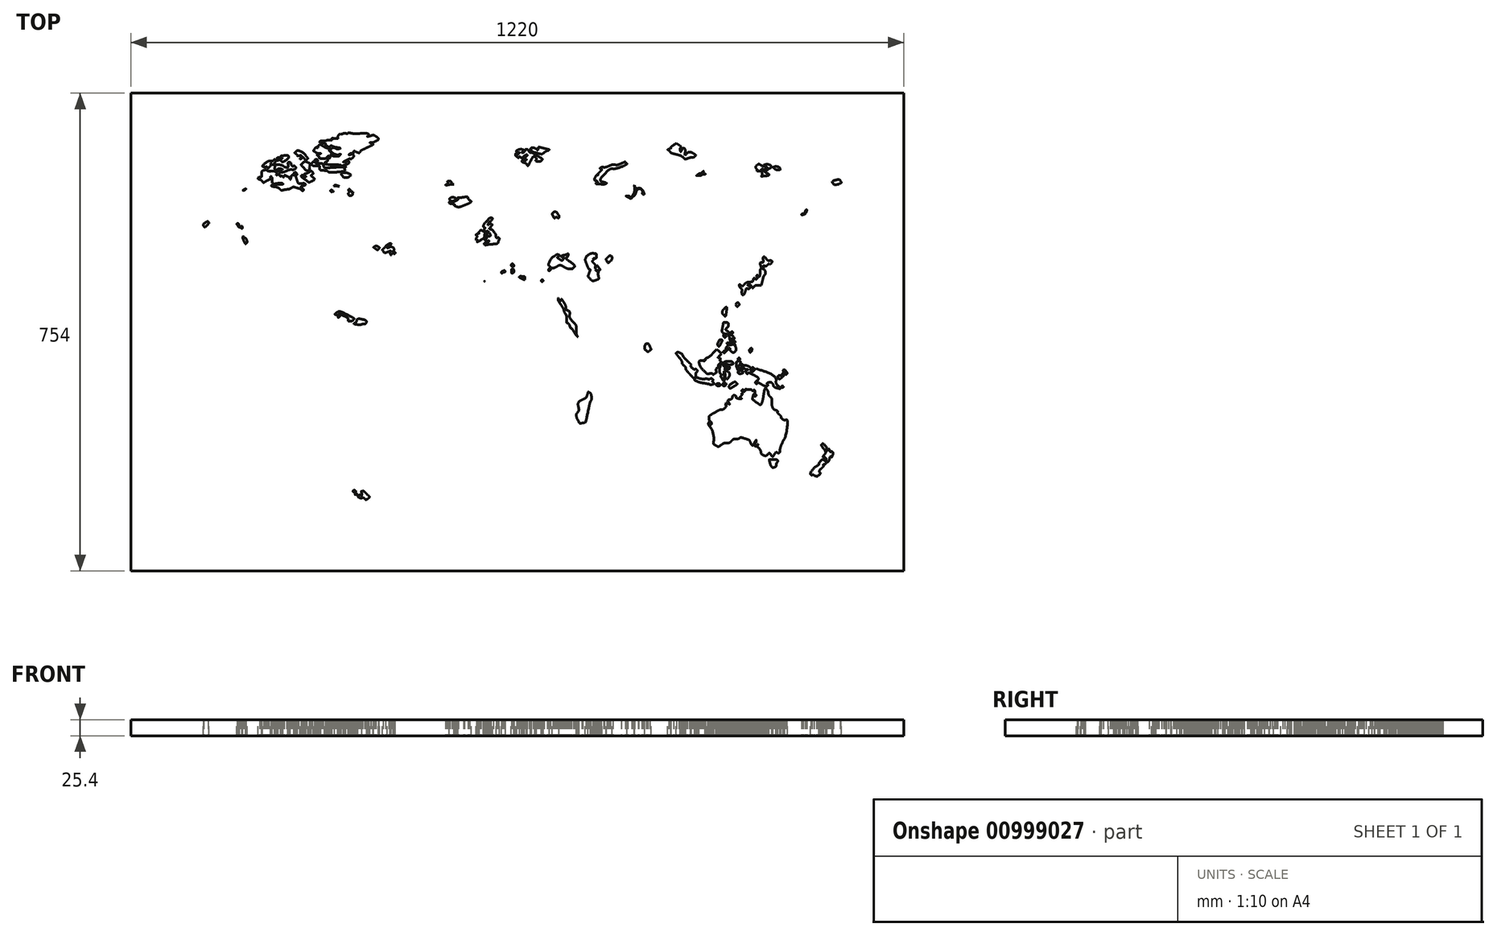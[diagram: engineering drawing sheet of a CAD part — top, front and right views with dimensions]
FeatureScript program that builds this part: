
annotation { "Feature Type Name" : "Feature", "Feature Type Description" : "" }
export const myFeature = defineFeature(function(context is Context, id is Id, definition is map)
    precondition{}
    {
        {
            var Q0;
            Q0=qCreatedBy(makeId("Top.planeOp"),FACE);
            var sketch = newSketch(context, id + "F0", { "sketchPlane" : qUnion([Q0])});
            skLineSegment(sketch, "E0.bottom", {"start": v(610, -377) * mm, "end": v(-610, -377) * mm});
            skLineSegment(sketch, "E0.top", {"start": v(610, 377) * mm, "end": v(-610, 377) * mm});
            skLineSegment(sketch, "E0.left", {"start": v(610, -377) * mm, "end": v(610, 377) * mm});
            skLineSegment(sketch, "E0.right", {"start": v(-610, -377) * mm, "end": v(-610, 377) * mm});
            skPoint(sketch, "E0.middle", {"position": v(0, 0) * mm});
            skSolve(sketch);
        }
        {
            var Q0;
            Q0=makeQuery(id+"F0.imprint","IMPRINT",FACE,{"disambiguationData":[TD([[makeQuery(id+"F0.imprint","IMPRINT",EDGE,{"derivedFrom":sQuery(id+"F0.wireOp",EDGE,"E0.bottom")}),-1.0]])]});
            var sketch = newSketch(context, id + "F1", { "sketchPlane" : qUnion([Q0])});
            skLineSegment(sketch, "E1", {"start": v(571.5, 342.75) * mm, "end": v(571.5, -342.75) * mm});
            skFitSpline(sketch, "E2", {"points": [v(-240.66, -263.07) * mm, v(-241.04, -262.46) * mm, v(-242.9, -261.96) * mm, v(-244.8, -261.96) * mm]});
            skFitSpline(sketch, "E3", {"points": [v(-244.8, -261.96) * mm, v(-248.42, -261.96) * mm, v(-251.99, -259.06) * mm, v(-249.93, -257.79) * mm]});
            skFitSpline(sketch, "E4", {"points": [v(-249.93, -257.79) * mm, v(-249.28, -257.39) * mm, v(-247.96, -257.37) * mm, v(-246.98, -257.75) * mm]});
            skFitSpline(sketch, "E5", {"points": [v(-246.98, -257.75) * mm, v(-245.7, -258.24) * mm, v(-245.28, -257.64) * mm, v(-245.49, -255.61) * mm]});
            skFitSpline(sketch, "E6", {"points": [v(-245.49, -255.61) * mm, v(-245.91, -251.52) * mm, v(-245.94, -251.5) * mm, v(-247.74, -253.97) * mm]});
            skFitSpline(sketch, "E7", {"points": [v(-247.74, -253.97) * mm, v(-249.4, -256.24) * mm, v(-252.91, -255.54) * mm, v(-251.48, -253.22) * mm]});
            skFitSpline(sketch, "E8", {"points": [v(-251.48, -253.22) * mm, v(-250.74, -252.02) * mm, v(-255.25, -248.1) * mm, v(-257.7, -247.8) * mm]});
            skFitSpline(sketch, "E9", {"points": [v(-257.7, -247.8) * mm, v(-260.57, -247.47) * mm, v(-260.85, -247.22) * mm, v(-259.92, -245.77) * mm]});
            skFitSpline(sketch, "E10", {"points": [v(-259.92, -245.77) * mm, v(-259.37, -244.93) * mm, v(-258.93, -241.49) * mm, v(-258.93, -238.13) * mm]});
            skFitSpline(sketch, "E11", {"points": [v(-258.93, -238.13) * mm, v(-258.93, -233.06) * mm, v(-258.56, -232.04) * mm, v(-256.79, -232.19) * mm]});
            skFitSpline(sketch, "E12", {"points": [v(-256.79, -232.19) * mm, v(-255.61, -232.28) * mm, v(-254.65, -232.14) * mm, v(-254.65, -231.88) * mm]});
            skFitSpline(sketch, "E13", {"points": [v(-254.65, -231.88) * mm, v(-254.65, -231.07) * mm, v(-260.1, -225.9) * mm, v(-260.96, -225.9) * mm]});
            skFitSpline(sketch, "E14", {"points": [v(-260.96, -225.9) * mm, v(-262.9, -225.9) * mm, v(-263.3, -224.08) * mm, v(-261.92, -221.51) * mm]});
            skFitSpline(sketch, "E15", {"points": [v(-261.92, -221.51) * mm, v(-260.54, -218.93) * mm, v(-260.33, -218.89) * mm, v(-258.88, -220.87) * mm]});
            skFitSpline(sketch, "E16", {"points": [v(-258.88, -220.87) * mm, v(-257.32, -223.01) * mm, v(-256.13, -222.3) * mm, v(-256.56, -219.49) * mm]});
            skFitSpline(sketch, "E17", {"points": [v(-256.56, -219.49) * mm, v(-256.68, -218.65) * mm, v(-256.86, -217.4) * mm, v(-256.94, -216.74) * mm]});
            skFitSpline(sketch, "E18", {"points": [v(-256.94, -216.74) * mm, v(-257.02, -216.07) * mm, v(-257.5, -215.65) * mm, v(-258.01, -215.82) * mm]});
            skFitSpline(sketch, "E19", {"points": [v(-258.01, -215.82) * mm, v(-258.51, -215.99) * mm, v(-259.06, -215.71) * mm, v(-259.23, -215.2) * mm]});
            skFitSpline(sketch, "E20", {"points": [v(-259.23, -215.2) * mm, v(-259.92, -213.14) * mm, v(-259.44, -212.85) * mm, v(-257.7, -214.3) * mm]});
            skFitSpline(sketch, "E21", {"points": [v(-257.7, -214.3) * mm, v(-256.13, -215.6) * mm, v(-255.87, -215.18) * mm, v(-255.87, -211.37) * mm]});
            skFitSpline(sketch, "E22", {"points": [v(-255.87, -211.37) * mm, v(-255.87, -208.93) * mm, v(-256.54, -205.86) * mm, v(-257.36, -204.55) * mm]});
            skFitSpline(sketch, "E23", {"points": [v(-257.36, -204.55) * mm, v(-258.52, -202.68) * mm, v(-258.52, -201.28) * mm, v(-257.35, -198.04) * mm]});
            skFitSpline(sketch, "E24", {"points": [v(-257.35, -198.04) * mm, v(-256.53, -195.77) * mm, v(-256.18, -192.25) * mm, v(-256.59, -190.23) * mm]});
            skFitSpline(sketch, "E25", {"points": [v(-256.59, -190.23) * mm, v(-257.12, -187.58) * mm, v(-256.39, -184.72) * mm, v(-253.97, -179.95) * mm]});
            skFitSpline(sketch, "E26", {"points": [v(-253.97, -179.95) * mm, v(-251.78, -175.64) * mm, v(-250.5, -171.02) * mm, v(-250.29, -166.63) * mm]});
            skFitSpline(sketch, "E27", {"points": [v(-250.29, -166.63) * mm, v(-250.1, -162.93) * mm, v(-249.28, -150.48) * mm, v(-248.46, -138.97) * mm]});
            skFitSpline(sketch, "E28", {"points": [v(-248.46, -138.97) * mm, v(-247.96, -131.99) * mm, v(-247.46, -125) * mm, v(-246.96, -118.03) * mm]});
            skFitSpline(sketch, "E29", {"points": [v(-246.96, -118.03) * mm, v(-248.14, -116.98) * mm, v(-249.32, -115.92) * mm, v(-250.5, -114.87) * mm]});
            skFitSpline(sketch, "E30", {"points": [v(-250.5, -114.87) * mm, v(-252.45, -113.14) * mm, v(-256.45, -109.9) * mm, v(-259.4, -107.7) * mm]});
            skFitSpline(sketch, "E31", {"points": [v(-259.4, -107.7) * mm, v(-264.21, -104.08) * mm, v(-265.2, -102.4) * mm, v(-269.31, -90.85) * mm]});
            skFitSpline(sketch, "E32", {"points": [v(-269.31, -90.85) * mm, v(-271.83, -83.79) * mm, v(-275.05, -75.54) * mm, v(-276.47, -72.51) * mm]});
            skFitSpline(sketch, "E33", {"points": [v(-276.47, -72.51) * mm, v(-279, -67.15) * mm, v(-279, -66.97) * mm, v(-276.76, -65.1) * mm]});
            skFitSpline(sketch, "E34", {"points": [v(-276.76, -65.1) * mm, v(-274.73, -63.38) * mm, v(-274.68, -63.03) * mm, v(-276.37, -61.96) * mm]});
            skFitSpline(sketch, "E35", {"points": [v(-276.37, -61.96) * mm, v(-279.2, -60.18) * mm, v(-276.32, -50.02) * mm, v(-271.2, -43.78) * mm]});
            skFitSpline(sketch, "E36", {"points": [v(-271.2, -43.78) * mm, v(-268.03, -39.9) * mm, v(-267.15, -37.68) * mm, v(-267.07, -33.38) * mm]});
            skFitSpline(sketch, "E37", {"points": [v(-267.07, -33.38) * mm, v(-266.91, -24.01) * mm, v(-271.43, -17.2) * mm, v(-274.27, -22.53) * mm]});
            skFitSpline(sketch, "E38", {"points": [v(-274.27, -22.53) * mm, v(-275.2, -24.28) * mm, v(-276.03, -24.65) * mm, v(-277.07, -23.78) * mm]});
            skFitSpline(sketch, "E39", {"points": [v(-277.07, -23.78) * mm, v(-277.88, -23.1) * mm, v(-280.1, -22.35) * mm, v(-282.02, -22.1) * mm]});
            skFitSpline(sketch, "E40", {"points": [v(-282.02, -22.1) * mm, v(-284.08, -21.82) * mm, v(-286.1, -20.48) * mm, v(-287, -18.8) * mm]});
            skFitSpline(sketch, "E41", {"points": [v(-287, -18.8) * mm, v(-288, -16.93) * mm, v(-288.82, -16.44) * mm, v(-289.4, -17.37) * mm]});
            skFitSpline(sketch, "E42", {"points": [v(-289.4, -17.37) * mm, v(-290.77, -19.6) * mm, v(-292.54, -17.7) * mm, v(-292.54, -13.99) * mm]});
            skFitSpline(sketch, "E43", {"points": [v(-292.54, -13.99) * mm, v(-292.54, -10.56) * mm, v(-296.87, -5.29) * mm, v(-299.7, -5.29) * mm]});
            skFitSpline(sketch, "E44", {"points": [v(-299.7, -5.29) * mm, v(-301.6, -5.29) * mm, v(-309.43, -1.3) * mm, v(-315.18, 2.6) * mm]});
            skFitSpline(sketch, "E45", {"points": [v(-315.18, 2.6) * mm, v(-318.8, 5.06) * mm, v(-320.04, 5.35) * mm, v(-321.88, 4.2) * mm]});
            skFitSpline(sketch, "E46", {"points": [v(-321.88, 4.2) * mm, v(-323.76, 3.03) * mm, v(-325.96, 3.68) * mm, v(-334.56, 7.94) * mm]});
            skFitSpline(sketch, "E47", {"points": [v(-334.56, 7.94) * mm, v(-347.59, 14.4) * mm, v(-352.85, 18.64) * mm, v(-351.97, 21.98) * mm]});
            skFitSpline(sketch, "E48", {"points": [v(-351.97, 21.98) * mm, v(-351.2, 24.95) * mm, v(-352.7, 28) * mm, v(-358.12, 34.35) * mm]});
            skFitSpline(sketch, "E49", {"points": [v(-358.12, 34.35) * mm, v(-360.37, 36.99) * mm, v(-362.2, 39.63) * mm, v(-362.2, 40.2) * mm]});
            skFitSpline(sketch, "E50", {"points": [v(-362.2, 40.2) * mm, v(-362.2, 40.79) * mm, v(-364.37, 44.12) * mm, v(-367.01, 47.62) * mm]});
            skFitSpline(sketch, "E51", {"points": [v(-367.01, 47.62) * mm, v(-369.65, 51.13) * mm, v(-372.39, 55.5) * mm, v(-373.1, 57.35) * mm]});
            skFitSpline(sketch, "E52", {"points": [v(-373.1, 57.35) * mm, v(-374.39, 60.76) * mm, v(-376.88, 61.97) * mm, v(-376.87, 59.18) * mm]});
            skFitSpline(sketch, "E53", {"points": [v(-376.87, 59.18) * mm, v(-376.87, 58.34) * mm, v(-375.77, 55.85) * mm, v(-374.42, 53.65) * mm]});
            skFitSpline(sketch, "E54", {"points": [v(-374.42, 53.65) * mm, v(-373.08, 51.45) * mm, v(-371.98, 49.14) * mm, v(-371.98, 48.52) * mm]});
            skFitSpline(sketch, "E55", {"points": [v(-371.98, 48.52) * mm, v(-371.98, 47.9) * mm, v(-370.33, 44.94) * mm, v(-368.32, 41.96) * mm]});
            skFitSpline(sketch, "E56", {"points": [v(-368.32, 41.96) * mm, v(-366.3, 38.97) * mm, v(-364.65, 36.11) * mm, v(-364.65, 35.61) * mm]});
            skFitSpline(sketch, "E57", {"points": [v(-364.65, 35.61) * mm, v(-364.65, 35.11) * mm, v(-363.69, 34) * mm, v(-362.51, 33.12) * mm]});
            skFitSpline(sketch, "E58", {"points": [v(-362.51, 33.12) * mm, v(-360.88, 31.92) * mm, v(-360.71, 31.2) * mm, v(-361.8, 30.1) * mm]});
            skFitSpline(sketch, "E59", {"points": [v(-361.8, 30.1) * mm, v(-363.71, 28.15) * mm, v(-371.98, 34.67) * mm, v(-371.98, 38.13) * mm]});
            skFitSpline(sketch, "E60", {"points": [v(-371.98, 38.13) * mm, v(-371.98, 39.5) * mm, v(-373.7, 42.11) * mm, v(-375.8, 43.95) * mm]});
            skFitSpline(sketch, "E61", {"points": [v(-375.8, 43.95) * mm, v(-378.73, 46.53) * mm, v(-379.29, 47.67) * mm, v(-378.24, 48.93) * mm]});
            skFitSpline(sketch, "E62", {"points": [v(-378.24, 48.93) * mm, v(-377.2, 50.17) * mm, v(-377.46, 51.09) * mm, v(-379.28, 52.73) * mm]});
            skFitSpline(sketch, "E63", {"points": [v(-379.28, 52.73) * mm, v(-380.6, 53.92) * mm, v(-382.52, 57.8) * mm, v(-383.55, 61.34) * mm]});
            skFitSpline(sketch, "E64", {"points": [v(-383.55, 61.34) * mm, v(-384.6, 64.94) * mm, v(-386.1, 67.7) * mm, v(-386.95, 67.6) * mm]});
            skFitSpline(sketch, "E65", {"points": [v(-386.95, 67.6) * mm, v(-387.8, 67.5) * mm, v(-388.48, 67.92) * mm, v(-388.48, 68.52) * mm]});
            skFitSpline(sketch, "E66", {"points": [v(-388.48, 68.52) * mm, v(-388.48, 69.11) * mm, v(-389.72, 70.06) * mm, v(-391.24, 70.62) * mm]});
            skFitSpline(sketch, "E67", {"points": [v(-391.24, 70.62) * mm, v(-394.6, 71.86) * mm, v(-401.42, 82.26) * mm, v(-400.48, 84.7) * mm]});
            skFitSpline(sketch, "E68", {"points": [v(-400.48, 84.7) * mm, v(-400.1, 85.7) * mm, v(-400.42, 86.32) * mm, v(-401.24, 86.12) * mm]});
            skFitSpline(sketch, "E69", {"points": [v(-401.24, 86.12) * mm, v(-402.03, 85.93) * mm, v(-403.9, 87.97) * mm, v(-405.37, 90.66) * mm]});
            skFitSpline(sketch, "E70", {"points": [v(-405.37, 90.66) * mm, v(-407.37, 94.3) * mm, v(-407.96, 97.1) * mm, v(-407.66, 101.66) * mm]});
            skFitSpline(sketch, "E71", {"points": [v(-407.66, 101.66) * mm, v(-407.44, 105.02) * mm, v(-407.1, 111.77) * mm, v(-406.91, 116.65) * mm]});
            skFitSpline(sketch, "E72", {"points": [v(-406.91, 116.65) * mm, v(-406.53, 126.52) * mm, v(-405.96, 127.82) * mm, v(-403.08, 125.43) * mm]});
            skFitSpline(sketch, "E73", {"points": [v(-403.08, 125.43) * mm, v(-401.34, 123.98) * mm, v(-401.16, 124.2) * mm, v(-401.52, 127.3) * mm]});
            skFitSpline(sketch, "E74", {"points": [v(-401.52, 127.3) * mm, v(-401.74, 129.23) * mm, v(-402.7, 131.05) * mm, v(-403.63, 131.36) * mm]});
            skFitSpline(sketch, "E75", {"points": [v(-403.63, 131.36) * mm, v(-404.6, 131.68) * mm, v(-404.98, 131.37) * mm, v(-404.52, 130.62) * mm]});
            skFitSpline(sketch, "E76", {"points": [v(-404.52, 130.62) * mm, v(-403.13, 128.37) * mm, v(-405.77, 127.9) * mm, v(-409.42, 129.76) * mm]});
            skFitSpline(sketch, "E77", {"points": [v(-409.42, 129.76) * mm, v(-411.35, 130.74) * mm, v(-414.56, 132.87) * mm, v(-416.56, 134.48) * mm]});
            skFitSpline(sketch, "E78", {"points": [v(-416.56, 134.48) * mm, v(-419.7, 137.03) * mm, v(-419.97, 137.7) * mm, v(-418.55, 139.4) * mm]});
            skFitSpline(sketch, "E79", {"points": [v(-418.55, 139.4) * mm, v(-417.65, 140.49) * mm, v(-417.32, 141.38) * mm, v(-417.82, 141.38) * mm]});
            skFitSpline(sketch, "E80", {"points": [v(-417.82, 141.38) * mm, v(-418.32, 141.38) * mm, v(-418.1, 142.14) * mm, v(-417.33, 143.07) * mm]});
            skFitSpline(sketch, "E81", {"points": [v(-417.33, 143.07) * mm, v(-416.25, 144.37) * mm, v(-416.34, 144.92) * mm, v(-417.75, 145.46) * mm]});
            skFitSpline(sketch, "E82", {"points": [v(-417.75, 145.46) * mm, v(-418.75, 145.85) * mm, v(-419.9, 145.63) * mm, v(-420.3, 144.97) * mm]});
            skFitSpline(sketch, "E83", {"points": [v(-420.3, 144.97) * mm, v(-420.71, 144.32) * mm, v(-421.6, 144.12) * mm, v(-422.26, 144.54) * mm]});
            skFitSpline(sketch, "E84", {"points": [v(-422.26, 144.54) * mm, v(-423, 145) * mm, v(-422.7, 146.14) * mm, v(-421.51, 147.46) * mm]});
            skFitSpline(sketch, "E85", {"points": [v(-421.51, 147.46) * mm, v(-419.7, 149.46) * mm, v(-419.7, 149.7) * mm, v(-421.53, 150.4) * mm]});
            skFitSpline(sketch, "E86", {"points": [v(-421.53, 150.4) * mm, v(-424.1, 151.38) * mm, v(-424.57, 151.36) * mm, v(-424.4, 150.24) * mm]});
            skFitSpline(sketch, "E87", {"points": [v(-424.4, 150.24) * mm, v(-424.07, 148.19) * mm, v(-424.61, 147.39) * mm, v(-425.82, 148.14) * mm]});
            skFitSpline(sketch, "E88", {"points": [v(-425.82, 148.14) * mm, v(-426.7, 148.68) * mm, v(-426.65, 149.48) * mm, v(-425.67, 150.66) * mm]});
            skFitSpline(sketch, "E89", {"points": [v(-425.67, 150.66) * mm, v(-424.89, 151.6) * mm, v(-424.65, 152.38) * mm, v(-425.15, 152.38) * mm]});
            skFitSpline(sketch, "E90", {"points": [v(-425.15, 152.38) * mm, v(-425.65, 152.38) * mm, v(-425.55, 153.07) * mm, v(-424.92, 153.9) * mm]});
            skFitSpline(sketch, "E91", {"points": [v(-424.92, 153.9) * mm, v(-423.92, 155.25) * mm, v(-423.8, 156.35) * mm, v(-424.39, 159.25) * mm]});
            skFitSpline(sketch, "E92", {"points": [v(-424.39, 159.25) * mm, v(-424.47, 159.67) * mm, v(-425.37, 159.33) * mm, v(-426.37, 158.5) * mm]});
            skFitSpline(sketch, "E93", {"points": [v(-426.37, 158.5) * mm, v(-427.38, 157.65) * mm, v(-428.2, 157.31) * mm, v(-428.2, 157.73) * mm]});
            skFitSpline(sketch, "E94", {"points": [v(-428.2, 157.73) * mm, v(-428.2, 159.73) * mm, v(-427.87, 160.3) * mm, v(-426.86, 160.02) * mm]});
            skFitSpline(sketch, "E95", {"points": [v(-426.86, 160.02) * mm, v(-426.26, 159.85) * mm, v(-425.76, 160.54) * mm, v(-425.76, 161.55) * mm]});
            skFitSpline(sketch, "E96", {"points": [v(-425.76, 161.55) * mm, v(-425.76, 162.55) * mm, v(-426.52, 163.38) * mm, v(-427.45, 163.38) * mm]});
            skFitSpline(sketch, "E97", {"points": [v(-427.45, 163.38) * mm, v(-428.37, 163.38) * mm, v(-429.81, 164.2) * mm, v(-430.65, 165.21) * mm]});
            skFitSpline(sketch, "E98", {"points": [v(-430.65, 165.21) * mm, v(-432.25, 167.13) * mm, v(-434.42, 167.7) * mm, v(-434.17, 166.13) * mm]});
            skFitSpline(sketch, "E99", {"points": [v(-434.17, 166.13) * mm, v(-433.83, 163.97) * mm, v(-434.42, 163.3) * mm, v(-435.85, 164.2) * mm]});
            skFitSpline(sketch, "E100", {"points": [v(-435.85, 164.2) * mm, v(-436.69, 164.74) * mm, v(-437.79, 165.25) * mm, v(-438.3, 165.35) * mm]});
            skFitSpline(sketch, "E101", {"points": [v(-438.3, 165.35) * mm, v(-438.8, 165.44) * mm, v(-439.51, 165.59) * mm, v(-439.9, 165.67) * mm]});
            skFitSpline(sketch, "E102", {"points": [v(-439.9, 165.67) * mm, v(-440.27, 165.75) * mm, v(-440.22, 166.4) * mm, v(-439.78, 167.1) * mm]});
            skFitSpline(sketch, "E103", {"points": [v(-439.78, 167.1) * mm, v(-439.23, 168) * mm, v(-438.5, 167.97) * mm, v(-437.37, 167.05) * mm]});
            skFitSpline(sketch, "E104", {"points": [v(-437.37, 167.05) * mm, v(-434.82, 164.93) * mm, v(-434.31, 167.38) * mm, v(-436.4, 171.7) * mm]});
            skFitSpline(sketch, "E105", {"points": [v(-436.4, 171.7) * mm, v(-437.75, 174.48) * mm, v(-438.73, 175.29) * mm, v(-439.74, 174.44) * mm]});
            skFitSpline(sketch, "E106", {"points": [v(-439.74, 174.44) * mm, v(-440.71, 173.64) * mm, v(-443.1, 174.22) * mm, v(-447.08, 176.24) * mm]});
            skFitSpline(sketch, "E107", {"points": [v(-447.08, 176.24) * mm, v(-450.33, 177.88) * mm, v(-455.8, 179.56) * mm, v(-459.24, 179.97) * mm]});
            skFitSpline(sketch, "E108", {"points": [v(-459.24, 179.97) * mm, v(-465.93, 180.77) * mm, v(-473.43, 183.6) * mm, v(-473.43, 185.33) * mm]});
            skFitSpline(sketch, "E109", {"points": [v(-473.43, 185.33) * mm, v(-473.43, 186.58) * mm, v(-476.35, 186.34) * mm, v(-476.8, 185.05) * mm]});
            skFitSpline(sketch, "E110", {"points": [v(-476.8, 185.05) * mm, v(-477.47, 183.07) * mm, v(-477.03, 181.6) * mm, v(-475.96, 182.27) * mm]});
            skFitSpline(sketch, "E111", {"points": [v(-475.96, 182.27) * mm, v(-475.33, 182.66) * mm, v(-474.5, 182.45) * mm, v(-474.1, 181.82) * mm]});
            skFitSpline(sketch, "E112", {"points": [v(-474.1, 181.82) * mm, v(-473.71, 181.18) * mm, v(-473.91, 180.34) * mm, v(-474.55, 179.94) * mm]});
            skFitSpline(sketch, "E113", {"points": [v(-474.55, 179.94) * mm, v(-475.18, 179.55) * mm, v(-476.02, 179.74) * mm, v(-476.41, 180.37) * mm]});
            skFitSpline(sketch, "E114", {"points": [v(-476.41, 180.37) * mm, v(-476.82, 181.04) * mm, v(-478.64, 180.76) * mm, v(-480.76, 179.7) * mm]});
            skFitSpline(sketch, "E115", {"points": [v(-480.76, 179.7) * mm, v(-482.76, 178.7) * mm, v(-484.96, 178.23) * mm, v(-485.64, 178.65) * mm]});
            skFitSpline(sketch, "E116", {"points": [v(-485.64, 178.65) * mm, v(-487.62, 179.87) * mm, v(-487.07, 183.92) * mm, v(-484.74, 185.28) * mm]});
            skFitSpline(sketch, "E117", {"points": [v(-484.74, 185.28) * mm, v(-482.7, 186.46) * mm, v(-482.7, 186.53) * mm, v(-484.77, 186.56) * mm]});
            skFitSpline(sketch, "E118", {"points": [v(-484.77, 186.56) * mm, v(-485.96, 186.59) * mm, v(-487.44, 185.28) * mm, v(-488.05, 183.67) * mm]});
            skFitSpline(sketch, "E119", {"points": [v(-488.05, 183.67) * mm, v(-488.67, 182.05) * mm, v(-489.76, 180.36) * mm, v(-490.49, 179.91) * mm]});
            skFitSpline(sketch, "E120", {"points": [v(-490.49, 179.91) * mm, v(-491.21, 179.47) * mm, v(-491.53, 178.66) * mm, v(-491.2, 178.12) * mm]});
            skFitSpline(sketch, "E121", {"points": [v(-491.2, 178.12) * mm, v(-490.29, 176.64) * mm, v(-498.58, 168.6) * mm, v(-504.22, 165.5) * mm]});
            skFitSpline(sketch, "E122", {"points": [v(-504.22, 165.5) * mm, v(-514.43, 159.9) * mm, v(-514.16, 160.13) * mm, v(-511.8, 159.22) * mm]});
            skFitSpline(sketch, "E123", {"points": [v(-511.8, 159.22) * mm, v(-510.29, 158.64) * mm, v(-510.06, 158.03) * mm, v(-511, 157.1) * mm]});
            skFitSpline(sketch, "E124", {"points": [v(-511, 157.1) * mm, v(-512.52, 155.58) * mm, v(-515.38, 156.86) * mm, v(-514.32, 158.58) * mm]});
            skFitSpline(sketch, "E125", {"points": [v(-514.32, 158.58) * mm, v(-513.33, 160.18) * mm, v(-516.66, 160) * mm, v(-518.3, 158.35) * mm]});
            skFitSpline(sketch, "E126", {"points": [v(-518.3, 158.35) * mm, v(-519.84, 156.81) * mm, v(-522.73, 158.05) * mm, v(-521.66, 159.8) * mm]});
            skFitSpline(sketch, "E127", {"points": [v(-521.66, 159.8) * mm, v(-521.27, 160.42) * mm, v(-518.02, 162.32) * mm, v(-514.43, 164.02) * mm]});
            skFitSpline(sketch, "E128", {"points": [v(-514.43, 164.02) * mm, v(-507.32, 167.38) * mm, v(-505.96, 168.62) * mm, v(-504.62, 172.98) * mm]});
            skFitSpline(sketch, "E129", {"points": [v(-504.62, 172.98) * mm, v(-503.87, 175.45) * mm, v(-504.04, 175.7) * mm, v(-505.82, 174.7) * mm]});
            skFitSpline(sketch, "E130", {"points": [v(-505.82, 174.7) * mm, v(-508.26, 173.33) * mm, v(-515.9, 175.58) * mm, v(-517.95, 178.25) * mm]});
            skFitSpline(sketch, "E131", {"points": [v(-517.95, 178.25) * mm, v(-518.67, 179.2) * mm, v(-520.11, 179.8) * mm, v(-521.15, 179.58) * mm]});
            skFitSpline(sketch, "E132", {"points": [v(-521.15, 179.58) * mm, v(-523.33, 179.12) * mm, v(-527.8, 183.58) * mm, v(-528.93, 187.35) * mm]});
            skFitSpline(sketch, "E133", {"points": [v(-528.93, 187.35) * mm, v(-529.79, 190.18) * mm, v(-526.63, 195.03) * mm, v(-523.54, 195.65) * mm]});
            skFitSpline(sketch, "E134", {"points": [v(-523.54, 195.65) * mm, v(-518.72, 196.61) * mm, v(-515.77, 198.62) * mm, v(-515.59, 201.07) * mm]});
            skFitSpline(sketch, "E135", {"points": [v(-515.59, 201.07) * mm, v(-515.36, 204.16) * mm, v(-516.03, 204.4) * mm, v(-517.9, 201.92) * mm]});
            skFitSpline(sketch, "E136", {"points": [v(-517.9, 201.92) * mm, v(-519.76, 199.46) * mm, v(-531.49, 201.03) * mm, v(-531.49, 203.73) * mm]});
            skFitSpline(sketch, "E137", {"points": [v(-531.49, 203.73) * mm, v(-531.49, 204.73) * mm, v(-532.51, 205.97) * mm, v(-533.77, 206.48) * mm]});
            skFitSpline(sketch, "E138", {"points": [v(-533.77, 206.48) * mm, v(-535.63, 207.24) * mm, v(-535.77, 207.74) * mm, v(-534.53, 209.23) * mm]});
            skFitSpline(sketch, "E139", {"points": [v(-534.53, 209.23) * mm, v(-533.7, 210.23) * mm, v(-532.1, 211.05) * mm, v(-530.97, 211.05) * mm]});
            skFitSpline(sketch, "E140", {"points": [v(-530.97, 211.05) * mm, v(-529.84, 211.05) * mm, v(-528.35, 211.61) * mm, v(-527.66, 212.3) * mm]});
            skFitSpline(sketch, "E141", {"points": [v(-527.66, 212.3) * mm, v(-526.8, 213.17) * mm, v(-525.33, 213) * mm, v(-522.99, 211.8) * mm]});
            skFitSpline(sketch, "E142", {"points": [v(-522.99, 211.8) * mm, v(-519.58, 210.02) * mm, v(-516.2, 210.33) * mm, v(-516.2, 212.4) * mm]});
            skFitSpline(sketch, "E143", {"points": [v(-516.2, 212.4) * mm, v(-516.2, 213) * mm, v(-516.62, 213.4) * mm, v(-517.13, 213.3) * mm]});
            skFitSpline(sketch, "E144", {"points": [v(-517.13, 213.3) * mm, v(-518.84, 212.92) * mm, v(-524.14, 215.86) * mm, v(-528.25, 219.46) * mm]});
            skFitSpline(sketch, "E145", {"points": [v(-528.25, 219.46) * mm, v(-529.62, 220.65) * mm, v(-530.98, 221.85) * mm, v(-532.35, 223.05) * mm]});
            skFitSpline(sketch, "E146", {"points": [v(-532.35, 223.05) * mm, v(-531.31, 223.73) * mm, v(-530.27, 224.4) * mm, v(-529.23, 225.1) * mm]});
            skFitSpline(sketch, "E147", {"points": [v(-529.23, 225.1) * mm, v(-527.52, 226.21) * mm, v(-525.2, 227.27) * mm, v(-524.08, 227.43) * mm]});
            skFitSpline(sketch, "E148", {"points": [v(-524.08, 227.43) * mm, v(-522.96, 227.6) * mm, v(-521.14, 228.88) * mm, v(-520.04, 230.3) * mm]});
            skFitSpline(sketch, "E149", {"points": [v(-520.04, 230.3) * mm, v(-518.94, 231.7) * mm, v(-516.67, 233.04) * mm, v(-514.99, 233.26) * mm]});
            skFitSpline(sketch, "E150", {"points": [v(-514.99, 233.26) * mm, v(-513.3, 233.48) * mm, v(-511.26, 234.48) * mm, v(-510.44, 235.5) * mm]});
            skFitSpline(sketch, "E151", {"points": [v(-510.44, 235.5) * mm, v(-509.62, 236.5) * mm, v(-508.94, 236.85) * mm, v(-508.91, 236.27) * mm]});
            skFitSpline(sketch, "E152", {"points": [v(-508.91, 236.27) * mm, v(-508.9, 235.69) * mm, v(-507.53, 236.1) * mm, v(-505.88, 237.17) * mm]});
            skFitSpline(sketch, "E153", {"points": [v(-505.88, 237.17) * mm, v(-503.94, 238.45) * mm, v(-502.62, 238.69) * mm, v(-502.1, 237.86) * mm]});
            skFitSpline(sketch, "E154", {"points": [v(-502.1, 237.86) * mm, v(-501.57, 237) * mm, v(-500.81, 237.02) * mm, v(-499.7, 237.94) * mm]});
            skFitSpline(sketch, "E155", {"points": [v(-499.7, 237.94) * mm, v(-498.6, 238.86) * mm, v(-497.85, 238.88) * mm, v(-497.3, 238) * mm]});
            skFitSpline(sketch, "E156", {"points": [v(-497.3, 238) * mm, v(-496.86, 237.3) * mm, v(-494.96, 236.71) * mm, v(-493.06, 236.71) * mm]});
            skFitSpline(sketch, "E157", {"points": [v(-493.06, 236.71) * mm, v(-491.17, 236.71) * mm, v(-488.94, 235.9) * mm, v(-488.12, 234.9) * mm]});
            skFitSpline(sketch, "E158", {"points": [v(-488.12, 234.9) * mm, v(-487, 233.56) * mm, v(-486.02, 233.42) * mm, v(-484.3, 234.34) * mm]});
            skFitSpline(sketch, "E159", {"points": [v(-484.3, 234.34) * mm, v(-482.72, 235.18) * mm, v(-481.22, 235.17) * mm, v(-479.57, 234.28) * mm]});
            skFitSpline(sketch, "E160", {"points": [v(-479.57, 234.28) * mm, v(-478.24, 233.57) * mm, v(-473.84, 232.94) * mm, v(-469.78, 232.89) * mm]});
            skFitSpline(sketch, "E161", {"points": [v(-469.78, 232.89) * mm, v(-465.73, 232.83) * mm, v(-462.1, 232.3) * mm, v(-461.74, 231.7) * mm]});
            skFitSpline(sketch, "E162", {"points": [v(-461.74, 231.7) * mm, v(-461.37, 231.1) * mm, v(-459.8, 230.6) * mm, v(-458.23, 230.6) * mm]});
            skFitSpline(sketch, "E163", {"points": [v(-458.23, 230.6) * mm, v(-456.68, 230.6) * mm, v(-453, 229.74) * mm, v(-450.06, 228.68) * mm]});
            skFitSpline(sketch, "E164", {"points": [v(-450.06, 228.68) * mm, v(-447.11, 227.62) * mm, v(-443.74, 226.55) * mm, v(-442.56, 226.3) * mm]});
            skFitSpline(sketch, "E165", {"points": [v(-442.56, 226.3) * mm, v(-439, 225.55) * mm, v(-437.99, 224.48) * mm, v(-437.99, 221.44) * mm]});
            skFitSpline(sketch, "E166", {"points": [v(-437.99, 221.44) * mm, v(-437.99, 219.84) * mm, v(-437.44, 218.2) * mm, v(-436.78, 217.78) * mm]});
            skFitSpline(sketch, "E167", {"points": [v(-436.78, 217.78) * mm, v(-435.33, 216.88) * mm, v(-436.57, 224.41) * mm, v(-438.22, 226.52) * mm]});
            skFitSpline(sketch, "E168", {"points": [v(-438.22, 226.52) * mm, v(-438.9, 227.38) * mm, v(-438.86, 228.23) * mm, v(-438.13, 228.68) * mm]});
            skFitSpline(sketch, "E169", {"points": [v(-438.13, 228.68) * mm, v(-437.47, 229.09) * mm, v(-436.57, 228.84) * mm, v(-436.13, 228.12) * mm]});
            skFitSpline(sketch, "E170", {"points": [v(-436.13, 228.12) * mm, v(-435.6, 227.27) * mm, v(-433.83, 227.7) * mm, v(-430.98, 229.39) * mm]});
            skFitSpline(sketch, "E171", {"points": [v(-430.98, 229.39) * mm, v(-425.42, 232.67) * mm, v(-421.19, 231.63) * mm, v(-425.77, 228.1) * mm]});
            skFitSpline(sketch, "E172", {"points": [v(-425.77, 228.1) * mm, v(-429.59, 225.18) * mm, v(-427.15, 224.94) * mm, v(-423.17, 227.85) * mm]});
            skFitSpline(sketch, "E173", {"points": [v(-423.17, 227.85) * mm, v(-416.35, 232.84) * mm, v(-414.97, 233.22) * mm, v(-410.99, 231.16) * mm]});
            skFitSpline(sketch, "E174", {"points": [v(-410.99, 231.16) * mm, v(-408.5, 229.87) * mm, v(-406.77, 229.62) * mm, v(-405.81, 230.42) * mm]});
            skFitSpline(sketch, "E175", {"points": [v(-405.81, 230.42) * mm, v(-404, 231.93) * mm, v(-395.91, 230.48) * mm, v(-390.54, 227.68) * mm]});
            skFitSpline(sketch, "E176", {"points": [v(-390.54, 227.68) * mm, v(-387.37, 226.02) * mm, v(-386.1, 225.88) * mm, v(-384.74, 227) * mm]});
            skFitSpline(sketch, "E177", {"points": [v(-384.74, 227) * mm, v(-383.37, 228.13) * mm, v(-382.29, 227.98) * mm, v(-379.72, 226.3) * mm]});
            skFitSpline(sketch, "E178", {"points": [v(-379.72, 226.3) * mm, v(-376.77, 224.37) * mm, v(-376.65, 224.01) * mm, v(-378.48, 222.68) * mm]});
            skFitSpline(sketch, "E179", {"points": [v(-378.48, 222.68) * mm, v(-381.43, 220.51) * mm, v(-379.94, 219.83) * mm, v(-373.79, 220.53) * mm]});
            skFitSpline(sketch, "E180", {"points": [v(-373.79, 220.53) * mm, v(-367.16, 221.27) * mm, v(-360.98, 218.99) * mm, v(-360.98, 215.79) * mm]});
            skFitSpline(sketch, "E181", {"points": [v(-360.98, 215.79) * mm, v(-360.98, 214.52) * mm, v(-360.51, 213.5) * mm, v(-359.94, 213.5) * mm]});
            skFitSpline(sketch, "E182", {"points": [v(-359.94, 213.5) * mm, v(-358.12, 213.5) * mm, v(-359.06, 220.76) * mm, v(-360.98, 221.5) * mm]});
            skFitSpline(sketch, "E183", {"points": [v(-360.98, 221.5) * mm, v(-362.5, 222.1) * mm, v(-362.4, 222.53) * mm, v(-360.37, 224.03) * mm]});
            skFitSpline(sketch, "E184", {"points": [v(-360.37, 224.03) * mm, v(-358.13, 225.69) * mm, v(-358.37, 225.77) * mm, v(-363.43, 225.06) * mm]});
            skFitSpline(sketch, "E185", {"points": [v(-363.43, 225.06) * mm, v(-366.45, 224.63) * mm, v(-369.7, 224.04) * mm, v(-370.65, 223.74) * mm]});
            skFitSpline(sketch, "E186", {"points": [v(-370.65, 223.74) * mm, v(-371.6, 223.44) * mm, v(-373.52, 224.27) * mm, v(-374.92, 225.58) * mm]});
            skFitSpline(sketch, "E187", {"points": [v(-374.92, 225.58) * mm, v(-376.33, 226.89) * mm, v(-379.27, 228.42) * mm, v(-381.46, 228.98) * mm]});
            skFitSpline(sketch, "E188", {"points": [v(-381.46, 228.98) * mm, v(-388.27, 230.71) * mm, v(-386.51, 232.42) * mm, v(-377.51, 232.8) * mm]});
            skFitSpline(sketch, "E189", {"points": [v(-377.51, 232.8) * mm, v(-371.98, 233.04) * mm, v(-369.6, 233.55) * mm, v(-370.72, 234.25) * mm]});
            skFitSpline(sketch, "E190", {"points": [v(-370.72, 234.25) * mm, v(-371.68, 234.84) * mm, v(-374.99, 235.02) * mm, v(-378.07, 234.66) * mm]});
            skFitSpline(sketch, "E191", {"points": [v(-378.07, 234.66) * mm, v(-384.35, 233.91) * mm, v(-386.77, 235.6) * mm, v(-387.08, 240.96) * mm]});
            skFitSpline(sketch, "E192", {"points": [v(-387.08, 240.96) * mm, v(-387.25, 243.85) * mm, v(-389.1, 245.53) * mm, v(-389.1, 242.8) * mm]});
            skFitSpline(sketch, "E193", {"points": [v(-389.1, 242.8) * mm, v(-389.1, 242.1) * mm, v(-390.33, 240.98) * mm, v(-391.85, 240.3) * mm]});
            skFitSpline(sketch, "E194", {"points": [v(-391.85, 240.3) * mm, v(-393.36, 239.61) * mm, v(-395.97, 238.27) * mm, v(-397.65, 237.3) * mm]});
            skFitSpline(sketch, "E195", {"points": [v(-397.65, 237.3) * mm, v(-400.4, 235.73) * mm, v(-400.9, 235.78) * mm, v(-402.54, 237.79) * mm]});
            skFitSpline(sketch, "E196", {"points": [v(-402.54, 237.79) * mm, v(-403.55, 239.02) * mm, v(-405.37, 240.38) * mm, v(-406.59, 240.8) * mm]});
            skFitSpline(sketch, "E197", {"points": [v(-406.59, 240.8) * mm, v(-409.06, 241.67) * mm, v(-408.28, 244.05) * mm, v(-405.52, 244.05) * mm]});
            skFitSpline(sketch, "E198", {"points": [v(-405.52, 244.05) * mm, v(-404.55, 244.05) * mm, v(-403.7, 245) * mm, v(-403.63, 246.19) * mm]});
            skFitSpline(sketch, "E199", {"points": [v(-403.63, 246.19) * mm, v(-403.56, 247.36) * mm, v(-403.42, 249.38) * mm, v(-403.33, 250.66) * mm]});
            skFitSpline(sketch, "E200", {"points": [v(-403.33, 250.66) * mm, v(-403.12, 253.38) * mm, v(-397.4, 255.73) * mm, v(-394.25, 254.38) * mm]});
            skFitSpline(sketch, "E201", {"points": [v(-394.25, 254.38) * mm, v(-393.1, 253.88) * mm, v(-390.61, 253.6) * mm, v(-388.73, 253.75) * mm]});
            skFitSpline(sketch, "E202", {"points": [v(-388.73, 253.75) * mm, v(-384.77, 254.07) * mm, v(-378.86, 250.67) * mm, v(-380.04, 248.75) * mm]});
            skFitSpline(sketch, "E203", {"points": [v(-380.04, 248.75) * mm, v(-380.57, 247.9) * mm, v(-379.94, 247.74) * mm, v(-378.24, 248.28) * mm]});
            skFitSpline(sketch, "E204", {"points": [v(-378.24, 248.28) * mm, v(-376.45, 248.85) * mm, v(-375.41, 248.5) * mm, v(-374.9, 247.2) * mm]});
            skFitSpline(sketch, "E205", {"points": [v(-374.9, 247.2) * mm, v(-374.5, 246.14) * mm, v(-373.66, 245.6) * mm, v(-373.02, 246) * mm]});
            skFitSpline(sketch, "E206", {"points": [v(-373.02, 246) * mm, v(-372.4, 246.38) * mm, v(-371.14, 246.1) * mm, v(-370.24, 245.34) * mm]});
            skFitSpline(sketch, "E207", {"points": [v(-370.24, 245.34) * mm, v(-369, 244.32) * mm, v(-368.43, 244.43) * mm, v(-367.91, 245.79) * mm]});
            skFitSpline(sketch, "E208", {"points": [v(-367.91, 245.79) * mm, v(-367.3, 247.36) * mm, v(-366.74, 247.35) * mm, v(-363.4, 245.68) * mm]});
            skFitSpline(sketch, "E209", {"points": [v(-363.4, 245.68) * mm, v(-361.3, 244.64) * mm, v(-359.23, 242.88) * mm, v(-358.79, 241.77) * mm]});
            skFitSpline(sketch, "E210", {"points": [v(-358.79, 241.77) * mm, v(-358.2, 240.3) * mm, v(-357.82, 240.75) * mm, v(-357.34, 243.44) * mm]});
            skFitSpline(sketch, "E211", {"points": [v(-357.34, 243.44) * mm, v(-356.88, 246.06) * mm, v(-355.9, 247.21) * mm, v(-353.93, 247.5) * mm]});
            skFitSpline(sketch, "E212", {"points": [v(-353.93, 247.5) * mm, v(-352.41, 247.71) * mm, v(-351.46, 248.36) * mm, v(-351.82, 248.94) * mm]});
            skFitSpline(sketch, "E213", {"points": [v(-351.82, 248.94) * mm, v(-352.84, 250.59) * mm, v(-349.92, 251.8) * mm, v(-348.46, 250.35) * mm]});
            skFitSpline(sketch, "E214", {"points": [v(-348.46, 250.35) * mm, v(-347.53, 249.42) * mm, v(-347.53, 248.58) * mm, v(-348.46, 247.46) * mm]});
            skFitSpline(sketch, "E215", {"points": [v(-348.46, 247.46) * mm, v(-349.4, 246.33) * mm, v(-349.3, 244.52) * mm, v(-348.12, 241.11) * mm]});
            skFitSpline(sketch, "E216", {"points": [v(-348.12, 241.11) * mm, v(-346.25, 235.67) * mm, v(-344.62, 234.32) * mm, v(-339.97, 234.29) * mm]});
            skFitSpline(sketch, "E217", {"points": [v(-339.97, 234.29) * mm, v(-335.4, 234.26) * mm, v(-334.5, 232.07) * mm, v(-338.46, 230.57) * mm]});
            skFitSpline(sketch, "E218", {"points": [v(-338.46, 230.57) * mm, v(-341.54, 229.4) * mm, v(-341.62, 229.18) * mm, v(-339.75, 227.11) * mm]});
            skFitSpline(sketch, "E219", {"points": [v(-339.75, 227.11) * mm, v(-337.57, 224.7) * mm, v(-338.47, 222.54) * mm, v(-340.84, 224.5) * mm]});
            skFitSpline(sketch, "E220", {"points": [v(-340.84, 224.5) * mm, v(-341.64, 225.18) * mm, v(-344.78, 226.47) * mm, v(-347.8, 227.38) * mm]});
            skFitSpline(sketch, "E221", {"points": [v(-347.8, 227.38) * mm, v(-352.38, 228.76) * mm, v(-353.8, 228.77) * mm, v(-356.23, 227.42) * mm]});
            skFitSpline(sketch, "E222", {"points": [v(-356.23, 227.42) * mm, v(-359.07, 225.84) * mm, v(-359.03, 225.8) * mm, v(-354.53, 225.76) * mm]});
            skFitSpline(sketch, "E223", {"points": [v(-354.53, 225.76) * mm, v(-351.58, 225.73) * mm, v(-349.65, 225.05) * mm, v(-349.2, 223.88) * mm]});
            skFitSpline(sketch, "E224", {"points": [v(-349.2, 223.88) * mm, v(-348.82, 222.87) * mm, v(-347.98, 222.05) * mm, v(-347.34, 222.05) * mm]});
            skFitSpline(sketch, "E225", {"points": [v(-347.34, 222.05) * mm, v(-346.7, 222.05) * mm, v(-346.49, 222.56) * mm, v(-346.88, 223.19) * mm]});
            skFitSpline(sketch, "E226", {"points": [v(-346.88, 223.19) * mm, v(-347.26, 223.81) * mm, v(-347.06, 224.64) * mm, v(-346.42, 225.04) * mm]});
            skFitSpline(sketch, "E227", {"points": [v(-346.42, 225.04) * mm, v(-345.78, 225.43) * mm, v(-344.94, 225.23) * mm, v(-344.55, 224.6) * mm]});
            skFitSpline(sketch, "E228", {"points": [v(-344.55, 224.6) * mm, v(-344.16, 223.96) * mm, v(-344.49, 223.04) * mm, v(-345.28, 222.54) * mm]});
            skFitSpline(sketch, "E229", {"points": [v(-345.28, 222.54) * mm, v(-347.84, 220.96) * mm, v(-341.9, 219.66) * mm, v(-335.56, 220.41) * mm]});
            skFitSpline(sketch, "E230", {"points": [v(-335.56, 220.41) * mm, v(-331.66, 220.88) * mm, v(-329.61, 221.7) * mm, v(-329.61, 222.8) * mm]});
            skFitSpline(sketch, "E231", {"points": [v(-329.61, 222.8) * mm, v(-329.61, 223.73) * mm, v(-330.07, 224.56) * mm, v(-330.63, 224.64) * mm]});
            skFitSpline(sketch, "E232", {"points": [v(-330.63, 224.64) * mm, v(-331.2, 224.73) * mm, v(-332.2, 224.87) * mm, v(-332.87, 224.95) * mm]});
            skFitSpline(sketch, "E233", {"points": [v(-332.87, 224.95) * mm, v(-334.28, 225.13) * mm, v(-334.55, 226.9) * mm, v(-333.18, 227) * mm]});
            skFitSpline(sketch, "E234", {"points": [v(-333.18, 227) * mm, v(-332.67, 227.05) * mm, v(-331.1, 228.17) * mm, v(-329.7, 229.5) * mm]});
            skFitSpline(sketch, "E235", {"points": [v(-329.7, 229.5) * mm, v(-327.41, 231.64) * mm, v(-326.96, 231.7) * mm, v(-325.57, 230.03) * mm]});
            skFitSpline(sketch, "E236", {"points": [v(-325.57, 230.03) * mm, v(-324.72, 229) * mm, v(-323.25, 228.16) * mm, v(-322.32, 228.16) * mm]});
            skFitSpline(sketch, "E237", {"points": [v(-322.32, 228.16) * mm, v(-320.96, 228.16) * mm, v(-320.92, 228.62) * mm, v(-322.08, 230.48) * mm]});
            skFitSpline(sketch, "E238", {"points": [v(-322.08, 230.48) * mm, v(-323.25, 232.35) * mm, v(-323.13, 233.43) * mm, v(-321.45, 235.98) * mm]});
            skFitSpline(sketch, "E239", {"points": [v(-321.45, 235.98) * mm, v(-320.3, 237.73) * mm, v(-318.9, 239.16) * mm, v(-318.35, 239.16) * mm]});
            skFitSpline(sketch, "E240", {"points": [v(-318.35, 239.16) * mm, v(-317.78, 239.16) * mm, v(-317.91, 241.36) * mm, v(-318.63, 244.06) * mm]});
            skFitSpline(sketch, "E241", {"points": [v(-318.63, 244.06) * mm, v(-320.21, 250) * mm, v(-318.52, 252.33) * mm, v(-312.06, 253.09) * mm]});
            skFitSpline(sketch, "E242", {"points": [v(-312.06, 253.09) * mm, v(-305.9, 253.82) * mm, v(-303.96, 251.78) * mm, v(-307.38, 248.14) * mm]});
            skFitSpline(sketch, "E243", {"points": [v(-307.38, 248.14) * mm, v(-308.86, 246.56) * mm, v(-310.84, 245.27) * mm, v(-311.77, 245.27) * mm]});
            skFitSpline(sketch, "E244", {"points": [v(-311.77, 245.27) * mm, v(-312.7, 245.27) * mm, v(-313.16, 244.78) * mm, v(-312.8, 244.19) * mm]});
            skFitSpline(sketch, "E245", {"points": [v(-312.8, 244.19) * mm, v(-312.42, 243.59) * mm, v(-312.89, 242.47) * mm, v(-313.82, 241.69) * mm]});
            skFitSpline(sketch, "E246", {"points": [v(-313.82, 241.69) * mm, v(-315.24, 240.51) * mm, v(-314.94, 239.63) * mm, v(-312.02, 236.43) * mm]});
            skFitSpline(sketch, "E247", {"points": [v(-312.02, 236.43) * mm, v(-309.57, 233.75) * mm, v(-308.87, 232.15) * mm, v(-309.72, 231.13) * mm]});
            skFitSpline(sketch, "E248", {"points": [v(-309.72, 231.13) * mm, v(-310.57, 230.1) * mm, v(-310.2, 229.49) * mm, v(-308.45, 229.03) * mm]});
            skFitSpline(sketch, "E249", {"points": [v(-308.45, 229.03) * mm, v(-306.9, 228.63) * mm, v(-305.98, 227.37) * mm, v(-305.98, 225.66) * mm]});
            skFitSpline(sketch, "E250", {"points": [v(-305.98, 225.66) * mm, v(-305.98, 223.02) * mm, v(-305.9, 223.04) * mm, v(-303.4, 226.22) * mm]});
            skFitSpline(sketch, "E251", {"points": [v(-303.4, 226.22) * mm, v(-300.94, 229.35) * mm, v(-300.7, 229.4) * mm, v(-298.51, 227.42) * mm]});
            skFitSpline(sketch, "E252", {"points": [v(-298.51, 227.42) * mm, v(-297.24, 226.27) * mm, v(-296.2, 224.36) * mm, v(-296.2, 223.18) * mm]});
            skFitSpline(sketch, "E253", {"points": [v(-296.2, 223.18) * mm, v(-296.2, 218.96) * mm, v(-294.84, 216.97) * mm, v(-293, 218.5) * mm]});
            skFitSpline(sketch, "E254", {"points": [v(-293, 218.5) * mm, v(-291.13, 220.06) * mm, v(-290.66, 222.6) * mm, v(-292.45, 221.49) * mm]});
            skFitSpline(sketch, "E255", {"points": [v(-292.45, 221.49) * mm, v(-293.08, 221.1) * mm, v(-293.91, 221.3) * mm, v(-294.3, 221.94) * mm]});
            skFitSpline(sketch, "E256", {"points": [v(-294.3, 221.94) * mm, v(-294.7, 222.58) * mm, v(-294.5, 223.42) * mm, v(-293.86, 223.82) * mm]});
            skFitSpline(sketch, "E257", {"points": [v(-293.86, 223.82) * mm, v(-293.23, 224.2) * mm, v(-292.36, 223.96) * mm, v(-291.93, 223.27) * mm]});
            skFitSpline(sketch, "E258", {"points": [v(-291.93, 223.27) * mm, v(-290.55, 221.04) * mm, v(-288.78, 223.26) * mm, v(-290.05, 225.63) * mm]});
            skFitSpline(sketch, "E259", {"points": [v(-290.05, 225.63) * mm, v(-290.7, 226.84) * mm, v(-290.88, 228.18) * mm, v(-290.46, 228.6) * mm]});
            skFitSpline(sketch, "E260", {"points": [v(-290.46, 228.6) * mm, v(-287.42, 231.65) * mm, v(-276.08, 226.3) * mm, v(-278.75, 223.08) * mm]});
            skFitSpline(sketch, "E261", {"points": [v(-278.75, 223.08) * mm, v(-279.77, 221.85) * mm, v(-279.68, 220.83) * mm, v(-278.38, 219.06) * mm]});
            skFitSpline(sketch, "E262", {"points": [v(-278.38, 219.06) * mm, v(-277.43, 217.76) * mm, v(-276.65, 216.24) * mm, v(-276.65, 215.68) * mm]});
            skFitSpline(sketch, "E263", {"points": [v(-276.65, 215.68) * mm, v(-276.65, 214.06) * mm, v(-284.35, 209.83) * mm, v(-287.3, 209.83) * mm]});
            skFitSpline(sketch, "E264", {"points": [v(-287.3, 209.83) * mm, v(-291.42, 209.82) * mm, v(-289.45, 206.54) * mm, v(-284.81, 205.67) * mm]});
            skFitSpline(sketch, "E265", {"points": [v(-284.81, 205.67) * mm, v(-282.67, 205.27) * mm, v(-279.42, 203.35) * mm, v(-277.58, 201.4) * mm]});
            skFitSpline(sketch, "E266", {"points": [v(-277.58, 201.4) * mm, v(-274.7, 198.34) * mm, v(-274.5, 197.66) * mm, v(-276.06, 196.36) * mm]});
            skFitSpline(sketch, "E267", {"points": [v(-276.06, 196.36) * mm, v(-277.5, 195.16) * mm, v(-278.41, 195.22) * mm, v(-280.55, 196.64) * mm]});
            skFitSpline(sketch, "E268", {"points": [v(-280.55, 196.64) * mm, v(-283, 198.26) * mm, v(-283.45, 198.16) * mm, v(-285.74, 195.5) * mm]});
            skFitSpline(sketch, "E269", {"points": [v(-285.74, 195.5) * mm, v(-288.21, 192.64) * mm, v(-288.34, 192.63) * mm, v(-292.42, 194.67) * mm]});
            skFitSpline(sketch, "E270", {"points": [v(-292.42, 194.67) * mm, v(-296.1, 196.5) * mm, v(-296.35, 196.92) * mm, v(-294.56, 198.23) * mm]});
            skFitSpline(sketch, "E271", {"points": [v(-294.56, 198.23) * mm, v(-293.42, 199.06) * mm, v(-292.54, 201.38) * mm, v(-292.54, 203.54) * mm]});
            skFitSpline(sketch, "E272", {"points": [v(-292.54, 203.54) * mm, v(-292.54, 207.18) * mm, v(-292.77, 207.37) * mm, v(-297.12, 207.27) * mm]});
            skFitSpline(sketch, "E273", {"points": [v(-297.12, 207.27) * mm, v(-298.65, 207.23) * mm, v(-300.18, 207.2) * mm, v(-301.7, 207.16) * mm]});
            skFitSpline(sketch, "E274", {"points": [v(-301.7, 207.16) * mm, v(-300.38, 206.78) * mm, v(-299.06, 206.4) * mm, v(-297.73, 206.01) * mm]});
            skFitSpline(sketch, "E275", {"points": [v(-297.73, 206.01) * mm, v(-295.55, 205.38) * mm, v(-293.76, 204.37) * mm, v(-293.76, 203.77) * mm]});
            skFitSpline(sketch, "E276", {"points": [v(-293.76, 203.77) * mm, v(-293.76, 201.92) * mm, v(-300.21, 197.47) * mm, v(-301.93, 198.13) * mm]});
            skFitSpline(sketch, "E277", {"points": [v(-301.93, 198.13) * mm, v(-304.37, 199.07) * mm, v(-307.13, 197.61) * mm, v(-306.42, 195.76) * mm]});
            skFitSpline(sketch, "E278", {"points": [v(-306.42, 195.76) * mm, v(-306.08, 194.86) * mm, v(-306.87, 193.55) * mm, v(-308.18, 192.85) * mm]});
            skFitSpline(sketch, "E279", {"points": [v(-308.18, 192.85) * mm, v(-312.12, 190.74) * mm, v(-318.23, 180.22) * mm, v(-317.38, 177) * mm]});
            skFitSpline(sketch, "E280", {"points": [v(-317.38, 177) * mm, v(-316.87, 175.02) * mm, v(-315.98, 174.36) * mm, v(-314.42, 174.77) * mm]});
            skFitSpline(sketch, "E281", {"points": [v(-314.42, 174.77) * mm, v(-311.71, 175.47) * mm, v(-309.36, 172.94) * mm, v(-309.88, 169.89) * mm]});
            skFitSpline(sketch, "E282", {"points": [v(-309.88, 169.89) * mm, v(-310.11, 168.51) * mm, v(-309.62, 167.8) * mm, v(-308.59, 168.01) * mm]});
            skFitSpline(sketch, "E283", {"points": [v(-308.59, 168.01) * mm, v(-307.67, 168.2) * mm, v(-304.04, 166.39) * mm, v(-300.52, 163.96) * mm]});
            skFitSpline(sketch, "E284", {"points": [v(-300.52, 163.96) * mm, v(-296.41, 161.13) * mm, v(-292, 159.25) * mm, v(-288.14, 158.7) * mm]});
            skFitSpline(sketch, "E285", {"points": [v(-288.14, 158.7) * mm, v(-286.14, 158.4) * mm, v(-284.15, 158.12) * mm, v(-282.15, 157.83) * mm]});
            skFitSpline(sketch, "E286", {"points": [v(-282.15, 157.83) * mm, v(-282.3, 156.05) * mm, v(-282.43, 154.26) * mm, v(-282.58, 152.48) * mm]});
            skFitSpline(sketch, "E287", {"points": [v(-282.58, 152.48) * mm, v(-282.96, 147.66) * mm, v(-282.57, 146.73) * mm, v(-278.72, 143.2) * mm]});
            skFitSpline(sketch, "E288", {"points": [v(-278.72, 143.2) * mm, v(-273.16, 138.1) * mm, v(-271.51, 139.23) * mm, v(-271.3, 148.26) * mm]});
            skFitSpline(sketch, "E289", {"points": [v(-271.3, 148.26) * mm, v(-271.19, 152.88) * mm, v(-270.37, 156.51) * mm, v(-269, 158.46) * mm]});
            skFitSpline(sketch, "E290", {"points": [v(-269, 158.46) * mm, v(-266.2, 162.44) * mm, v(-266.3, 166.56) * mm, v(-269.32, 170.39) * mm]});
            skFitSpline(sketch, "E291", {"points": [v(-269.32, 170.39) * mm, v(-271.2, 172.77) * mm, v(-271.45, 173.9) * mm, v(-270.4, 175.16) * mm]});
            skFitSpline(sketch, "E292", {"points": [v(-270.4, 175.16) * mm, v(-269.64, 176.08) * mm, v(-269.43, 176.82) * mm, v(-269.93, 176.82) * mm]});
            skFitSpline(sketch, "E293", {"points": [v(-269.93, 176.82) * mm, v(-270.43, 176.82) * mm, v(-270.18, 177.61) * mm, v(-269.38, 178.58) * mm]});
            skFitSpline(sketch, "E294", {"points": [v(-269.38, 178.58) * mm, v(-268.39, 179.77) * mm, v(-268.3, 181.04) * mm, v(-269.1, 182.55) * mm]});
            skFitSpline(sketch, "E295", {"points": [v(-269.1, 182.55) * mm, v(-269.94, 184.12) * mm, v(-269.7, 186.02) * mm, v(-268.26, 189.05) * mm]});
            skFitSpline(sketch, "E296", {"points": [v(-268.26, 189.05) * mm, v(-266.35, 193.09) * mm, v(-265.89, 193.33) * mm, v(-259.9, 193.46) * mm]});
            skFitSpline(sketch, "E297", {"points": [v(-259.9, 193.46) * mm, v(-254.65, 193.58) * mm, v(-253.15, 193.1) * mm, v(-251.03, 190.67) * mm]});
            skFitSpline(sketch, "E298", {"points": [v(-251.03, 190.67) * mm, v(-249.63, 189.06) * mm, v(-247.12, 187.22) * mm, v(-245.45, 186.6) * mm]});
            skFitSpline(sketch, "E299", {"points": [v(-245.45, 186.6) * mm, v(-242.49, 185.46) * mm, v(-241.53, 183.02) * mm, v(-243.34, 181.2) * mm]});
            skFitSpline(sketch, "E300", {"points": [v(-243.34, 181.2) * mm, v(-245.78, 178.76) * mm, v(-241.8, 172.62) * mm, v(-239.12, 174.68) * mm]});
            skFitSpline(sketch, "E301", {"points": [v(-239.12, 174.68) * mm, v(-238.3, 175.3) * mm, v(-237.07, 175.46) * mm, v(-236.37, 175.02) * mm]});
            skFitSpline(sketch, "E302", {"points": [v(-236.37, 175.02) * mm, v(-235.66, 174.59) * mm, v(-233.53, 175.94) * mm, v(-231.62, 178.03) * mm]});
            skFitSpline(sketch, "E303", {"points": [v(-231.62, 178.03) * mm, v(-227.75, 182.27) * mm, v(-226, 181.5) * mm, v(-224.83, 175.08) * mm]});
            skFitSpline(sketch, "E304", {"points": [v(-224.83, 175.08) * mm, v(-224.48, 173.16) * mm, v(-222.93, 170.25) * mm, v(-221.4, 168.6) * mm]});
            skFitSpline(sketch, "E305", {"points": [v(-221.4, 168.6) * mm, v(-219.85, 166.97) * mm, v(-218.84, 165.53) * mm, v(-219.13, 165.42) * mm]});
            skFitSpline(sketch, "E306", {"points": [v(-219.13, 165.42) * mm, v(-219.43, 165.3) * mm, v(-219.03, 164.11) * mm, v(-218.25, 162.77) * mm]});
            skFitSpline(sketch, "E307", {"points": [v(-218.25, 162.77) * mm, v(-217.47, 161.42) * mm, v(-216.82, 160.77) * mm, v(-216.8, 161.32) * mm]});
            skFitSpline(sketch, "E308", {"points": [v(-216.8, 161.32) * mm, v(-216.78, 161.87) * mm, v(-215.25, 161.28) * mm, v(-213.4, 160) * mm]});
            skFitSpline(sketch, "E309", {"points": [v(-213.4, 160) * mm, v(-211.55, 158.71) * mm, v(-209.04, 157.3) * mm, v(-207.82, 156.86) * mm]});
            skFitSpline(sketch, "E310", {"points": [v(-207.82, 156.86) * mm, v(-204.83, 155.78) * mm, v(-206.12, 154.08) * mm, v(-210.62, 153.18) * mm]});
            skFitSpline(sketch, "E311", {"points": [v(-210.62, 153.18) * mm, v(-212.65, 152.77) * mm, v(-214.32, 151.94) * mm, v(-214.32, 151.33) * mm]});
            skFitSpline(sketch, "E312", {"points": [v(-214.32, 151.33) * mm, v(-214.32, 150.72) * mm, v(-212.25, 150.94) * mm, v(-209.73, 151.8) * mm]});
            skFitSpline(sketch, "E313", {"points": [v(-209.73, 151.8) * mm, v(-204.04, 153.78) * mm, v(-201.48, 152.04) * mm, v(-201.48, 146.18) * mm]});
            skFitSpline(sketch, "E314", {"points": [v(-201.48, 146.18) * mm, v(-201.48, 143.9) * mm, v(-202.25, 141.89) * mm, v(-203.32, 141.37) * mm]});
            skFitSpline(sketch, "E315", {"points": [v(-203.32, 141.37) * mm, v(-208.79, 138.72) * mm, v(-214.74, 137.3) * mm, v(-223.7, 136.48) * mm]});
            skFitSpline(sketch, "E316", {"points": [v(-223.7, 136.48) * mm, v(-233.84, 135.55) * mm, v(-237.67, 133.87) * mm, v(-242.92, 128.07) * mm]});
            skFitSpline(sketch, "E317", {"points": [v(-242.92, 128.07) * mm, v(-246.26, 124.38) * mm, v(-243.8, 124.88) * mm, v(-239.81, 128.7) * mm]});
            skFitSpline(sketch, "E318", {"points": [v(-239.81, 128.7) * mm, v(-235.49, 132.85) * mm, v(-227.15, 133.59) * mm, v(-227.15, 129.82) * mm]});
            skFitSpline(sketch, "E319", {"points": [v(-227.15, 129.82) * mm, v(-227.15, 128.47) * mm, v(-228.2, 127.14) * mm, v(-229.6, 126.77) * mm]});
            skFitSpline(sketch, "E320", {"points": [v(-229.6, 126.77) * mm, v(-231.99, 126.11) * mm, v(-231.98, 126.05) * mm, v(-229.31, 123.42) * mm]});
            skFitSpline(sketch, "E321", {"points": [v(-229.31, 123.42) * mm, v(-227.82, 121.95) * mm, v(-226.27, 121.27) * mm, v(-225.87, 121.92) * mm]});
            skFitSpline(sketch, "E322", {"points": [v(-225.87, 121.92) * mm, v(-225.47, 122.56) * mm, v(-224.62, 122.76) * mm, v(-223.99, 122.37) * mm]});
            skFitSpline(sketch, "E323", {"points": [v(-223.99, 122.37) * mm, v(-223.35, 121.98) * mm, v(-223.12, 121.18) * mm, v(-223.48, 120.6) * mm]});
            skFitSpline(sketch, "E324", {"points": [v(-223.48, 120.6) * mm, v(-225.14, 117.92) * mm, v(-221.34, 118.36) * mm, v(-218.76, 121.15) * mm]});
            skFitSpline(sketch, "E325", {"points": [v(-218.76, 121.15) * mm, v(-216.26, 123.84) * mm, v(-215.64, 124.03) * mm, v(-214.37, 122.5) * mm]});
            skFitSpline(sketch, "E326", {"points": [v(-214.37, 122.5) * mm, v(-212.76, 120.56) * mm, v(-213.75, 117.67) * mm, v(-215.62, 118.82) * mm]});
            skFitSpline(sketch, "E327", {"points": [v(-215.62, 118.82) * mm, v(-216.25, 119.2) * mm, v(-216.76, 118.93) * mm, v(-216.76, 118.2) * mm]});
            skFitSpline(sketch, "E328", {"points": [v(-216.76, 118.2) * mm, v(-216.76, 117.49) * mm, v(-218.82, 115.96) * mm, v(-221.34, 114.83) * mm]});
            skFitSpline(sketch, "E329", {"points": [v(-221.34, 114.83) * mm, v(-223.86, 113.69) * mm, v(-227.15, 111.7) * mm, v(-228.64, 110.39) * mm]});
            skFitSpline(sketch, "E330", {"points": [v(-228.64, 110.39) * mm, v(-231.14, 108.2) * mm, v(-231.43, 108.18) * mm, v(-232.15, 110.07) * mm]});
            skFitSpline(sketch, "E331", {"points": [v(-232.15, 110.07) * mm, v(-232.62, 111.28) * mm, v(-232.05, 113.13) * mm, v(-230.77, 114.54) * mm]});
            skFitSpline(sketch, "E332", {"points": [v(-230.77, 114.54) * mm, v(-228.02, 117.57) * mm, v(-229.07, 117.56) * mm, v(-235.1, 114.5) * mm]});
            skFitSpline(sketch, "E333", {"points": [v(-235.1, 114.5) * mm, v(-237.73, 113.15) * mm, v(-240.74, 112.05) * mm, v(-241.8, 112.05) * mm]});
            skFitSpline(sketch, "E334", {"points": [v(-241.8, 112.05) * mm, v(-244.6, 112.05) * mm, v(-246.86, 106.5) * mm, v(-244.97, 104.22) * mm]});
            skFitSpline(sketch, "E335", {"points": [v(-244.97, 104.22) * mm, v(-243.77, 102.78) * mm, v(-243.96, 102.19) * mm, v(-245.93, 101.13) * mm]});
            skFitSpline(sketch, "E336", {"points": [v(-245.93, 101.13) * mm, v(-247.28, 100.41) * mm, v(-249.45, 99.82) * mm, v(-250.76, 99.82) * mm]});
            skFitSpline(sketch, "E337", {"points": [v(-250.76, 99.82) * mm, v(-253.27, 99.82) * mm, v(-256.9, 95.26) * mm, v(-258.17, 90.48) * mm]});
            skFitSpline(sketch, "E338", {"points": [v(-258.17, 90.48) * mm, v(-259.21, 86.58) * mm, v(-261.09, 86.37) * mm, v(-262.11, 90.05) * mm]});
            skFitSpline(sketch, "E339", {"points": [v(-262.11, 90.05) * mm, v(-262.96, 93.1) * mm, v(-262.96, 93.1) * mm, v(-263.08, 89.66) * mm]});
            skFitSpline(sketch, "E340", {"points": [v(-263.08, 89.66) * mm, v(-263.15, 87.77) * mm, v(-262.65, 85.19) * mm, v(-261.98, 83.93) * mm]});
            skFitSpline(sketch, "E341", {"points": [v(-261.98, 83.93) * mm, v(-261.16, 82.39) * mm, v(-261.16, 81.39) * mm, v(-262, 80.87) * mm]});
            skFitSpline(sketch, "E342", {"points": [v(-262, 80.87) * mm, v(-262.68, 80.44) * mm, v(-262.95, 79.62) * mm, v(-262.59, 79.04) * mm]});
            skFitSpline(sketch, "E343", {"points": [v(-262.59, 79.04) * mm, v(-262.23, 78.45) * mm, v(-262.9, 77.4) * mm, v(-264.1, 76.71) * mm]});
            skFitSpline(sketch, "E344", {"points": [v(-264.1, 76.71) * mm, v(-265.29, 76.02) * mm, v(-265.85, 75.44) * mm, v(-265.34, 75.42) * mm]});
            skFitSpline(sketch, "E345", {"points": [v(-265.34, 75.42) * mm, v(-264.84, 75.4) * mm, v(-267.45, 72.38) * mm, v(-271.15, 68.7) * mm]});
            skFitSpline(sketch, "E346", {"points": [v(-271.15, 68.7) * mm, v(-274.85, 65.04) * mm, v(-277.87, 61.36) * mm, v(-277.87, 60.54) * mm]});
            skFitSpline(sketch, "E347", {"points": [v(-277.87, 60.54) * mm, v(-277.87, 59.71) * mm, v(-276.73, 54.97) * mm, v(-275.33, 50) * mm]});
            skFitSpline(sketch, "E348", {"points": [v(-275.33, 50) * mm, v(-272.72, 40.68) * mm, v(-272.85, 37.49) * mm, v(-275.86, 37.49) * mm]});
            skFitSpline(sketch, "E349", {"points": [v(-275.86, 37.49) * mm, v(-278.06, 37.49) * mm, v(-281.9, 43.28) * mm, v(-282.33, 47.25) * mm]});
            skFitSpline(sketch, "E350", {"points": [v(-282.33, 47.25) * mm, v(-282.9, 52.62) * mm, v(-285.29, 55.7) * mm, v(-288.74, 55.55) * mm]});
            skFitSpline(sketch, "E351", {"points": [v(-288.74, 55.55) * mm, v(-290.5, 55.47) * mm, v(-293.3, 55.78) * mm, v(-294.98, 56.24) * mm]});
            skFitSpline(sketch, "E352", {"points": [v(-294.98, 56.24) * mm, v(-299.14, 57.37) * mm, v(-302.1, 55.45) * mm, v(-300.04, 52.97) * mm]});
            skFitSpline(sketch, "E353", {"points": [v(-300.04, 52.97) * mm, v(-297.82, 50.3) * mm, v(-299.76, 49.76) * mm, v(-306.61, 51.16) * mm]});
            skFitSpline(sketch, "E354", {"points": [v(-306.61, 51.16) * mm, v(-316.4, 53.16) * mm, v(-317.39, 53.11) * mm, v(-321.6, 50.43) * mm]});
            skFitSpline(sketch, "E355", {"points": [v(-321.6, 50.43) * mm, v(-324.93, 48.31) * mm, v(-325.56, 47.21) * mm, v(-325.3, 43.97) * mm]});
            skFitSpline(sketch, "E356", {"points": [v(-325.3, 43.97) * mm, v(-325.14, 41.82) * mm, v(-325.4, 39.67) * mm, v(-325.88, 39.18) * mm]});
            skFitSpline(sketch, "E357", {"points": [v(-325.88, 39.18) * mm, v(-327.66, 37.4) * mm, v(-326.7, 26.82) * mm, v(-324.3, 21.87) * mm]});
            skFitSpline(sketch, "E358", {"points": [v(-324.3, 21.87) * mm, v(-321.27, 15.58) * mm, v(-318.9, 14.24) * mm, v(-312.33, 15.12) * mm]});
            skFitSpline(sketch, "E359", {"points": [v(-312.33, 15.12) * mm, v(-307.72, 15.74) * mm, v(-307.2, 16.15) * mm, v(-307.2, 19.17) * mm]});
            skFitSpline(sketch, "E360", {"points": [v(-307.2, 19.17) * mm, v(-307.2, 23.5) * mm, v(-304.61, 25.57) * mm, v(-298.93, 25.74) * mm]});
            skFitSpline(sketch, "E361", {"points": [v(-298.93, 25.74) * mm, v(-297.41, 25.79) * mm, v(-295.9, 25.83) * mm, v(-294.37, 25.88) * mm]});
            skFitSpline(sketch, "E362", {"points": [v(-294.37, 25.88) * mm, v(-294.51, 24.04) * mm, v(-294.65, 22.21) * mm, v(-294.79, 20.38) * mm]});
            skFitSpline(sketch, "E363", {"points": [v(-294.79, 20.38) * mm, v(-295.02, 17.35) * mm, v(-295.63, 14.33) * mm, v(-296.15, 13.66) * mm]});
            skFitSpline(sketch, "E364", {"points": [v(-296.15, 13.66) * mm, v(-296.67, 12.98) * mm, v(-297.47, 10.85) * mm, v(-297.93, 8.92) * mm]});
            skFitSpline(sketch, "E365", {"points": [v(-297.93, 8.92) * mm, v(-298.74, 5.53) * mm, v(-298.64, 5.43) * mm, v(-294.78, 6) * mm]});
            skFitSpline(sketch, "E366", {"points": [v(-294.78, 6) * mm, v(-292.58, 6.32) * mm, v(-288.97, 5.83) * mm, v(-286.74, 4.9) * mm]});
            skFitSpline(sketch, "E367", {"points": [v(-286.74, 4.9) * mm, v(-285.4, 4.33) * mm, v(-284.05, 3.77) * mm, v(-282.7, 3.2) * mm]});
            skFitSpline(sketch, "E368", {"points": [v(-282.7, 3.2) * mm, v(-282.95, 0.67) * mm, v(-283.21, -1.87) * mm, v(-283.47, -4.4) * mm]});
            skFitSpline(sketch, "E369", {"points": [v(-283.47, -4.4) * mm, v(-284.13, -10.96) * mm, v(-283.89, -12.45) * mm, v(-281.7, -15.21) * mm]});
            skFitSpline(sketch, "E370", {"points": [v(-281.7, -15.21) * mm, v(-279.34, -18.2) * mm, v(-278.84, -18.33) * mm, v(-274.27, -17.1) * mm]});
            skFitSpline(sketch, "E371", {"points": [v(-274.27, -17.1) * mm, v(-269.88, -15.93) * mm, v(-269.08, -16.08) * mm, v(-266.41, -18.6) * mm]});
            skFitSpline(sketch, "E372", {"points": [v(-266.41, -18.6) * mm, v(-265.42, -19.52) * mm, v(-264.43, -20.45) * mm, v(-263.44, -21.38) * mm]});
            skFitSpline(sketch, "E373", {"points": [v(-263.44, -21.38) * mm, v(-263.17, -20.15) * mm, v(-262.9, -18.93) * mm, v(-262.63, -17.7) * mm]});
            skFitSpline(sketch, "E374", {"points": [v(-262.63, -17.7) * mm, v(-261.78, -13.83) * mm, v(-258.82, -10.49) * mm, v(-257.45, -11.86) * mm]});
            skFitSpline(sketch, "E375", {"points": [v(-257.45, -11.86) * mm, v(-257.01, -12.3) * mm, v(-255.15, -11.22) * mm, v(-253.3, -9.45) * mm]});
            skFitSpline(sketch, "E376", {"points": [v(-253.3, -9.45) * mm, v(-251.41, -7.64) * mm, v(-249.34, -6.63) * mm, v(-248.53, -7.13) * mm]});
            skFitSpline(sketch, "E377", {"points": [v(-248.53, -7.13) * mm, v(-247.5, -7.76) * mm, v(-247.47, -8.38) * mm, v(-248.43, -9.34) * mm]});
            skFitSpline(sketch, "E378", {"points": [v(-248.43, -9.34) * mm, v(-250.3, -11.21) * mm, v(-250.08, -12.67) * mm, v(-248.05, -11.89) * mm]});
            skFitSpline(sketch, "E379", {"points": [v(-248.05, -11.89) * mm, v(-247.1, -11.53) * mm, v(-246, -10.03) * mm, v(-245.58, -8.57) * mm]});
            skFitSpline(sketch, "E380", {"points": [v(-245.58, -8.57) * mm, v(-244.92, -6.21) * mm, v(-244.65, -6.12) * mm, v(-243.32, -7.8) * mm]});
            skFitSpline(sketch, "E381", {"points": [v(-243.32, -7.8) * mm, v(-241.6, -9.99) * mm, v(-237.62, -11.9) * mm, v(-235.5, -11.56) * mm]});
            skFitSpline(sketch, "E382", {"points": [v(-235.5, -11.56) * mm, v(-234.7, -11.44) * mm, v(-233.7, -11.9) * mm, v(-233.28, -12.6) * mm]});
            skFitSpline(sketch, "E383", {"points": [v(-233.28, -12.6) * mm, v(-232.85, -13.28) * mm, v(-231.37, -13.85) * mm, v(-229.98, -13.85) * mm]});
            skFitSpline(sketch, "E384", {"points": [v(-229.98, -13.85) * mm, v(-227.88, -13.85) * mm, v(-227.71, -13.54) * mm, v(-228.98, -12.01) * mm]});
            skFitSpline(sketch, "E385", {"points": [v(-228.98, -12.01) * mm, v(-229.82, -11) * mm, v(-230.16, -10.18) * mm, v(-229.74, -10.18) * mm]});
            skFitSpline(sketch, "E386", {"points": [v(-229.74, -10.18) * mm, v(-229.32, -10.18) * mm, v(-228.7, -10.18) * mm, v(-228.37, -10.18) * mm]});
            skFitSpline(sketch, "E387", {"points": [v(-228.37, -10.18) * mm, v(-228.04, -10.18) * mm, v(-227.9, -10.6) * mm, v(-228.07, -11.1) * mm]});
            skFitSpline(sketch, "E388", {"points": [v(-228.07, -11.1) * mm, v(-228.23, -11.6) * mm, v(-226.45, -12.3) * mm, v(-224.1, -12.66) * mm]});
            skFitSpline(sketch, "E389", {"points": [v(-224.1, -12.66) * mm, v(-221.74, -13.02) * mm, v(-219.93, -13.91) * mm, v(-220.07, -14.64) * mm]});
            skFitSpline(sketch, "E390", {"points": [v(-220.07, -14.64) * mm, v(-220.2, -15.37) * mm, v(-219.2, -17) * mm, v(-217.82, -18.27) * mm]});
            skFitSpline(sketch, "E391", {"points": [v(-217.82, -18.27) * mm, v(-216.44, -19.53) * mm, v(-213.3, -22.63) * mm, v(-210.82, -25.15) * mm]});
            skFitSpline(sketch, "E392", {"points": [v(-210.82, -25.15) * mm, v(-207.3, -28.73) * mm, v(-205.37, -29.73) * mm, v(-202, -29.73) * mm]});
            skFitSpline(sketch, "E393", {"points": [v(-202, -29.73) * mm, v(-196.72, -29.73) * mm, v(-190.03, -34.36) * mm, v(-187.86, -39.5) * mm]});
            skFitSpline(sketch, "E394", {"points": [v(-187.86, -39.5) * mm, v(-187.02, -41.53) * mm, v(-186.65, -43.18) * mm, v(-187.06, -43.18) * mm]});
            skFitSpline(sketch, "E395", {"points": [v(-187.06, -43.18) * mm, v(-187.47, -43.18) * mm, v(-186.8, -44.28) * mm, v(-185.6, -45.62) * mm]});
            skFitSpline(sketch, "E396", {"points": [v(-185.6, -45.62) * mm, v(-184.38, -46.97) * mm, v(-183.74, -48.14) * mm, v(-184.18, -48.22) * mm]});
            skFitSpline(sketch, "E397", {"points": [v(-184.18, -48.22) * mm, v(-184.62, -48.3) * mm, v(-185.5, -48.44) * mm, v(-186.15, -48.53) * mm]});
            skFitSpline(sketch, "E398", {"points": [v(-186.15, -48.53) * mm, v(-187.45, -48.7) * mm, v(-191, -53.03) * mm, v(-191.05, -54.52) * mm]});
            skFitSpline(sketch, "E399", {"points": [v(-191.05, -54.52) * mm, v(-191.07, -55.05) * mm, v(-189.44, -54.25) * mm, v(-187.42, -52.76) * mm]});
            skFitSpline(sketch, "E400", {"points": [v(-187.42, -52.76) * mm, v(-184.52, -50.62) * mm, v(-183.42, -50.36) * mm, v(-182.25, -51.53) * mm]});
            skFitSpline(sketch, "E401", {"points": [v(-182.25, -51.53) * mm, v(-180.26, -53.52) * mm, v(-182.38, -56.9) * mm, v(-186.32, -58) * mm]});
            skFitSpline(sketch, "E402", {"points": [v(-186.32, -58) * mm, v(-189.2, -58.81) * mm, v(-189.2, -58.83) * mm, v(-185.93, -58.95) * mm]});
            skFitSpline(sketch, "E403", {"points": [v(-185.93, -58.95) * mm, v(-183.64, -59.03) * mm, v(-181.97, -58.11) * mm, v(-180.6, -56.01) * mm]});
            skFitSpline(sketch, "E404", {"points": [v(-180.6, -56.01) * mm, v(-177.92, -51.93) * mm, v(-175.08, -52.16) * mm, v(-170.14, -56.86) * mm]});
            skFitSpline(sketch, "E405", {"points": [v(-170.14, -56.86) * mm, v(-166.62, -60.2) * mm, v(-164.95, -60.83) * mm, v(-158.36, -61.28) * mm]});
            skFitSpline(sketch, "E406", {"points": [v(-158.36, -61.28) * mm, v(-152.64, -61.67) * mm, v(-150.4, -62.35) * mm, v(-149.53, -63.96) * mm]});
            skFitSpline(sketch, "E407", {"points": [v(-149.53, -63.96) * mm, v(-148.9, -65.15) * mm, v(-146.44, -67.27) * mm, v(-144.07, -68.67) * mm]});
            skFitSpline(sketch, "E408", {"points": [v(-144.07, -68.67) * mm, v(-140.3, -70.89) * mm, v(-139.76, -71.81) * mm, v(-139.76, -76) * mm]});
            skFitSpline(sketch, "E409", {"points": [v(-139.76, -76) * mm, v(-139.76, -79.49) * mm, v(-140.96, -82.58) * mm, v(-144.18, -87.35) * mm]});
            skFitSpline(sketch, "E410", {"points": [v(-144.18, -87.35) * mm, v(-146.61, -90.95) * mm, v(-149.3, -94.47) * mm, v(-150.16, -95.16) * mm]});
            skFitSpline(sketch, "E411", {"points": [v(-150.16, -95.16) * mm, v(-151.13, -95.95) * mm, v(-151.9, -100.53) * mm, v(-152.22, -107.39) * mm]});
            skFitSpline(sketch, "E412", {"points": [v(-152.22, -107.39) * mm, v(-152.63, -116.45) * mm, v(-153.34, -119.6) * mm, v(-156.32, -125.6) * mm]});
            skFitSpline(sketch, "E413", {"points": [v(-156.32, -125.6) * mm, v(-159.72, -132.41) * mm, v(-160.21, -132.86) * mm, v(-164.8, -133.3) * mm]});
            skFitSpline(sketch, "E414", {"points": [v(-164.8, -133.3) * mm, v(-167.48, -133.55) * mm, v(-170.12, -134.55) * mm, v(-170.67, -135.52) * mm]});
            skFitSpline(sketch, "E415", {"points": [v(-170.67, -135.52) * mm, v(-171.21, -136.5) * mm, v(-172.2, -137.3) * mm, v(-172.87, -137.3) * mm]});
            skFitSpline(sketch, "E416", {"points": [v(-172.87, -137.3) * mm, v(-174.2, -137.3) * mm, v(-181.47, -142.16) * mm, v(-182.73, -143.9) * mm]});
            skFitSpline(sketch, "E417", {"points": [v(-182.73, -143.9) * mm, v(-183.17, -144.51) * mm, v(-182.97, -146.25) * mm, v(-182.28, -147.76) * mm]});
            skFitSpline(sketch, "E418", {"points": [v(-182.28, -147.76) * mm, v(-181.28, -149.95) * mm, v(-181.7, -151.83) * mm, v(-184.3, -157.04) * mm]});
            skFitSpline(sketch, "E419", {"points": [v(-184.3, -157.04) * mm, v(-192.98, -174.31) * mm, v(-198.08, -179.58) * mm, v(-204.9, -178.3) * mm]});
            skFitSpline(sketch, "E420", {"points": [v(-204.9, -178.3) * mm, v(-208.2, -177.69) * mm, v(-208.26, -177.75) * mm, v(-206.43, -180.36) * mm]});
            skFitSpline(sketch, "E421", {"points": [v(-206.43, -180.36) * mm, v(-202.14, -186.49) * mm, v(-205.74, -191.49) * mm, v(-215.36, -192.76) * mm]});
            skFitSpline(sketch, "E422", {"points": [v(-215.36, -192.76) * mm, v(-220.3, -193.42) * mm, v(-221.65, -194.07) * mm, v(-221.65, -195.81) * mm]});
            skFitSpline(sketch, "E423", {"points": [v(-221.65, -195.81) * mm, v(-221.65, -199.1) * mm, v(-225.55, -202.1) * mm, v(-228.74, -201.27) * mm]});
            skFitSpline(sketch, "E424", {"points": [v(-228.74, -201.27) * mm, v(-231.01, -200.67) * mm, v(-231.32, -200.93) * mm, v(-230.6, -202.84) * mm]});
            skFitSpline(sketch, "E425", {"points": [v(-230.6, -202.84) * mm, v(-230.13, -204.1) * mm, v(-228.89, -205.8) * mm, v(-227.84, -206.63) * mm]});
            skFitSpline(sketch, "E426", {"points": [v(-227.84, -206.63) * mm, v(-226.15, -207.96) * mm, v(-226.25, -208.23) * mm, v(-228.68, -208.92) * mm]});
            skFitSpline(sketch, "E427", {"points": [v(-228.68, -208.92) * mm, v(-230.72, -209.5) * mm, v(-231.43, -210.6) * mm, v(-231.43, -213.24) * mm]});
            skFitSpline(sketch, "E428", {"points": [v(-231.43, -213.24) * mm, v(-231.43, -215.91) * mm, v(-232.19, -217.09) * mm, v(-234.48, -217.96) * mm]});
            skFitSpline(sketch, "E429", {"points": [v(-234.48, -217.96) * mm, v(-236.16, -218.6) * mm, v(-237.54, -219.92) * mm, v(-237.54, -220.89) * mm]});
            skFitSpline(sketch, "E430", {"points": [v(-237.54, -220.89) * mm, v(-237.54, -223.94) * mm, v(-236.11, -226.52) * mm, v(-234.42, -226.52) * mm]});
            skFitSpline(sketch, "E431", {"points": [v(-234.42, -226.52) * mm, v(-231.2, -226.52) * mm, v(-231.43, -228.88) * mm, v(-235.04, -232.99) * mm]});
            skFitSpline(sketch, "E432", {"points": [v(-235.04, -232.99) * mm, v(-237.06, -235.29) * mm, v(-238.44, -237.43) * mm, v(-238.11, -237.76) * mm]});
            skFitSpline(sketch, "E433", {"points": [v(-238.11, -237.76) * mm, v(-237.79, -238.08) * mm, v(-238.63, -239.34) * mm, v(-239.98, -240.57) * mm]});
            skFitSpline(sketch, "E434", {"points": [v(-239.98, -240.57) * mm, v(-241.32, -241.78) * mm, v(-242.43, -244.1) * mm, v(-242.43, -245.69) * mm]});
            skFitSpline(sketch, "E435", {"points": [v(-242.43, -245.69) * mm, v(-242.43, -247.29) * mm, v(-243.25, -248.9) * mm, v(-244.26, -249.3) * mm]});
            skFitSpline(sketch, "E436", {"points": [v(-244.26, -249.3) * mm, v(-245.27, -249.68) * mm, v(-246.1, -250.47) * mm, v(-246.1, -251.05) * mm]});
            skFitSpline(sketch, "E437", {"points": [v(-246.1, -251.05) * mm, v(-246.1, -251.63) * mm, v(-245.31, -251.8) * mm, v(-244.35, -251.44) * mm]});
            skFitSpline(sketch, "E438", {"points": [v(-244.35, -251.44) * mm, v(-243.34, -251.05) * mm, v(-240.57, -252.82) * mm, v(-237.71, -255.67) * mm]});
            skFitSpline(sketch, "E439", {"points": [v(-237.71, -255.67) * mm, v(-233.43, -259.96) * mm, v(-233.05, -260.77) * mm, v(-234.69, -262.13) * mm]});
            skFitSpline(sketch, "E440", {"points": [v(-234.69, -262.13) * mm, v(-237.05, -264.1) * mm, v(-239.77, -264.52) * mm, v(-240.66, -263.07) * mm]});
            skFitSpline(sketch, "E441", {"points": [v(-429.43, 224.5) * mm, v(-428.42, 225.14) * mm, v(-428.15, 225.68) * mm, v(-428.82, 225.68) * mm]});
            skFitSpline(sketch, "E442", {"points": [v(-428.82, 225.68) * mm, v(-429.5, 225.68) * mm, v(-430.87, 225.14) * mm, v(-431.87, 224.5) * mm]});
            skFitSpline(sketch, "E443", {"points": [v(-431.87, 224.5) * mm, v(-432.88, 223.84) * mm, v(-433.16, 223.3) * mm, v(-432.49, 223.3) * mm]});
            skFitSpline(sketch, "E444", {"points": [v(-432.49, 223.3) * mm, v(-431.81, 223.3) * mm, v(-430.44, 223.84) * mm, v(-429.43, 224.5) * mm]});
            skFitSpline(sketch, "E445", {"points": [v(-255.87, -256.53) * mm, v(-255.87, -256.16) * mm, v(-255.73, -255.6) * mm, v(-255.57, -255.3) * mm]});
            skFitSpline(sketch, "E446", {"points": [v(-255.57, -255.3) * mm, v(-255.4, -254.98) * mm, v(-256.3, -253.97) * mm, v(-257.58, -253.03) * mm]});
            skFitSpline(sketch, "E447", {"points": [v(-257.58, -253.03) * mm, v(-259.3, -251.77) * mm, v(-259.52, -251.1) * mm, v(-258.4, -250.4) * mm]});
            skFitSpline(sketch, "E448", {"points": [v(-258.4, -250.4) * mm, v(-257.56, -249.88) * mm, v(-256.27, -250.07) * mm, v(-255.52, -250.82) * mm]});
            skFitSpline(sketch, "E449", {"points": [v(-255.52, -250.82) * mm, v(-254.77, -251.57) * mm, v(-254.61, -252.18) * mm, v(-255.17, -252.18) * mm]});
            skFitSpline(sketch, "E450", {"points": [v(-255.17, -252.18) * mm, v(-255.72, -252.18) * mm, v(-255.53, -252.96) * mm, v(-254.74, -253.9) * mm]});
            skFitSpline(sketch, "E451", {"points": [v(-254.74, -253.9) * mm, v(-253.76, -255.09) * mm, v(-253.71, -255.88) * mm, v(-254.59, -256.42) * mm]});
            skFitSpline(sketch, "E452", {"points": [v(-254.59, -256.42) * mm, v(-255.3, -256.86) * mm, v(-255.87, -256.9) * mm, v(-255.87, -256.53) * mm]});
            skFitSpline(sketch, "E453", {"points": [v(468.6, -226.41) * mm, v(467.42, -225.72) * mm, v(465.95, -225.48) * mm, v(465.33, -225.86) * mm]});
            skFitSpline(sketch, "E454", {"points": [v(465.33, -225.86) * mm, v(464.7, -226.24) * mm, v(463.85, -226) * mm, v(463.43, -225.31) * mm]});
            skFitSpline(sketch, "E455", {"points": [v(463.43, -225.31) * mm, v(462.47, -223.76) * mm, v(469.55, -213.74) * mm, v(473.4, -211.22) * mm]});
            skFitSpline(sketch, "E456", {"points": [v(473.4, -211.22) * mm, v(474.97, -210.19) * mm, v(476.25, -208.7) * mm, v(476.25, -207.93) * mm]});
            skFitSpline(sketch, "E457", {"points": [v(476.25, -207.93) * mm, v(476.25, -207.15) * mm, v(477.43, -205.25) * mm, v(478.86, -203.72) * mm]});
            skFitSpline(sketch, "E458", {"points": [v(478.86, -203.72) * mm, v(480.9, -201.55) * mm, v(481.98, -201.21) * mm, v(483.75, -202.16) * mm]});
            skFitSpline(sketch, "E459", {"points": [v(483.75, -202.16) * mm, v(486.48, -203.62) * mm, v(486.77, -207.98) * mm, v(484.2, -208.96) * mm]});
            skFitSpline(sketch, "E460", {"points": [v(484.2, -208.96) * mm, v(483.2, -209.35) * mm, v(482.7, -210.18) * mm, v(483.1, -210.82) * mm]});
            skFitSpline(sketch, "E461", {"points": [v(483.1, -210.82) * mm, v(483.48, -211.45) * mm, v(482.38, -213.3) * mm, v(480.64, -214.9) * mm]});
            skFitSpline(sketch, "E462", {"points": [v(480.64, -214.9) * mm, v(477.91, -217.44) * mm, v(476.72, -220.43) * mm, v(477.78, -222.1) * mm]});
            skFitSpline(sketch, "E463", {"points": [v(477.78, -222.1) * mm, v(478.32, -222.97) * mm, v(473.47, -227.74) * mm, v(472.09, -227.7) * mm]});
            skFitSpline(sketch, "E464", {"points": [v(472.09, -227.7) * mm, v(471.35, -227.68) * mm, v(469.78, -227.1) * mm, v(468.6, -226.41) * mm]});
            skFitSpline(sketch, "E465", {"points": [v(400.77, -211.52) * mm, v(400.12, -210.7) * mm, v(399.2, -208.37) * mm, v(398.7, -206.35) * mm]});
            skFitSpline(sketch, "E466", {"points": [v(398.7, -206.35) * mm, v(398.22, -204.33) * mm, v(397.74, -202.4) * mm, v(397.62, -202.07) * mm]});
            skFitSpline(sketch, "E467", {"points": [v(397.62, -202.07) * mm, v(397.5, -201.73) * mm, v(399.77, -201.43) * mm, v(402.65, -201.38) * mm]});
            skFitSpline(sketch, "E468", {"points": [v(402.65, -201.38) * mm, v(408.41, -201.3) * mm, v(411.05, -203.3) * mm, v(409.58, -206.64) * mm]});
            skFitSpline(sketch, "E469", {"points": [v(409.58, -206.64) * mm, v(409.06, -207.82) * mm, v(408.58, -209.16) * mm, v(408.52, -209.6) * mm]});
            skFitSpline(sketch, "E470", {"points": [v(408.52, -209.6) * mm, v(408.16, -212.41) * mm, v(402.56, -213.79) * mm, v(400.77, -211.52) * mm]});
            skFitSpline(sketch, "E471", {"points": [v(488.1, -203.73) * mm, v(488.1, -203.07) * mm, v(487.25, -201.94) * mm, v(487.25, -200.79) * mm]});
            skFitSpline(sketch, "E472", {"points": [v(487.25, -200.79) * mm, v(487.25, -199.63) * mm, v(486.11, -198.4) * mm, v(484.72, -198.03) * mm]});
            skFitSpline(sketch, "E473", {"points": [v(484.72, -198.03) * mm, v(482.3, -197.4) * mm, v(482.28, -197.22) * mm, v(484.2, -194.28) * mm]});
            skFitSpline(sketch, "E474", {"points": [v(484.2, -194.28) * mm, v(486.48, -190.82) * mm, v(485.9, -187.58) * mm, v(482.05, -182.12) * mm]});
            skFitSpline(sketch, "E475", {"points": [v(482.05, -182.12) * mm, v(480.42, -179.8) * mm, v(480.02, -178.26) * mm, v(480.85, -177.43) * mm]});
            skFitSpline(sketch, "E476", {"points": [v(480.85, -177.43) * mm, v(482.18, -176.1) * mm, v(488.47, -183.29) * mm, v(488.47, -186.14) * mm]});
            skFitSpline(sketch, "E477", {"points": [v(488.47, -186.14) * mm, v(488.47, -187.4) * mm, v(488.84, -187.4) * mm, v(490.37, -186.13) * mm]});
            skFitSpline(sketch, "E478", {"points": [v(490.37, -186.13) * mm, v(491.97, -184.8) * mm, v(492.37, -184.96) * mm, v(492.94, -187.12) * mm]});
            skFitSpline(sketch, "E479", {"points": [v(492.94, -187.12) * mm, v(493.31, -188.57) * mm, v(494.3, -189.42) * mm, v(495.2, -189.07) * mm]});
            skFitSpline(sketch, "E480", {"points": [v(495.2, -189.07) * mm, v(496.07, -188.73) * mm, v(497.12, -189) * mm, v(497.53, -189.66) * mm]});
            skFitSpline(sketch, "E481", {"points": [v(497.53, -189.66) * mm, v(498.47, -191.18) * mm, v(496.02, -197.8) * mm, v(494.93, -196.7) * mm]});
            skFitSpline(sketch, "E482", {"points": [v(494.93, -196.7) * mm, v(494.48, -196.26) * mm, v(493.54, -197.66) * mm, v(492.82, -199.8) * mm]});
            skFitSpline(sketch, "E483", {"points": [v(492.82, -199.8) * mm, v(491.52, -203.74) * mm, v(489.65, -205.29) * mm, v(488.1, -203.73) * mm]});
            skFitSpline(sketch, "E484", {"points": [v(488.1, -203.73) * mm, v(488.1, -203.73) * mm, v(488.1, -203.73) * mm, v(488.1, -203.73) * mm, v(488.1, -203.73) * mm]});
            skFitSpline(sketch, "E485", {"points": [v(400.05, -193.4) * mm, v(398.11, -191.14) * mm, v(397.62, -191.05) * mm, v(395.8, -192.62) * mm]});
            skFitSpline(sketch, "E486", {"points": [v(395.8, -192.62) * mm, v(392.5, -195.47) * mm, v(386.18, -193.12) * mm, v(384.16, -188.29) * mm]});
            skFitSpline(sketch, "E487", {"points": [v(384.16, -188.29) * mm, v(383.26, -186.12) * mm, v(381.64, -183.62) * mm, v(380.57, -182.73) * mm]});
            skFitSpline(sketch, "E488", {"points": [v(380.57, -182.73) * mm, v(379.44, -181.8) * mm, v(378.94, -180.25) * mm, v(379.39, -179.06) * mm]});
            skFitSpline(sketch, "E489", {"points": [v(379.39, -179.06) * mm, v(380.04, -177.32) * mm, v(379.86, -177.25) * mm, v(378.2, -178.6) * mm]});
            skFitSpline(sketch, "E490", {"points": [v(378.2, -178.6) * mm, v(375.67, -180.66) * mm, v(374.24, -178.53) * mm, v(375.97, -175.29) * mm]});
            skFitSpline(sketch, "E491", {"points": [v(375.97, -175.29) * mm, v(376.68, -173.97) * mm, v(377.23, -172.17) * mm, v(377.2, -171.29) * mm]});
            skFitSpline(sketch, "E492", {"points": [v(377.2, -171.29) * mm, v(377.17, -170.4) * mm, v(376.05, -171.74) * mm, v(374.72, -174.26) * mm]});
            skFitSpline(sketch, "E493", {"points": [v(374.72, -174.26) * mm, v(373.4, -176.79) * mm, v(371.8, -178.85) * mm, v(371.17, -178.85) * mm]});
            skFitSpline(sketch, "E494", {"points": [v(371.17, -178.85) * mm, v(370.54, -178.85) * mm, v(369.14, -176.96) * mm, v(368.04, -174.65) * mm]});
            skFitSpline(sketch, "E495", {"points": [v(368.04, -174.65) * mm, v(366.42, -171.23) * mm, v(364.85, -170.08) * mm, v(359.57, -168.42) * mm]});
            skFitSpline(sketch, "E496", {"points": [v(359.57, -168.42) * mm, v(354.64, -166.87) * mm, v(352.5, -166.7) * mm, v(350.59, -167.73) * mm]});
            skFitSpline(sketch, "E497", {"points": [v(350.59, -167.73) * mm, v(349.2, -168.47) * mm, v(346.45, -169.07) * mm, v(344.46, -169.07) * mm]});
            skFitSpline(sketch, "E498", {"points": [v(344.46, -169.07) * mm, v(342.2, -169.07) * mm, v(339.76, -170.2) * mm, v(337.96, -172.1) * mm]});
            skFitSpline(sketch, "E499", {"points": [v(337.96, -172.1) * mm, v(335.97, -174.2) * mm, v(333.76, -175.15) * mm, v(330.78, -175.16) * mm]});
            skFitSpline(sketch, "E500", {"points": [v(330.78, -175.16) * mm, v(328.2, -175.17) * mm, v(324.63, -176.44) * mm, v(321.87, -178.32) * mm]});
            skFitSpline(sketch, "E501", {"points": [v(321.87, -178.32) * mm, v(317.26, -181.45) * mm, v(317.25, -181.45) * mm, v(313.33, -179.16) * mm]});
            skFitSpline(sketch, "E502", {"points": [v(313.33, -179.16) * mm, v(310.14, -177.3) * mm, v(309.48, -176.2) * mm, v(309.75, -173.28) * mm]});
            skFitSpline(sketch, "E503", {"points": [v(309.75, -173.28) * mm, v(310.28, -167.6) * mm, v(306.86, -153.64) * mm, v(303.92, -149.52) * mm]});
            skFitSpline(sketch, "E504", {"points": [v(303.92, -149.52) * mm, v(302.3, -147.24) * mm, v(301.56, -144.94) * mm, v(302.06, -143.67) * mm]});
            skFitSpline(sketch, "E505", {"points": [v(302.06, -143.67) * mm, v(302.8, -141.74) * mm, v(303, -141.76) * mm, v(304.61, -143.94) * mm]});
            skFitSpline(sketch, "E506", {"points": [v(304.61, -143.94) * mm, v(306, -145.84) * mm, v(306.36, -145.93) * mm, v(306.36, -144.4) * mm]});
            skFitSpline(sketch, "E507", {"points": [v(306.36, -144.4) * mm, v(306.36, -143.34) * mm, v(305.53, -141.8) * mm, v(304.53, -140.96) * mm]});
            skFitSpline(sketch, "E508", {"points": [v(304.53, -140.96) * mm, v(303.52, -140.12) * mm, v(302.7, -137.9) * mm, v(302.7, -136.04) * mm]});
            skFitSpline(sketch, "E509", {"points": [v(302.7, -136.04) * mm, v(302.7, -133.43) * mm, v(303.75, -132) * mm, v(307.28, -129.86) * mm]});
            skFitSpline(sketch, "E510", {"points": [v(307.28, -129.86) * mm, v(313.99, -125.8) * mm, v(320.17, -122.62) * mm, v(321.4, -122.62) * mm]});
            skFitSpline(sketch, "E511", {"points": [v(321.4, -122.62) * mm, v(323.54, -122.62) * mm, v(329.73, -117.43) * mm, v(329.2, -116.07) * mm]});
            skFitSpline(sketch, "E512", {"points": [v(329.2, -116.07) * mm, v(328.92, -115.3) * mm, v(329.2, -113.3) * mm, v(329.83, -111.62) * mm]});
            skFitSpline(sketch, "E513", {"points": [v(329.83, -111.62) * mm, v(335.24, -114.17) * mm, v(332.23, -108.43) * mm, v(336.3, -106.52) * mm]});
            skFitSpline(sketch, "E514", {"points": [v(336.3, -106.52) * mm, v(337.87, -105.8) * mm, v(339.41, -104.22) * mm, v(339.73, -103) * mm]});
            skFitSpline(sketch, "E515", {"points": [v(339.73, -103) * mm, v(340.4, -100.46) * mm, v(344.33, -100.57) * mm, v(345.38, -103.17) * mm]});
            skFitSpline(sketch, "E516", {"points": [v(345.38, -103.17) * mm, v(345.77, -104.13) * mm, v(348, -105.06) * mm, v(350.34, -105.25) * mm]});
            skFitSpline(sketch, "E517", {"points": [v(350.34, -105.25) * mm, v(353.7, -105.53) * mm, v(354.29, -105.28) * mm, v(353.11, -104.1) * mm]});
            skFitSpline(sketch, "E518", {"points": [v(353.11, -104.1) * mm, v(351.93, -102.93) * mm, v(352.04, -102.14) * mm, v(353.62, -100.4) * mm]});
            skFitSpline(sketch, "E519", {"points": [v(353.62, -100.4) * mm, v(354.73, -99.18) * mm, v(355.2, -98.18) * mm, v(354.68, -98.18) * mm]});
            skFitSpline(sketch, "E520", {"points": [v(354.68, -98.18) * mm, v(354.16, -98.18) * mm, v(354.37, -97.4) * mm, v(355.16, -96.46) * mm]});
            skFitSpline(sketch, "E521", {"points": [v(355.16, -96.46) * mm, v(356.16, -95.26) * mm, v(356.2, -94.49) * mm, v(355.29, -93.93) * mm]});
            skFitSpline(sketch, "E522", {"points": [v(355.29, -93.93) * mm, v(354.57, -93.48) * mm, v(354.3, -92.6) * mm, v(354.7, -91.96) * mm]});
            skFitSpline(sketch, "E523", {"points": [v(354.7, -91.96) * mm, v(355.1, -91.33) * mm, v(355.94, -91.13) * mm, v(356.58, -91.52) * mm]});
            skFitSpline(sketch, "E524", {"points": [v(356.58, -91.52) * mm, v(357.21, -91.92) * mm, v(357.37, -92.82) * mm, v(356.93, -93.53) * mm]});
            skFitSpline(sketch, "E525", {"points": [v(356.93, -93.53) * mm, v(356.47, -94.28) * mm, v(356.85, -94.6) * mm, v(357.83, -94.27) * mm]});
            skFitSpline(sketch, "E526", {"points": [v(357.83, -94.27) * mm, v(358.76, -93.95) * mm, v(359.54, -92.92) * mm, v(359.56, -91.97) * mm]});
            skFitSpline(sketch, "E527", {"points": [v(359.56, -91.97) * mm, v(359.58, -90.95) * mm, v(360.58, -90.38) * mm, v(362, -90.58) * mm]});
            skFitSpline(sketch, "E528", {"points": [v(362, -90.58) * mm, v(363.33, -90.76) * mm, v(365.66, -90.97) * mm, v(367.19, -91.03) * mm]});
            skFitSpline(sketch, "E529", {"points": [v(367.19, -91.03) * mm, v(368.71, -91.1) * mm, v(370.26, -91.64) * mm, v(370.64, -92.24) * mm]});
            skFitSpline(sketch, "E530", {"points": [v(370.64, -92.24) * mm, v(371, -92.84) * mm, v(371.82, -93.01) * mm, v(372.46, -92.62) * mm]});
            skFitSpline(sketch, "E531", {"points": [v(372.46, -92.62) * mm, v(374.12, -91.6) * mm, v(375.3, -95.5) * mm, v(373.86, -97.28) * mm]});
            skFitSpline(sketch, "E532", {"points": [v(373.86, -97.28) * mm, v(373.2, -98.11) * mm, v(372.28, -100.5) * mm, v(371.83, -102.6) * mm]});
            skFitSpline(sketch, "E533", {"points": [v(371.83, -102.6) * mm, v(371.08, -106.14) * mm, v(371.48, -106.75) * mm, v(377.3, -110.94) * mm]});
            skFitSpline(sketch, "E534", {"points": [v(377.3, -110.94) * mm, v(380.77, -113.43) * mm, v(383.75, -115.28) * mm, v(383.93, -115.07) * mm]});
            skFitSpline(sketch, "E535", {"points": [v(383.93, -115.07) * mm, v(385.57, -113.1) * mm, v(387.36, -107.97) * mm, v(388.22, -102.7) * mm]});
            skFitSpline(sketch, "E536", {"points": [v(388.22, -102.7) * mm, v(389.83, -92.96) * mm, v(391.6, -89.06) * mm, v(393.64, -90.76) * mm]});
            skFitSpline(sketch, "E537", {"points": [v(393.64, -90.76) * mm, v(394.57, -91.53) * mm, v(395.67, -93.99) * mm, v(396.1, -96.22) * mm]});
            skFitSpline(sketch, "E538", {"points": [v(396.1, -96.22) * mm, v(396.51, -98.46) * mm, v(397.94, -101.27) * mm, v(399.27, -102.48) * mm]});
            skFitSpline(sketch, "E539", {"points": [v(399.27, -102.48) * mm, v(400.88, -103.93) * mm, v(401.7, -106.24) * mm, v(401.7, -109.33) * mm]});
            skFitSpline(sketch, "E540", {"points": [v(401.7, -109.33) * mm, v(401.7, -115.36) * mm, v(404.92, -122.03) * mm, v(408.66, -123.73) * mm]});
            skFitSpline(sketch, "E541", {"points": [v(408.66, -123.73) * mm, v(410.28, -124.47) * mm, v(411.3, -125.57) * mm, v(410.93, -126.17) * mm]});
            skFitSpline(sketch, "E542", {"points": [v(410.93, -126.17) * mm, v(410.56, -126.77) * mm, v(411.62, -128.56) * mm, v(413.3, -130.14) * mm]});
            skFitSpline(sketch, "E543", {"points": [v(413.3, -130.14) * mm, v(414.96, -131.72) * mm, v(416.33, -133.57) * mm, v(416.34, -134.25) * mm]});
            skFitSpline(sketch, "E544", {"points": [v(416.34, -134.25) * mm, v(416.36, -135.6) * mm, v(421.13, -139.01) * mm, v(423.08, -139.08) * mm]});
            skFitSpline(sketch, "E545", {"points": [v(423.08, -139.08) * mm, v(425.83, -139.18) * mm, v(423.58, -163.39) * mm, v(420.13, -170.9) * mm]});
            skFitSpline(sketch, "E546", {"points": [v(420.13, -170.9) * mm, v(417.45, -176.74) * mm, v(414.98, -183.64) * mm, v(414.65, -186.2) * mm]});
            skFitSpline(sketch, "E547", {"points": [v(414.65, -186.2) * mm, v(414.22, -189.56) * mm, v(412.53, -191.18) * mm, v(410.22, -190.45) * mm]});
            skFitSpline(sketch, "E548", {"points": [v(410.22, -190.45) * mm, v(408.64, -189.95) * mm, v(407.32, -190.68) * mm, v(405.9, -192.84) * mm]});
            skFitSpline(sketch, "E549", {"points": [v(405.9, -192.84) * mm, v(403.43, -196.62) * mm, v(402.85, -196.68) * mm, v(400.05, -193.4) * mm]});
            skFitSpline(sketch, "E550", {"points": [v(13.63, 88.86) * mm, v(15.04, 91.77) * mm, v(12.37, 96.16) * mm, v(10.53, 96.16) * mm]});
            skFitSpline(sketch, "E551", {"points": [v(10.53, 96.16) * mm, v(9.89, 96.16) * mm, v(8.94, 96.22) * mm, v(8.44, 96.3) * mm]});
            skFitSpline(sketch, "E552", {"points": [v(8.44, 96.3) * mm, v(6.67, 96.57) * mm, v(-1.05, 103.95) * mm, v(-3.15, 107.37) * mm]});
            skFitSpline(sketch, "E553", {"points": [v(-3.15, 107.37) * mm, v(-5.46, 111.13) * mm, v(-7.69, 111.63) * mm, v(-11.8, 109.33) * mm]});
            skFitSpline(sketch, "E554", {"points": [v(-11.8, 109.33) * mm, v(-13.28, 108.51) * mm, v(-16.4, 107.83) * mm, v(-18.76, 107.8) * mm]});
            skFitSpline(sketch, "E555", {"points": [v(-18.76, 107.8) * mm, v(-22.52, 107.77) * mm, v(-23.08, 107.36) * mm, v(-23.43, 104.33) * mm]});
            skFitSpline(sketch, "E556", {"points": [v(-23.43, 104.33) * mm, v(-23.77, 101.32) * mm, v(-28.02, 97.37) * mm, v(-32.58, 95.83) * mm]});
            skFitSpline(sketch, "E557", {"points": [v(-32.58, 95.83) * mm, v(-33.13, 95.64) * mm, v(-33.75, 93.88) * mm, v(-33.97, 91.92) * mm]});
            skFitSpline(sketch, "E558", {"points": [v(-33.97, 91.92) * mm, v(-34.4, 87.9) * mm, v(-38.23, 84.25) * mm, v(-43.05, 83.21) * mm]});
            skFitSpline(sketch, "E559", {"points": [v(-43.05, 83.21) * mm, v(-44.81, 82.83) * mm, v(-47.55, 81.9) * mm, v(-49.13, 81.12) * mm]});
            skFitSpline(sketch, "E560", {"points": [v(-49.13, 81.12) * mm, v(-51.5, 79.97) * mm, v(-52.27, 80.1) * mm, v(-53.54, 81.83) * mm]});
            skFitSpline(sketch, "E561", {"points": [v(-53.54, 81.83) * mm, v(-54.39, 82.99) * mm, v(-56.22, 83.93) * mm, v(-57.6, 83.93) * mm]});
            skFitSpline(sketch, "E562", {"points": [v(-57.6, 83.93) * mm, v(-61.13, 83.93) * mm, v(-64.42, 90.6) * mm, v(-62.6, 94.02) * mm]});
            skFitSpline(sketch, "E563", {"points": [v(-62.6, 94.02) * mm, v(-61.86, 95.4) * mm, v(-61.52, 99.2) * mm, v(-61.83, 102.5) * mm]});
            skFitSpline(sketch, "E564", {"points": [v(-61.83, 102.5) * mm, v(-62.28, 107.15) * mm, v(-61.97, 108.71) * mm, v(-60.44, 109.52) * mm]});
            skFitSpline(sketch, "E565", {"points": [v(-60.44, 109.52) * mm, v(-58.54, 110.53) * mm, v(-48.93, 110.24) * mm, v(-43.65, 109) * mm]});
            skFitSpline(sketch, "E566", {"points": [v(-43.65, 109) * mm, v(-36.28, 107.3) * mm, v(-37.15, 122.24) * mm, v(-44.63, 125.97) * mm]});
            skFitSpline(sketch, "E567", {"points": [v(-44.63, 125.97) * mm, v(-48.6, 127.96) * mm, v(-48.35, 131.05) * mm, v(-44.24, 130.78) * mm]});
            skFitSpline(sketch, "E568", {"points": [v(-44.24, 130.78) * mm, v(-41.9, 130.62) * mm, v(-40.81, 131.26) * mm, v(-40.35, 133.04) * mm]});
            skFitSpline(sketch, "E569", {"points": [v(-40.35, 133.04) * mm, v(-40, 134.4) * mm, v(-39.15, 135.18) * mm, v(-38.49, 134.76) * mm]});
            skFitSpline(sketch, "E570", {"points": [v(-38.49, 134.76) * mm, v(-36.67, 133.64) * mm, v(-31.26, 136.48) * mm, v(-29.2, 139.65) * mm]});
            skFitSpline(sketch, "E571", {"points": [v(-29.2, 139.65) * mm, v(-28.2, 141.17) * mm, v(-26.14, 142.6) * mm, v(-24.64, 142.82) * mm]});
            skFitSpline(sketch, "E572", {"points": [v(-24.64, 142.82) * mm, v(-22.9, 143.07) * mm, v(-21.65, 144.32) * mm, v(-21.2, 146.27) * mm]});
            skFitSpline(sketch, "E573", {"points": [v(-21.2, 146.27) * mm, v(-20.8, 147.95) * mm, v(-19.95, 149.23) * mm, v(-19.31, 149.1) * mm]});
            skFitSpline(sketch, "E574", {"points": [v(-19.31, 149.1) * mm, v(-18.67, 148.99) * mm, v(-17.15, 149.79) * mm, v(-15.93, 150.89) * mm]});
            skFitSpline(sketch, "E575", {"points": [v(-15.93, 150.89) * mm, v(-14.72, 151.99) * mm, v(-12.17, 152.77) * mm, v(-10.28, 152.63) * mm]});
            skFitSpline(sketch, "E576", {"points": [v(-10.28, 152.63) * mm, v(-9.13, 152.54) * mm, v(-6.76, 152.04) * mm, v(-6.83, 152.36) * mm]});
            skFitSpline(sketch, "E577", {"points": [v(-6.83, 152.36) * mm, v(-7.23, 154.24) * mm, v(-7.63, 156.12) * mm, v(-8.03, 158) * mm]});
            skFitSpline(sketch, "E578", {"points": [v(-8.03, 158) * mm, v(-9, 162.59) * mm, v(-8.88, 164) * mm, v(-7.37, 165.51) * mm]});
            skFitSpline(sketch, "E579", {"points": [v(-7.37, 165.51) * mm, v(-3.47, 169.42) * mm, v(-1, 165.72) * mm, v(-3.43, 159.6) * mm]});
            skFitSpline(sketch, "E580", {"points": [v(-3.43, 159.6) * mm, v(-4.71, 156.37) * mm, v(-1.1, 154.35) * mm, v(3.27, 155.87) * mm]});
            skFitSpline(sketch, "E581", {"points": [v(3.27, 155.87) * mm, v(6.59, 157.03) * mm, v(7.13, 156.89) * mm, v(7.96, 154.64) * mm]});
            skFitSpline(sketch, "E582", {"points": [v(7.96, 154.64) * mm, v(8.78, 152.44) * mm, v(9.13, 152.33) * mm, v(10.66, 153.85) * mm]});
            skFitSpline(sketch, "E583", {"points": [v(10.66, 153.85) * mm, v(13.54, 156.73) * mm, v(20.47, 158.7) * mm, v(22.31, 157.17) * mm]});
            skFitSpline(sketch, "E584", {"points": [v(22.31, 157.17) * mm, v(24.99, 154.94) * mm, v(30.25, 159.57) * mm, v(29.46, 163.45) * mm]});
            skFitSpline(sketch, "E585", {"points": [v(29.46, 163.45) * mm, v(29, 165.66) * mm, v(29.59, 167.28) * mm, v(31.42, 168.94) * mm]});
            skFitSpline(sketch, "E586", {"points": [v(31.42, 168.94) * mm, v(33.88, 171.16) * mm, v(34.1, 171.17) * mm, v(35.57, 169.17) * mm]});
            skFitSpline(sketch, "E587", {"points": [v(35.57, 169.17) * mm, v(36.43, 168) * mm, v(37.48, 167.05) * mm, v(37.9, 167.05) * mm]});
            skFitSpline(sketch, "E588", {"points": [v(37.9, 167.05) * mm, v(39.18, 167.05) * mm, v(38.8, 171.72) * mm, v(37.47, 172.55) * mm]});
            skFitSpline(sketch, "E589", {"points": [v(37.47, 172.55) * mm, v(35.52, 173.75) * mm, v(36.05, 178.05) * mm, v(38.24, 178.89) * mm]});
            skFitSpline(sketch, "E590", {"points": [v(38.24, 178.89) * mm, v(39.34, 179.31) * mm, v(42.5, 179.75) * mm, v(45.27, 179.88) * mm]});
            skFitSpline(sketch, "E591", {"points": [v(45.27, 179.88) * mm, v(54.52, 180.28) * mm, v(55.14, 180.42) * mm, v(53.82, 181.74) * mm]});
            skFitSpline(sketch, "E592", {"points": [v(53.82, 181.74) * mm, v(51.98, 183.58) * mm, v(44.9, 183.36) * mm, v(39.3, 181.29) * mm]});
            skFitSpline(sketch, "E593", {"points": [v(39.3, 181.29) * mm, v(34.98, 179.69) * mm, v(34.17, 179.69) * mm, v(32.4, 181.29) * mm]});
            skFitSpline(sketch, "E594", {"points": [v(32.4, 181.29) * mm, v(31.28, 182.28) * mm, v(30.16, 185.3) * mm, v(29.9, 187.99) * mm]});
            skFitSpline(sketch, "E595", {"points": [v(29.9, 187.99) * mm, v(29.49, 192.4) * mm, v(30, 193.48) * mm, v(35.28, 199.21) * mm]});
            skFitSpline(sketch, "E596", {"points": [v(35.28, 199.21) * mm, v(41.5, 205.96) * mm, v(41.95, 207.75) * mm, v(37.6, 208.4) * mm]});
            skFitSpline(sketch, "E597", {"points": [v(37.6, 208.4) * mm, v(34.12, 208.9) * mm, v(31.36, 206.6) * mm, v(31.36, 203.18) * mm]});
            skFitSpline(sketch, "E598", {"points": [v(31.36, 203.18) * mm, v(31.36, 200.64) * mm, v(27.01, 196.49) * mm, v(22.67, 194.88) * mm]});
            skFitSpline(sketch, "E599", {"points": [v(22.67, 194.88) * mm, v(21.57, 194.47) * mm, v(20.38, 192.12) * mm, v(19.96, 189.5) * mm]});
            skFitSpline(sketch, "E600", {"points": [v(19.96, 189.5) * mm, v(19.36, 185.82) * mm, v(19.72, 184.3) * mm, v(21.7, 182.2) * mm]});
            skFitSpline(sketch, "E601", {"points": [v(21.7, 182.2) * mm, v(23.35, 180.44) * mm, v(23.75, 179.24) * mm, v(22.87, 178.7) * mm]});
            skFitSpline(sketch, "E602", {"points": [v(22.87, 178.7) * mm, v(22.14, 178.25) * mm, v(21.88, 177.33) * mm, v(22.3, 176.66) * mm]});
            skFitSpline(sketch, "E603", {"points": [v(22.3, 176.66) * mm, v(22.7, 175.99) * mm, v(21.9, 175.14) * mm, v(20.48, 174.77) * mm]});
            skFitSpline(sketch, "E604", {"points": [v(20.48, 174.77) * mm, v(17.98, 174.11) * mm, v(17.7, 173.43) * mm, v(17.43, 167.05) * mm]});
            skFitSpline(sketch, "E605", {"points": [v(17.43, 167.05) * mm, v(17.33, 164.77) * mm, v(16.53, 163.88) * mm, v(14.28, 163.56) * mm]});
            skFitSpline(sketch, "E606", {"points": [v(14.28, 163.56) * mm, v(12.62, 163.33) * mm, v(10.18, 162.38) * mm, v(8.86, 161.46) * mm]});
            skFitSpline(sketch, "E607", {"points": [v(8.86, 161.46) * mm, v(6.48, 159.8) * mm, v(3.24, 160.96) * mm, v(3.24, 163.48) * mm]});
            skFitSpline(sketch, "E608", {"points": [v(3.24, 163.48) * mm, v(3.24, 164.05) * mm, v(2.1, 167.57) * mm, v(0.7, 171.3) * mm]});
            skFitSpline(sketch, "E609", {"points": [v(0.7, 171.3) * mm, v(-0.15, 173.57) * mm, v(-1, 175.83) * mm, v(-1.84, 178.1) * mm]});
            skFitSpline(sketch, "E610", {"points": [v(-1.84, 178.1) * mm, v(-3.06, 177.07) * mm, v(-4.28, 176.04) * mm, v(-5.5, 175.02) * mm]});
            skFitSpline(sketch, "E611", {"points": [v(-5.5, 175.02) * mm, v(-11.62, 169.87) * mm, v(-17.8, 171.5) * mm, v(-16.74, 178) * mm]});
            skFitSpline(sketch, "E612", {"points": [v(-16.74, 178) * mm, v(-16.47, 179.65) * mm, v(-16.62, 181.85) * mm, v(-17.08, 182.89) * mm]});
            skFitSpline(sketch, "E613", {"points": [v(-17.08, 182.89) * mm, v(-19.21, 187.75) * mm, v(-16.87, 192.2) * mm, v(-11.04, 194.33) * mm]});
            skFitSpline(sketch, "E614", {"points": [v(-11.04, 194.33) * mm, v(-9.82, 194.78) * mm, v(-9.14, 195.66) * mm, v(-9.53, 196.29) * mm]});
            skFitSpline(sketch, "E615", {"points": [v(-9.53, 196.29) * mm, v(-10.65, 198.1) * mm, v(-8.03, 199.06) * mm, v(-5.58, 197.74) * mm]});
            skFitSpline(sketch, "E616", {"points": [v(-5.58, 197.74) * mm, v(-4.35, 197.09) * mm, v(-2.8, 196.92) * mm, v(-2.15, 197.38) * mm]});
            skFitSpline(sketch, "E617", {"points": [v(-2.15, 197.38) * mm, v(-0.4, 198.6) * mm, v(-0.68, 202.94) * mm, v(-2.59, 204.12) * mm]});
            skFitSpline(sketch, "E618", {"points": [v(-2.59, 204.12) * mm, v(-4.72, 205.44) * mm, v(-2.32, 208.6) * mm, v(0.81, 208.6) * mm]});
            skFitSpline(sketch, "E619", {"points": [v(0.81, 208.6) * mm, v(2.12, 208.6) * mm, v(2.9, 209.45) * mm, v(2.8, 210.74) * mm]});
            skFitSpline(sketch, "E620", {"points": [v(2.8, 210.74) * mm, v(2.7, 211.92) * mm, v(3.3, 212.75) * mm, v(4.12, 212.59) * mm]});
            skFitSpline(sketch, "E621", {"points": [v(4.12, 212.59) * mm, v(4.93, 212.43) * mm, v(7.37, 214.51) * mm, v(9.55, 217.21) * mm]});
            skFitSpline(sketch, "E622", {"points": [v(9.55, 217.21) * mm, v(11.72, 219.92) * mm, v(14.21, 221.85) * mm, v(15.1, 221.51) * mm]});
            skFitSpline(sketch, "E623", {"points": [v(15.1, 221.51) * mm, v(15.97, 221.18) * mm, v(16.69, 221.43) * mm, v(16.69, 222.09) * mm]});
            skFitSpline(sketch, "E624", {"points": [v(16.69, 222.09) * mm, v(16.69, 222.74) * mm, v(16.69, 223.68) * mm, v(16.69, 224.19) * mm]});
            skFitSpline(sketch, "E625", {"points": [v(16.69, 224.19) * mm, v(16.69, 224.69) * mm, v(16.14, 225.1) * mm, v(15.47, 225.1) * mm]});
            skFitSpline(sketch, "E626", {"points": [v(15.47, 225.1) * mm, v(14.8, 225.1) * mm, v(14.1, 225.6) * mm, v(13.94, 226.2) * mm]});
            skFitSpline(sketch, "E627", {"points": [v(13.94, 226.2) * mm, v(13.64, 227.28) * mm, v(16.62, 228.27) * mm, v(20.35, 228.33) * mm]});
            skFitSpline(sketch, "E628", {"points": [v(20.35, 228.33) * mm, v(21.36, 228.35) * mm, v(23.01, 228.68) * mm, v(24.02, 229.07) * mm]});
            skFitSpline(sketch, "E629", {"points": [v(24.02, 229.07) * mm, v(25.03, 229.46) * mm, v(26.27, 229.83) * mm, v(26.77, 229.89) * mm]});
            skFitSpline(sketch, "E630", {"points": [v(26.77, 229.89) * mm, v(28.15, 230.04) * mm, v(27.88, 232.41) * mm, v(26.47, 232.59) * mm]});
            skFitSpline(sketch, "E631", {"points": [v(26.47, 232.59) * mm, v(24.07, 232.89) * mm, v(23.89, 233.06) * mm, v(24.67, 234.33) * mm]});
            skFitSpline(sketch, "E632", {"points": [v(24.67, 234.33) * mm, v(25.21, 235.2) * mm, v(26, 235.16) * mm, v(27.19, 234.18) * mm]});
            skFitSpline(sketch, "E633", {"points": [v(27.19, 234.18) * mm, v(28.13, 233.4) * mm, v(28.91, 233.08) * mm, v(28.91, 233.48) * mm]});
            skFitSpline(sketch, "E634", {"points": [v(28.91, 233.48) * mm, v(28.91, 233.88) * mm, v(30.2, 233.72) * mm, v(31.76, 233.12) * mm]});
            skFitSpline(sketch, "E635", {"points": [v(31.76, 233.12) * mm, v(33.43, 232.5) * mm, v(35.33, 232.5) * mm, v(36.35, 233.14) * mm]});
            skFitSpline(sketch, "E636", {"points": [v(36.35, 233.14) * mm, v(37.3, 233.74) * mm, v(37.67, 234.3) * mm, v(37.16, 234.4) * mm]});
            skFitSpline(sketch, "E637", {"points": [v(37.16, 234.4) * mm, v(36.66, 234.5) * mm, v(35.7, 234.71) * mm, v(35.02, 234.88) * mm]});
            skFitSpline(sketch, "E638", {"points": [v(35.02, 234.88) * mm, v(34.35, 235.05) * mm, v(33.5, 235.26) * mm, v(33.12, 235.34) * mm]});
            skFitSpline(sketch, "E639", {"points": [v(33.12, 235.34) * mm, v(32.74, 235.42) * mm, v(32.78, 236.05) * mm, v(33.2, 236.73) * mm]});
            skFitSpline(sketch, "E640", {"points": [v(33.2, 236.73) * mm, v(33.62, 237.42) * mm, v(34.62, 237.56) * mm, v(35.41, 237.06) * mm]});
            skFitSpline(sketch, "E641", {"points": [v(35.41, 237.06) * mm, v(37.4, 235.8) * mm, v(38.94, 235.77) * mm, v(41.37, 236.94) * mm]});
            skFitSpline(sketch, "E642", {"points": [v(41.37, 236.94) * mm, v(42.52, 237.5) * mm, v(43.74, 237.44) * mm, v(44.14, 236.8) * mm]});
            skFitSpline(sketch, "E643", {"points": [v(44.14, 236.8) * mm, v(44.52, 236.17) * mm, v(46.17, 235.9) * mm, v(47.8, 236.2) * mm]});
            skFitSpline(sketch, "E644", {"points": [v(47.8, 236.2) * mm, v(49.42, 236.5) * mm, v(51.1, 236.18) * mm, v(51.52, 235.5) * mm]});
            skFitSpline(sketch, "E645", {"points": [v(51.52, 235.5) * mm, v(51.94, 234.82) * mm, v(53.59, 234.27) * mm, v(55.19, 234.27) * mm]});
            skFitSpline(sketch, "E646", {"points": [v(55.19, 234.27) * mm, v(59.24, 234.27) * mm, v(60.2, 232.06) * mm, v(56.8, 230.57) * mm]});
            skFitSpline(sketch, "E647", {"points": [v(56.8, 230.57) * mm, v(54.6, 229.6) * mm, v(55.35, 229.47) * mm, v(60.22, 229.99) * mm]});
            skFitSpline(sketch, "E648", {"points": [v(60.22, 229.99) * mm, v(64.92, 230.48) * mm, v(66.85, 230.18) * mm, v(68, 228.79) * mm]});
            skFitSpline(sketch, "E649", {"points": [v(68, 228.79) * mm, v(68.85, 227.77) * mm, v(70.32, 226.94) * mm, v(71.26, 226.94) * mm]});
            skFitSpline(sketch, "E650", {"points": [v(71.26, 226.94) * mm, v(72.2, 226.94) * mm, v(76.8, 225) * mm, v(81.5, 222.64) * mm]});
            skFitSpline(sketch, "E651", {"points": [v(81.5, 222.64) * mm, v(91.15, 217.78) * mm, v(92.48, 214.83) * mm, v(86.42, 211.69) * mm]});
            skFitSpline(sketch, "E652", {"points": [v(86.42, 211.69) * mm, v(81.94, 209.37) * mm, v(75.71, 209.36) * mm, v(71.69, 211.66) * mm]});
            skFitSpline(sketch, "E653", {"points": [v(71.69, 211.66) * mm, v(67.2, 214.22) * mm, v(64.3, 213.99) * mm, v(67.56, 211.32) * mm]});
            skFitSpline(sketch, "E654", {"points": [v(67.56, 211.32) * mm, v(69, 210.16) * mm, v(70.5, 207.8) * mm, v(70.9, 206.06) * mm]});
            skFitSpline(sketch, "E655", {"points": [v(70.9, 206.06) * mm, v(71.31, 204.28) * mm, v(73.04, 202.27) * mm, v(74.87, 201.43) * mm]});
            skFitSpline(sketch, "E656", {"points": [v(74.87, 201.43) * mm, v(78.78, 199.65) * mm, v(80.34, 200.65) * mm, v(77.22, 202.93) * mm]});
            skFitSpline(sketch, "E657", {"points": [v(77.22, 202.93) * mm, v(73.54, 205.62) * mm, v(76.08, 207.7) * mm, v(80.35, 205.5) * mm]});
            skFitSpline(sketch, "E658", {"points": [v(80.35, 205.5) * mm, v(83.88, 203.66) * mm, v(87.05, 204.05) * mm, v(85.75, 206.14) * mm]});
            skFitSpline(sketch, "E659", {"points": [v(85.75, 206.14) * mm, v(85.4, 206.72) * mm, v(86.87, 208.56) * mm, v(89.03, 210.25) * mm]});
            skFitSpline(sketch, "E660", {"points": [v(89.03, 210.25) * mm, v(91.94, 212.53) * mm, v(93.5, 213.03) * mm, v(95.08, 212.18) * mm]});
            skFitSpline(sketch, "E661", {"points": [v(95.08, 212.18) * mm, v(98.13, 210.55) * mm, v(99.02, 212.74) * mm, v(97.36, 217.77) * mm]});
            skFitSpline(sketch, "E662", {"points": [v(97.36, 217.77) * mm, v(95.36, 223.83) * mm, v(96.64, 224.9) * mm, v(102.36, 222) * mm]});
            skFitSpline(sketch, "E663", {"points": [v(102.36, 222) * mm, v(107.01, 219.62) * mm, v(107.82, 217.16) * mm, v(103.93, 217.16) * mm]});
            skFitSpline(sketch, "E664", {"points": [v(103.93, 217.16) * mm, v(102.93, 217.16) * mm, v(102.44, 216.6) * mm, v(102.86, 215.94) * mm]});
            skFitSpline(sketch, "E665", {"points": [v(102.86, 215.94) * mm, v(104.18, 213.8) * mm, v(106.93, 214.6) * mm, v(111.23, 218.38) * mm]});
            skFitSpline(sketch, "E666", {"points": [v(111.23, 218.38) * mm, v(113.52, 220.4) * mm, v(116.6, 222.05) * mm, v(118.05, 222.05) * mm]});
            skFitSpline(sketch, "E667", {"points": [v(118.05, 222.05) * mm, v(119.5, 222.05) * mm, v(122.37, 222.9) * mm, v(124.4, 223.96) * mm]});
            skFitSpline(sketch, "E668", {"points": [v(124.4, 223.96) * mm, v(127.88, 225.76) * mm, v(128.14, 225.73) * mm, v(128.71, 223.53) * mm]});
            skFitSpline(sketch, "E669", {"points": [v(128.71, 223.53) * mm, v(129.26, 221.45) * mm, v(129.78, 221.33) * mm, v(133.26, 222.53) * mm]});
            skFitSpline(sketch, "E670", {"points": [v(133.26, 222.53) * mm, v(135.42, 223.27) * mm, v(138.61, 224.82) * mm, v(140.36, 225.96) * mm]});
            skFitSpline(sketch, "E671", {"points": [v(140.36, 225.96) * mm, v(143.8, 228.2) * mm, v(145.84, 227.56) * mm, v(143.64, 224.9) * mm]});
            skFitSpline(sketch, "E672", {"points": [v(143.64, 224.9) * mm, v(142.6, 223.65) * mm, v(142.74, 223.27) * mm, v(144.24, 223.27) * mm]});
            skFitSpline(sketch, "E673", {"points": [v(144.24, 223.27) * mm, v(145.31, 223.27) * mm, v(147.12, 224.7) * mm, v(148.27, 226.44) * mm]});
            skFitSpline(sketch, "E674", {"points": [v(148.27, 226.44) * mm, v(150.22, 229.42) * mm, v(150.75, 229.56) * mm, v(157.16, 228.78) * mm]});
            skFitSpline(sketch, "E675", {"points": [v(157.16, 228.78) * mm, v(161.22, 228.28) * mm, v(164.99, 227) * mm, v(166.5, 225.6) * mm]});
            skFitSpline(sketch, "E676", {"points": [v(166.5, 225.6) * mm, v(167.88, 224.32) * mm, v(169.67, 223.27) * mm, v(170.46, 223.27) * mm]});
            skFitSpline(sketch, "E677", {"points": [v(170.46, 223.27) * mm, v(172.54, 223.27) * mm, v(172.26, 226.88) * mm, v(170.11, 227.7) * mm]});
            skFitSpline(sketch, "E678", {"points": [v(170.11, 227.7) * mm, v(169.12, 228.09) * mm, v(167.51, 229.99) * mm, v(166.54, 231.93) * mm]});
            skFitSpline(sketch, "E679", {"points": [v(166.54, 231.93) * mm, v(164.9, 235.23) * mm, v(164.97, 235.62) * mm, v(167.53, 237.63) * mm]});
            skFitSpline(sketch, "E680", {"points": [v(167.53, 237.63) * mm, v(169.04, 238.82) * mm, v(171.06, 241.44) * mm, v(172.02, 243.45) * mm]});
            skFitSpline(sketch, "E681", {"points": [v(172.02, 243.45) * mm, v(174.02, 247.65) * mm, v(178.52, 248.8) * mm, v(182.26, 246.07) * mm]});
            skFitSpline(sketch, "E682", {"points": [v(182.26, 246.07) * mm, v(184.26, 244.6) * mm, v(184.43, 243.83) * mm, v(183.3, 241.35) * mm]});
            skFitSpline(sketch, "E683", {"points": [v(183.3, 241.35) * mm, v(182.5, 239.6) * mm, v(182.38, 237.62) * mm, v(183, 236.52) * mm]});
            skFitSpline(sketch, "E684", {"points": [v(183, 236.52) * mm, v(184.6, 233.65) * mm, v(184.67, 220.43) * mm, v(183.09, 217.49) * mm]});
            skFitSpline(sketch, "E685", {"points": [v(183.09, 217.49) * mm, v(181.26, 214.07) * mm, v(181.33, 213.43) * mm, v(183.43, 214.23) * mm]});
            skFitSpline(sketch, "E686", {"points": [v(183.43, 214.23) * mm, v(184.39, 214.6) * mm, v(186.04, 217.08) * mm, v(187.1, 219.74) * mm]});
            skFitSpline(sketch, "E687", {"points": [v(187.1, 219.74) * mm, v(188.17, 222.4) * mm, v(189.88, 224.9) * mm, v(190.91, 225.3) * mm]});
            skFitSpline(sketch, "E688", {"points": [v(190.91, 225.3) * mm, v(193.27, 226.2) * mm, v(197.58, 222.4) * mm, v(197.58, 219.41) * mm]});
            skFitSpline(sketch, "E689", {"points": [v(197.58, 219.41) * mm, v(197.58, 218.17) * mm, v(198.08, 217.16) * mm, v(198.69, 217.16) * mm]});
            skFitSpline(sketch, "E690", {"points": [v(198.69, 217.16) * mm, v(200.23, 217.16) * mm, v(198.85, 222.2) * mm, v(196.6, 224.8) * mm]});
            skFitSpline(sketch, "E691", {"points": [v(196.6, 224.8) * mm, v(195.6, 225.97) * mm, v(193.21, 226.94) * mm, v(191.32, 226.94) * mm]});
            skFitSpline(sketch, "E692", {"points": [v(191.32, 226.94) * mm, v(188.1, 226.94) * mm, v(184.5, 230.56) * mm, v(186.11, 232.17) * mm]});
            skFitSpline(sketch, "E693", {"points": [v(186.11, 232.17) * mm, v(186.48, 232.54) * mm, v(186.14, 234.03) * mm, v(185.36, 235.49) * mm]});
            skFitSpline(sketch, "E694", {"points": [v(185.36, 235.49) * mm, v(184.24, 237.58) * mm, v(184.3, 238.57) * mm, v(185.69, 240.18) * mm]});
            skFitSpline(sketch, "E695", {"points": [v(185.69, 240.18) * mm, v(186.65, 241.3) * mm, v(187.79, 243.21) * mm, v(188.22, 244.43) * mm]});
            skFitSpline(sketch, "E696", {"points": [v(188.22, 244.43) * mm, v(189.27, 247.37) * mm, v(190.99, 246.15) * mm, v(191.85, 241.86) * mm]});
            skFitSpline(sketch, "E697", {"points": [v(191.85, 241.86) * mm, v(192.27, 239.72) * mm, v(193.75, 237.84) * mm, v(195.73, 236.95) * mm]});
            skFitSpline(sketch, "E698", {"points": [v(195.73, 236.95) * mm, v(200.57, 234.74) * mm, v(201.01, 235.2) * mm, v(197.08, 238.35) * mm]});
            skFitSpline(sketch, "E699", {"points": [v(197.08, 238.35) * mm, v(194.9, 240.1) * mm, v(193.87, 241.77) * mm, v(194.44, 242.68) * mm]});
            skFitSpline(sketch, "E700", {"points": [v(194.44, 242.68) * mm, v(195.1, 243.77) * mm, v(195.79, 243.8) * mm, v(196.97, 242.83) * mm]});
            skFitSpline(sketch, "E701", {"points": [v(196.97, 242.83) * mm, v(197.95, 242.01) * mm, v(198.87, 241.94) * mm, v(199.3, 242.64) * mm]});
            skFitSpline(sketch, "E702", {"points": [v(199.3, 242.64) * mm, v(199.69, 243.27) * mm, v(199.1, 244.14) * mm, v(197.98, 244.57) * mm]});
            skFitSpline(sketch, "E703", {"points": [v(197.98, 244.57) * mm, v(196.43, 245.16) * mm, v(196.29, 245.69) * mm, v(197.38, 246.78) * mm]});
            skFitSpline(sketch, "E704", {"points": [v(197.38, 246.78) * mm, v(198.46, 247.86) * mm, v(199.15, 247.85) * mm, v(200.27, 246.74) * mm]});
            skFitSpline(sketch, "E705", {"points": [v(200.27, 246.74) * mm, v(201.08, 245.93) * mm, v(201.21, 245.24) * mm, v(200.57, 245.21) * mm]});
            skFitSpline(sketch, "E706", {"points": [v(200.57, 245.21) * mm, v(199.94, 245.18) * mm, v(202.44, 243.9) * mm, v(206.14, 242.36) * mm]});
            skFitSpline(sketch, "E707", {"points": [v(206.14, 242.36) * mm, v(211.97, 239.93) * mm, v(212.82, 239.16) * mm, v(212.54, 236.5) * mm]});
            skFitSpline(sketch, "E708", {"points": [v(212.54, 236.5) * mm, v(212.32, 234.42) * mm, v(212.82, 233.45) * mm, v(214.12, 233.45) * mm]});
            skFitSpline(sketch, "E709", {"points": [v(214.12, 233.45) * mm, v(215.26, 233.45) * mm, v(215.75, 234.15) * mm, v(215.36, 235.18) * mm]});
            skFitSpline(sketch, "E710", {"points": [v(215.36, 235.18) * mm, v(215, 236.14) * mm, v(214.7, 237.72) * mm, v(214.7, 238.7) * mm]});
            skFitSpline(sketch, "E711", {"points": [v(214.7, 238.7) * mm, v(214.7, 239.7) * mm, v(212.73, 241.32) * mm, v(210.34, 242.32) * mm]});
            skFitSpline(sketch, "E712", {"points": [v(210.34, 242.32) * mm, v(206.67, 243.86) * mm, v(206.04, 244.67) * mm, v(206.37, 247.46) * mm]});
            skFitSpline(sketch, "E713", {"points": [v(206.37, 247.46) * mm, v(206.7, 250.44) * mm, v(207.17, 250.73) * mm, v(210.96, 250.35) * mm]});
            skFitSpline(sketch, "E714", {"points": [v(210.96, 250.35) * mm, v(214.7, 249.99) * mm, v(215, 250.16) * mm, v(213.56, 251.88) * mm]});
            skFitSpline(sketch, "E715", {"points": [v(213.56, 251.88) * mm, v(212.67, 252.95) * mm, v(212.3, 253.83) * mm, v(212.7, 253.83) * mm]});
            skFitSpline(sketch, "E716", {"points": [v(212.7, 253.83) * mm, v(214.7, 253.83) * mm, v(215.28, 253.5) * mm, v(215.02, 252.55) * mm]});
            skFitSpline(sketch, "E717", {"points": [v(215.02, 252.55) * mm, v(214.86, 251.98) * mm, v(217.06, 251.03) * mm, v(219.9, 250.44) * mm]});
            skFitSpline(sketch, "E718", {"points": [v(219.9, 250.44) * mm, v(225.46, 249.28) * mm, v(227.29, 249.64) * mm, v(224.52, 251.35) * mm]});
            skFitSpline(sketch, "E719", {"points": [v(224.52, 251.35) * mm, v(219.42, 254.5) * mm, v(225.88, 259.94) * mm, v(234.74, 259.94) * mm]});
            skFitSpline(sketch, "E720", {"points": [v(234.74, 259.94) * mm, v(236.87, 259.94) * mm, v(241.57, 260.7) * mm, v(245.2, 261.65) * mm]});
            skFitSpline(sketch, "E721", {"points": [v(245.2, 261.65) * mm, v(249.84, 262.85) * mm, v(252.38, 262.99) * mm, v(253.8, 262.1) * mm]});
            skFitSpline(sketch, "E722", {"points": [v(253.8, 262.1) * mm, v(255.27, 261.18) * mm, v(257.03, 261.42) * mm, v(260.3, 262.97) * mm]});
            skFitSpline(sketch, "E723", {"points": [v(260.3, 262.97) * mm, v(263.17, 264.33) * mm, v(265.96, 264.8) * mm, v(268.06, 264.27) * mm]});
            skFitSpline(sketch, "E724", {"points": [v(268.06, 264.27) * mm, v(270.84, 263.58) * mm, v(271.11, 263.72) * mm, v(269.87, 265.22) * mm]});
            skFitSpline(sketch, "E725", {"points": [v(269.87, 265.22) * mm, v(268.69, 266.65) * mm, v(269.02, 267.74) * mm, v(271.6, 270.8) * mm]});
            skFitSpline(sketch, "E726", {"points": [v(271.6, 270.8) * mm, v(274.2, 273.89) * mm, v(275.4, 274.45) * mm, v(278.05, 273.82) * mm]});
            skFitSpline(sketch, "E727", {"points": [v(278.05, 273.82) * mm, v(283.08, 272.62) * mm, v(283.7, 271.92) * mm, v(281.26, 270.14) * mm]});
            skFitSpline(sketch, "E728", {"points": [v(281.26, 270.14) * mm, v(279.1, 268.56) * mm, v(279.1, 268.5) * mm, v(281.44, 268.5) * mm]});
            skFitSpline(sketch, "E729", {"points": [v(281.44, 268.5) * mm, v(282.78, 268.5) * mm, v(284.44, 267.92) * mm, v(285.14, 267.22) * mm]});
            skFitSpline(sketch, "E730", {"points": [v(285.14, 267.22) * mm, v(286.02, 266.34) * mm, v(288.22, 266.35) * mm, v(292.27, 267.26) * mm]});
            skFitSpline(sketch, "E731", {"points": [v(292.27, 267.26) * mm, v(296.97, 268.32) * mm, v(298.52, 268.24) * mm, v(300.1, 266.86) * mm]});
            skFitSpline(sketch, "E732", {"points": [v(300.1, 266.86) * mm, v(301.2, 265.92) * mm, v(302.72, 265.38) * mm, v(303.5, 265.66) * mm]});
            skFitSpline(sketch, "E733", {"points": [v(303.5, 265.66) * mm, v(305.37, 266.34) * mm, v(306.77, 264) * mm, v(305.1, 262.97) * mm]});
            skFitSpline(sketch, "E734", {"points": [v(305.1, 262.97) * mm, v(304.2, 262.4) * mm, v(304.23, 261.64) * mm, v(305.22, 260.45) * mm]});
            skFitSpline(sketch, "E735", {"points": [v(305.22, 260.45) * mm, v(306.32, 259.12) * mm, v(306.2, 258.58) * mm, v(304.63, 257.98) * mm]});
            skFitSpline(sketch, "E736", {"points": [v(304.63, 257.98) * mm, v(303.3, 257.47) * mm, v(303.02, 256.74) * mm, v(303.78, 255.82) * mm]});
            skFitSpline(sketch, "E737", {"points": [v(303.78, 255.82) * mm, v(304.41, 255.06) * mm, v(304.87, 254.16) * mm, v(304.8, 253.83) * mm]});
            skFitSpline(sketch, "E738", {"points": [v(304.8, 253.83) * mm, v(304.73, 253.49) * mm, v(305.25, 252.18) * mm, v(305.96, 250.92) * mm]});
            skFitSpline(sketch, "E739", {"points": [v(305.96, 250.92) * mm, v(306.82, 249.39) * mm, v(307.53, 249.08) * mm, v(308.1, 250) * mm]});
            skFitSpline(sketch, "E740", {"points": [v(308.1, 250) * mm, v(309.01, 251.48) * mm, v(318.28, 251.89) * mm, v(321.64, 250.6) * mm]});
            skFitSpline(sketch, "E741", {"points": [v(321.64, 250.6) * mm, v(323.26, 249.98) * mm, v(323.35, 249.6) * mm, v(322.05, 248.79) * mm]});
            skFitSpline(sketch, "E742", {"points": [v(322.05, 248.79) * mm, v(321.04, 248.15) * mm, v(323.08, 247.74) * mm, v(327.31, 247.73) * mm]});
            skFitSpline(sketch, "E743", {"points": [v(327.31, 247.73) * mm, v(331.9, 247.72) * mm, v(334.42, 248.25) * mm, v(334.83, 249.32) * mm]});
            skFitSpline(sketch, "E744", {"points": [v(334.83, 249.32) * mm, v(335.24, 250.4) * mm, v(337.67, 250.9) * mm, v(342.29, 250.82) * mm]});
            skFitSpline(sketch, "E745", {"points": [v(342.29, 250.82) * mm, v(347.77, 250.73) * mm, v(349.5, 250.2) * mm, v(350.93, 248.15) * mm]});
            skFitSpline(sketch, "E746", {"points": [v(350.93, 248.15) * mm, v(352.91, 245.32) * mm, v(352.3, 244.05) * mm, v(348.96, 244.05) * mm]});
            skFitSpline(sketch, "E747", {"points": [v(348.96, 244.05) * mm, v(347.34, 244.05) * mm, v(348.17, 242.74) * mm, v(352.05, 239.16) * mm]});
            skFitSpline(sketch, "E748", {"points": [v(352.05, 239.16) * mm, v(358.24, 233.45) * mm, v(359.78, 233.16) * mm, v(361.37, 237.35) * mm]});
            skFitSpline(sketch, "E749", {"points": [v(361.37, 237.35) * mm, v(362.4, 240.07) * mm, v(362.83, 240.25) * mm, v(365, 238.89) * mm]});
            skFitSpline(sketch, "E750", {"points": [v(365, 238.89) * mm, v(366.9, 237.7) * mm, v(368, 237.68) * mm, v(369.75, 238.77) * mm]});
            skFitSpline(sketch, "E751", {"points": [v(369.75, 238.77) * mm, v(371.52, 239.88) * mm, v(372.75, 239.83) * mm, v(375.23, 238.54) * mm]});
            skFitSpline(sketch, "E752", {"points": [v(375.23, 238.54) * mm, v(377.21, 237.51) * mm, v(378.71, 237.33) * mm, v(379.17, 238.07) * mm]});
            skFitSpline(sketch, "E753", {"points": [v(379.17, 238.07) * mm, v(379.57, 238.72) * mm, v(381.03, 238.9) * mm, v(382.41, 238.46) * mm]});
            skFitSpline(sketch, "E754", {"points": [v(382.41, 238.46) * mm, v(384.59, 237.77) * mm, v(384.84, 238.09) * mm, v(384.31, 240.85) * mm]});
            skFitSpline(sketch, "E755", {"points": [v(384.31, 240.85) * mm, v(383.98, 242.6) * mm, v(384.36, 244.58) * mm, v(385.17, 245.25) * mm]});
            skFitSpline(sketch, "E756", {"points": [v(385.17, 245.25) * mm, v(385.98, 245.92) * mm, v(386.54, 248.14) * mm, v(386.42, 250.2) * mm]});
            skFitSpline(sketch, "E757", {"points": [v(386.42, 250.2) * mm, v(386.16, 254.46) * mm, v(387.97, 256.23) * mm, v(390, 253.7) * mm]});
            skFitSpline(sketch, "E758", {"points": [v(390, 253.7) * mm, v(390.75, 252.76) * mm, v(392.35, 251.44) * mm, v(393.57, 250.77) * mm]});
            skFitSpline(sketch, "E759", {"points": [v(393.57, 250.77) * mm, v(397.26, 248.72) * mm, v(396.45, 247.14) * mm, v(391.3, 246.36) * mm]});
            skFitSpline(sketch, "E760", {"points": [v(391.3, 246.36) * mm, v(389.68, 246.11) * mm, v(384.82, 245.75) * mm, v(386.42, 245.62) * mm]});
            skFitSpline(sketch, "E761", {"points": [v(386.42, 245.62) * mm, v(387.84, 245.5) * mm, v(389.27, 245.37) * mm, v(390.7, 245.25) * mm]});
            skFitSpline(sketch, "E762", {"points": [v(390.7, 245.25) * mm, v(393.05, 245.05) * mm, v(396.28, 245) * mm, v(397.88, 245.15) * mm]});
            skFitSpline(sketch, "E763", {"points": [v(397.88, 245.15) * mm, v(399.48, 245.3) * mm, v(401.6, 245.1) * mm, v(402.6, 244.72) * mm]});
            skFitSpline(sketch, "E764", {"points": [v(402.6, 244.72) * mm, v(404.14, 244.12) * mm, v(404.16, 243.71) * mm, v(402.75, 242) * mm]});
            skFitSpline(sketch, "E765", {"points": [v(402.75, 242) * mm, v(401.02, 239.9) * mm, v(401.3, 239.95) * mm, v(406.98, 242.8) * mm]});
            skFitSpline(sketch, "E766", {"points": [v(406.98, 242.8) * mm, v(410.75, 244.68) * mm, v(414.53, 243.4) * mm, v(414.53, 240.25) * mm]});
            skFitSpline(sketch, "E767", {"points": [v(414.53, 240.25) * mm, v(414.53, 239.31) * mm, v(415.52, 238.54) * mm, v(416.72, 238.54) * mm]});
            skFitSpline(sketch, "E768", {"points": [v(416.72, 238.54) * mm, v(417.92, 238.53) * mm, v(419.36, 237.8) * mm, v(419.9, 236.91) * mm]});
            skFitSpline(sketch, "E769", {"points": [v(419.9, 236.91) * mm, v(420.66, 235.7) * mm, v(423.18, 235.48) * mm, v(430.25, 236.05) * mm]});
            skFitSpline(sketch, "E770", {"points": [v(430.25, 236.05) * mm, v(440.38, 236.86) * mm, v(444.47, 235.67) * mm, v(444.47, 231.91) * mm]});
            skFitSpline(sketch, "E771", {"points": [v(444.47, 231.91) * mm, v(444.47, 229.15) * mm, v(447.28, 228.5) * mm, v(457.92, 228.74) * mm]});
            skFitSpline(sketch, "E772", {"points": [v(457.92, 228.74) * mm, v(463.57, 228.87) * mm, v(467.02, 228.28) * mm, v(469.87, 226.7) * mm]});
            skFitSpline(sketch, "E773", {"points": [v(469.87, 226.7) * mm, v(475.1, 223.82) * mm, v(475.1, 223.82) * mm, v(474.73, 228.46) * mm]});
            skFitSpline(sketch, "E774", {"points": [v(474.73, 228.46) * mm, v(474.5, 231.5) * mm, v(474.85, 232.32) * mm, v(476.25, 231.94) * mm]});
            skFitSpline(sketch, "E775", {"points": [v(476.25, 231.94) * mm, v(477.26, 231.66) * mm, v(482.76, 230.98) * mm, v(488.47, 230.41) * mm]});
            skFitSpline(sketch, "E776", {"points": [v(488.47, 230.41) * mm, v(503.77, 228.9) * mm, v(520.15, 220.62) * mm, v(520.33, 214.3) * mm]});
            skFitSpline(sketch, "E777", {"points": [v(520.33, 214.3) * mm, v(520.4, 211.66) * mm, v(520.4, 211.66) * mm, v(521.51, 214.4) * mm]});
            skFitSpline(sketch, "E778", {"points": [v(521.51, 214.4) * mm, v(522.87, 217.78) * mm, v(523.4, 217.8) * mm, v(530.56, 214.62) * mm]});
            skFitSpline(sketch, "E779", {"points": [v(530.56, 214.62) * mm, v(536.8, 211.86) * mm, v(536.72, 210.19) * mm, v(530.18, 207.05) * mm]});
            skFitSpline(sketch, "E780", {"points": [v(530.18, 207.05) * mm, v(528.4, 206.19) * mm, v(526.97, 204.48) * mm, v(526.97, 203.18) * mm]});
            skFitSpline(sketch, "E781", {"points": [v(526.97, 203.18) * mm, v(525.99, 198.35) * mm, v(518.36, 203.58) * mm, v(516.01, 206.12) * mm]});
            skFitSpline(sketch, "E782", {"points": [v(516.01, 206.12) * mm, v(514.37, 207.93) * mm, v(513.3, 208.23) * mm, v(511.62, 207.34) * mm]});
            skFitSpline(sketch, "E783", {"points": [v(511.62, 207.34) * mm, v(508.5, 205.67) * mm, v(508.1, 205.81) * mm, v(506.85, 208.9) * mm]});
            skFitSpline(sketch, "E784", {"points": [v(506.85, 208.9) * mm, v(505.78, 211.56) * mm, v(505.74, 211.54) * mm, v(505.66, 208.34) * mm]});
            skFitSpline(sketch, "E785", {"points": [v(505.66, 208.34) * mm, v(505.56, 204.03) * mm, v(502.05, 202.04) * mm, v(497.55, 203.75) * mm]});
            skFitSpline(sketch, "E786", {"points": [v(497.55, 203.75) * mm, v(495.73, 204.44) * mm, v(493.97, 204.73) * mm, v(493.64, 204.4) * mm]});
            skFitSpline(sketch, "E787", {"points": [v(493.64, 204.4) * mm, v(493.3, 204.06) * mm, v(494.42, 203.25) * mm, v(496.12, 202.6) * mm]});
            skFitSpline(sketch, "E788", {"points": [v(496.12, 202.6) * mm, v(497.82, 201.96) * mm, v(500.11, 199.64) * mm, v(501.2, 197.44) * mm]});
            skFitSpline(sketch, "E789", {"points": [v(501.2, 197.44) * mm, v(502.92, 194.01) * mm, v(502.95, 193.22) * mm, v(501.46, 191.73) * mm]});
            skFitSpline(sketch, "E790", {"points": [v(501.46, 191.73) * mm, v(500.2, 190.48) * mm, v(499.13, 190.34) * mm, v(497.53, 191.24) * mm]});
            skFitSpline(sketch, "E791", {"points": [v(497.53, 191.24) * mm, v(495, 192.65) * mm, v(484.54, 188.55) * mm, v(478.03, 183.58) * mm]});
            skFitSpline(sketch, "E792", {"points": [v(478.03, 183.58) * mm, v(474.53, 180.92) * mm, v(474, 180.82) * mm, v(472.26, 182.56) * mm]});
            skFitSpline(sketch, "E793", {"points": [v(472.26, 182.56) * mm, v(470.87, 183.95) * mm, v(469.4, 184.2) * mm, v(466.88, 183.5) * mm]});
            skFitSpline(sketch, "E794", {"points": [v(466.88, 183.5) * mm, v(464.98, 182.97) * mm, v(462.95, 182.64) * mm, v(462.37, 182.78) * mm]});
            skFitSpline(sketch, "E795", {"points": [v(462.37, 182.78) * mm, v(461.8, 182.91) * mm, v(460.49, 182.32) * mm, v(459.46, 181.47) * mm]});
            skFitSpline(sketch, "E796", {"points": [v(459.46, 181.47) * mm, v(458.43, 180.61) * mm, v(456.75, 179.9) * mm, v(455.72, 179.9) * mm]});
            skFitSpline(sketch, "E797", {"points": [v(455.72, 179.9) * mm, v(454.7, 179.89) * mm, v(453.6, 179.12) * mm, v(453.28, 178.18) * mm]});
            skFitSpline(sketch, "E798", {"points": [v(453.28, 178.18) * mm, v(452.95, 177.2) * mm, v(453.26, 176.82) * mm, v(454, 177.29) * mm]});
            skFitSpline(sketch, "E799", {"points": [v(454, 177.29) * mm, v(454.72, 177.73) * mm, v(455.63, 177.57) * mm, v(456.02, 176.93) * mm]});
            skFitSpline(sketch, "E800", {"points": [v(456.02, 176.93) * mm, v(456.41, 176.3) * mm, v(456.22, 175.45) * mm, v(455.58, 175.05) * mm]});
            skFitSpline(sketch, "E801", {"points": [v(455.58, 175.05) * mm, v(454.94, 174.66) * mm, v(454.04, 174.96) * mm, v(453.57, 175.71) * mm]});
            skFitSpline(sketch, "E802", {"points": [v(453.57, 175.71) * mm, v(452.97, 176.7) * mm, v(452.44, 176.62) * mm, v(451.72, 175.47) * mm]});
            skFitSpline(sketch, "E803", {"points": [v(451.72, 175.47) * mm, v(451.16, 174.56) * mm, v(451.3, 173.15) * mm, v(452.05, 172.25) * mm]});
            skFitSpline(sketch, "E804", {"points": [v(452.05, 172.25) * mm, v(452.78, 171.37) * mm, v(453.03, 170.3) * mm, v(452.6, 169.88) * mm]});
            skFitSpline(sketch, "E805", {"points": [v(452.6, 169.88) * mm, v(452.18, 169.45) * mm, v(452.42, 168.4) * mm, v(453.14, 167.52) * mm]});
            skFitSpline(sketch, "E806", {"points": [v(453.14, 167.52) * mm, v(454.62, 165.74) * mm, v(453.48, 162.95) * mm, v(451.72, 164.04) * mm]});
            skFitSpline(sketch, "E807", {"points": [v(451.72, 164.04) * mm, v(450.6, 164.73) * mm, v(450.35, 163.95) * mm, v(450.1, 159.1) * mm]});
            skFitSpline(sketch, "E808", {"points": [v(450.1, 159.1) * mm, v(450.02, 157.52) * mm, v(449.24, 156.78) * mm, v(447.9, 157) * mm]});
            skFitSpline(sketch, "E809", {"points": [v(447.9, 157) * mm, v(445.63, 157.38) * mm, v(442.68, 153.06) * mm, v(443.88, 151.12) * mm]});
            skFitSpline(sketch, "E810", {"points": [v(443.88, 151.12) * mm, v(444.3, 150.46) * mm, v(443.68, 149.55) * mm, v(442.51, 149.1) * mm]});
            skFitSpline(sketch, "E811", {"points": [v(442.51, 149.1) * mm, v(441.35, 148.66) * mm, v(438.88, 146.6) * mm, v(437.03, 144.53) * mm]});
            skFitSpline(sketch, "E812", {"points": [v(437.03, 144.53) * mm, v(435.9, 143.28) * mm, v(434.78, 142.02) * mm, v(433.66, 140.77) * mm]});
            skFitSpline(sketch, "E813", {"points": [v(433.66, 140.77) * mm, v(433.18, 142) * mm, v(432.7, 143.21) * mm, v(432.21, 144.44) * mm]});
            skFitSpline(sketch, "E814", {"points": [v(432.21, 144.44) * mm, v(431.42, 146.45) * mm, v(430.48, 151.5) * mm, v(430.13, 155.64) * mm]});
            skFitSpline(sketch, "E815", {"points": [v(430.13, 155.64) * mm, v(429.59, 162) * mm, v(429.91, 163.87) * mm, v(432.2, 167.56) * mm]});
            skFitSpline(sketch, "E816", {"points": [v(432.2, 167.56) * mm, v(433.68, 169.97) * mm, v(435.52, 171.94) * mm, v(436.28, 171.94) * mm]});
            skFitSpline(sketch, "E817", {"points": [v(436.28, 171.94) * mm, v(437.93, 171.94) * mm, v(448.14, 181.75) * mm, v(448.14, 183.34) * mm]});
            skFitSpline(sketch, "E818", {"points": [v(448.14, 183.34) * mm, v(448.14, 183.95) * mm, v(447.32, 183.78) * mm, v(446.32, 182.95) * mm]});
            skFitSpline(sketch, "E819", {"points": [v(446.32, 182.95) * mm, v(444.85, 181.72) * mm, v(444.36, 181.81) * mm, v(443.74, 183.42) * mm]});
            skFitSpline(sketch, "E820", {"points": [v(443.74, 183.42) * mm, v(443.32, 184.52) * mm, v(443.67, 186.24) * mm, v(444.51, 187.26) * mm]});
            skFitSpline(sketch, "E821", {"points": [v(444.51, 187.26) * mm, v(445.84, 188.86) * mm, v(445.48, 189.07) * mm, v(441.84, 188.78) * mm]});
            skFitSpline(sketch, "E822", {"points": [v(441.84, 188.78) * mm, v(437.15, 188.4) * mm, v(426.22, 180.12) * mm, v(428.53, 178.7) * mm]});
            skFitSpline(sketch, "E823", {"points": [v(428.53, 178.7) * mm, v(432.94, 175.97) * mm, v(421.53, 175.2) * mm, v(416.59, 177.9) * mm]});
            skFitSpline(sketch, "E824", {"points": [v(416.59, 177.9) * mm, v(414.72, 178.92) * mm, v(413.27, 179.03) * mm, v(412.31, 178.24) * mm]});
            skFitSpline(sketch, "E825", {"points": [v(412.31, 178.24) * mm, v(410.51, 176.76) * mm, v(402.14, 175.97) * mm, v(400.95, 177.17) * mm]});
            skFitSpline(sketch, "E826", {"points": [v(400.95, 177.17) * mm, v(398.2, 179.9) * mm, v(392.94, 177.68) * mm, v(383.78, 169.91) * mm]});
            skFitSpline(sketch, "E827", {"points": [v(383.78, 169.91) * mm, v(371.75, 159.7) * mm, v(370.27, 157.78) * mm, v(373.73, 156.88) * mm]});
            skFitSpline(sketch, "E828", {"points": [v(373.73, 156.88) * mm, v(375.2, 156.5) * mm, v(375.92, 155.64) * mm, v(375.43, 154.85) * mm]});
            skFitSpline(sketch, "E829", {"points": [v(375.43, 154.85) * mm, v(374.48, 153.3) * mm, v(379.27, 153.63) * mm, v(381.91, 155.28) * mm]});
            skFitSpline(sketch, "E830", {"points": [v(381.91, 155.28) * mm, v(383.85, 156.5) * mm, v(388.25, 152.88) * mm, v(388.26, 150.05) * mm]});
            skFitSpline(sketch, "E831", {"points": [v(388.26, 150.05) * mm, v(388.26, 148.94) * mm, v(389.04, 149.58) * mm, v(390.06, 151.55) * mm]});
            skFitSpline(sketch, "E832", {"points": [v(390.06, 151.55) * mm, v(391.05, 153.44) * mm, v(391.74, 155.64) * mm, v(391.58, 156.44) * mm]});
            skFitSpline(sketch, "E833", {"points": [v(391.58, 156.44) * mm, v(391.43, 157.23) * mm, v(392.13, 157.88) * mm, v(393.14, 157.88) * mm]});
            skFitSpline(sketch, "E834", {"points": [v(393.14, 157.88) * mm, v(394.48, 157.88) * mm, v(394.89, 156.73) * mm, v(394.65, 153.6) * mm]});
            skFitSpline(sketch, "E835", {"points": [v(394.65, 153.6) * mm, v(394.3, 148.79) * mm, v(396.63, 136.66) * mm, v(398.34, 134.4) * mm]});
            skFitSpline(sketch, "E836", {"points": [v(398.34, 134.4) * mm, v(400.05, 132.15) * mm, v(398.2, 129.93) * mm, v(396.09, 131.7) * mm]});
            skFitSpline(sketch, "E837", {"points": [v(396.09, 131.7) * mm, v(394.67, 132.87) * mm, v(394.36, 132.49) * mm, v(394.36, 129.55) * mm]});
            skFitSpline(sketch, "E838", {"points": [v(394.36, 129.55) * mm, v(394.36, 127.59) * mm, v(394.98, 125.36) * mm, v(395.75, 124.6) * mm]});
            skFitSpline(sketch, "E839", {"points": [v(395.75, 124.6) * mm, v(397.68, 122.66) * mm, v(396.19, 119.5) * mm, v(393.52, 119.9) * mm]});
            skFitSpline(sketch, "E840", {"points": [v(393.52, 119.9) * mm, v(391.6, 120.18) * mm, v(391.29, 121.59) * mm, v(391.16, 130.63) * mm]});
            skFitSpline(sketch, "E841", {"points": [v(391.16, 130.63) * mm, v(391, 141.58) * mm, v(389.05, 148.54) * mm, v(387.8, 142.58) * mm]});
            skFitSpline(sketch, "E842", {"points": [v(387.8, 142.58) * mm, v(387.46, 140.91) * mm, v(386.83, 137.45) * mm, v(386.42, 134.9) * mm]});
            skFitSpline(sketch, "E843", {"points": [v(386.42, 134.9) * mm, v(385.6, 129.8) * mm, v(381.66, 123.04) * mm, v(374.3, 114.07) * mm]});
            skFitSpline(sketch, "E844", {"points": [v(374.3, 114.07) * mm, v(368.44, 106.94) * mm, v(365.56, 105.2) * mm, v(363.06, 107.27) * mm]});
            skFitSpline(sketch, "E845", {"points": [v(363.06, 107.27) * mm, v(361.56, 108.51) * mm, v(360.48, 107.86) * mm, v(356.72, 103.47) * mm]});
            skFitSpline(sketch, "E846", {"points": [v(356.72, 103.47) * mm, v(354.23, 100.55) * mm, v(351.28, 97.2) * mm, v(350.16, 96.04) * mm]});
            skFitSpline(sketch, "E847", {"points": [v(350.16, 96.04) * mm, v(348.25, 94.05) * mm, v(348.32, 93.43) * mm, v(351.15, 86.4) * mm]});
            skFitSpline(sketch, "E848", {"points": [v(351.15, 86.4) * mm, v(354.5, 78.1) * mm, v(354.03, 76.26) * mm, v(348.17, 74.79) * mm]});
            skFitSpline(sketch, "E849", {"points": [v(348.17, 74.79) * mm, v(343.58, 73.64) * mm, v(343.64, 73.58) * mm, v(343.64, 79.02) * mm]});
            skFitSpline(sketch, "E850", {"points": [v(343.64, 79.02) * mm, v(343.64, 82.68) * mm, v(342.96, 84.36) * mm, v(340.88, 85.82) * mm]});
            skFitSpline(sketch, "E851", {"points": [v(340.88, 85.82) * mm, v(338.72, 87.33) * mm, v(338.39, 88.23) * mm, v(339.33, 90) * mm]});
            skFitSpline(sketch, "E852", {"points": [v(339.33, 90) * mm, v(341.59, 94.2) * mm, v(333.6, 95.29) * mm, v(331, 91.12) * mm]});
            skFitSpline(sketch, "E853", {"points": [v(331, 91.12) * mm, v(329.85, 89.29) * mm, v(329, 88.91) * mm, v(328.08, 89.84) * mm]});
            skFitSpline(sketch, "E854", {"points": [v(328.08, 89.84) * mm, v(327.15, 90.76) * mm, v(327.34, 92.01) * mm, v(328.73, 94.12) * mm]});
            skFitSpline(sketch, "E855", {"points": [v(328.73, 94.12) * mm, v(329.8, 95.76) * mm, v(330.36, 97.42) * mm, v(329.97, 97.8) * mm]});
            skFitSpline(sketch, "E856", {"points": [v(329.97, 97.8) * mm, v(329.05, 98.72) * mm, v(318.58, 91.24) * mm, v(318.58, 89.67) * mm]});
            skFitSpline(sketch, "E857", {"points": [v(318.58, 89.67) * mm, v(318.58, 87.04) * mm, v(322.94, 85.32) * mm, v(327.9, 85.99) * mm]});
            skFitSpline(sketch, "E858", {"points": [v(327.9, 85.99) * mm, v(334.47, 86.87) * mm, v(335.96, 84.59) * mm, v(330.34, 82.24) * mm]});
            skFitSpline(sketch, "E859", {"points": [v(330.34, 82.24) * mm, v(323.45, 79.36) * mm, v(322.66, 76.32) * mm, v(327.1, 69.74) * mm]});
            skFitSpline(sketch, "E860", {"points": [v(327.1, 69.74) * mm, v(330.84, 64.2) * mm, v(330.85, 64.16) * mm, v(328.18, 63.46) * mm]});
            skFitSpline(sketch, "E861", {"points": [v(328.18, 63.46) * mm, v(325.5, 62.76) * mm, v(325.5, 62.76) * mm, v(328.45, 61.65) * mm]});
            skFitSpline(sketch, "E862", {"points": [v(328.45, 61.65) * mm, v(331.34, 60.57) * mm, v(331.35, 60.5) * mm, v(329.04, 58.8) * mm]});
            skFitSpline(sketch, "E863", {"points": [v(329.04, 58.8) * mm, v(327.74, 57.83) * mm, v(327.34, 57.04) * mm, v(328.17, 57.04) * mm]});
            skFitSpline(sketch, "E864", {"points": [v(328.17, 57.04) * mm, v(331.14, 57.04) * mm, v(331, 53.26) * mm, v(327.88, 49.17) * mm]});
            skFitSpline(sketch, "E865", {"points": [v(327.88, 49.17) * mm, v(326.13, 46.87) * mm, v(324.67, 44.26) * mm, v(324.65, 43.38) * mm]});
            skFitSpline(sketch, "E866", {"points": [v(324.65, 43.38) * mm, v(324.62, 42.5) * mm, v(321.96, 38.94) * mm, v(318.74, 35.49) * mm]});
            skFitSpline(sketch, "E867", {"points": [v(318.74, 35.49) * mm, v(313.91, 30.31) * mm, v(311.94, 29.08) * mm, v(307.54, 28.46) * mm]});
            skFitSpline(sketch, "E868", {"points": [v(307.54, 28.46) * mm, v(304.6, 28.05) * mm, v(301.66, 27.16) * mm, v(300.98, 26.49) * mm]});
            skFitSpline(sketch, "E869", {"points": [v(300.98, 26.49) * mm, v(300.31, 25.82) * mm, v(298.83, 25.27) * mm, v(297.7, 25.27) * mm]});
            skFitSpline(sketch, "E870", {"points": [v(297.7, 25.27) * mm, v(296.55, 25.27) * mm, v(295.28, 24.37) * mm, v(294.85, 23.27) * mm]});
            skFitSpline(sketch, "E871", {"points": [v(294.85, 23.27) * mm, v(294.15, 21.44) * mm, v(293.88, 21.45) * mm, v(291.72, 23.4) * mm]});
            skFitSpline(sketch, "E872", {"points": [v(291.72, 23.4) * mm, v(289.44, 25.47) * mm, v(289.2, 25.4) * mm, v(285.5, 21.71) * mm]});
            skFitSpline(sketch, "E873", {"points": [v(285.5, 21.71) * mm, v(282.09, 18.3) * mm, v(281.84, 17.6) * mm, v(283.32, 15.52) * mm]});
            skFitSpline(sketch, "E874", {"points": [v(283.32, 15.52) * mm, v(284.23, 14.23) * mm, v(286.58, 10.91) * mm, v(288.54, 8.16) * mm]});
            skFitSpline(sketch, "E875", {"points": [v(288.54, 8.16) * mm, v(291.13, 4.52) * mm, v(292.27, 1.28) * mm, v(292.67, -3.59) * mm]});
            skFitSpline(sketch, "E876", {"points": [v(292.67, -3.59) * mm, v(292.86, -5.83) * mm, v(293.04, -8.07) * mm, v(293.23, -10.31) * mm]});
            skFitSpline(sketch, "E877", {"points": [v(293.23, -10.31) * mm, v(291.04, -12.28) * mm, v(288.85, -14.25) * mm, v(286.66, -16.23) * mm]});
            skFitSpline(sketch, "E878", {"points": [v(286.66, -16.23) * mm, v(283.04, -19.48) * mm, v(279.67, -21.89) * mm, v(279.16, -21.58) * mm]});
            skFitSpline(sketch, "E879", {"points": [v(279.16, -21.58) * mm, v(278.66, -21.28) * mm, v(278.25, -19.71) * mm, v(278.25, -18.1) * mm]});
            skFitSpline(sketch, "E880", {"points": [v(278.25, -18.1) * mm, v(278.25, -16.4) * mm, v(277.2, -14.6) * mm, v(275.8, -13.85) * mm]});
            skFitSpline(sketch, "E881", {"points": [v(275.8, -13.85) * mm, v(274.46, -13.13) * mm, v(273.36, -11.46) * mm, v(273.36, -10.14) * mm]});
            skFitSpline(sketch, "E882", {"points": [v(273.36, -10.14) * mm, v(273.36, -8.58) * mm, v(272.53, -7.73) * mm, v(271.01, -7.73) * mm]});
            skFitSpline(sketch, "E883", {"points": [v(271.01, -7.73) * mm, v(269.73, -7.73) * mm, v(267.92, -7.45) * mm, v(267, -7.1) * mm]});
            skFitSpline(sketch, "E884", {"points": [v(267, -7.1) * mm, v(265.84, -6.65) * mm, v(264.86, -8.21) * mm, v(263.79, -12.2) * mm]});
            skFitSpline(sketch, "E885", {"points": [v(263.79, -12.2) * mm, v(262.49, -17.07) * mm, v(262.52, -18.12) * mm, v(264, -18.94) * mm]});
            skFitSpline(sketch, "E886", {"points": [v(264, -18.94) * mm, v(264.96, -19.48) * mm, v(266.11, -21.35) * mm, v(266.55, -23.1) * mm]});
            skFitSpline(sketch, "E887", {"points": [v(266.55, -23.1) * mm, v(266.99, -24.84) * mm, v(268.8, -27.53) * mm, v(270.6, -29.07) * mm]});
            skFitSpline(sketch, "E888", {"points": [v(270.6, -29.07) * mm, v(274.1, -32.08) * mm, v(277.75, -44.09) * mm, v(275.78, -46.11) * mm]});
            skFitSpline(sketch, "E889", {"points": [v(275.78, -46.11) * mm, v(272.92, -49.05) * mm, v(263.58, -36.82) * mm, v(263.58, -30.13) * mm]});
            skFitSpline(sketch, "E890", {"points": [v(263.58, -30.13) * mm, v(263.58, -29.12) * mm, v(262.51, -26.93) * mm, v(261.21, -25.27) * mm]});
            skFitSpline(sketch, "E891", {"points": [v(261.21, -25.27) * mm, v(259.22, -22.75) * mm, v(258.93, -20.89) * mm, v(259.42, -13.87) * mm]});
            skFitSpline(sketch, "E892", {"points": [v(259.42, -13.87) * mm, v(259.75, -9.11) * mm, v(259.5, -5.17) * mm, v(258.82, -4.76) * mm]});
            skFitSpline(sketch, "E893", {"points": [v(258.82, -4.76) * mm, v(258.17, -4.36) * mm, v(257.27, -1.07) * mm, v(256.82, 2.55) * mm]});
            skFitSpline(sketch, "E894", {"points": [v(256.82, 2.55) * mm, v(256, 9.08) * mm, v(255.98, 9.1) * mm, v(253.6, 6.73) * mm]});
            skFitSpline(sketch, "E895", {"points": [v(253.6, 6.73) * mm, v(252.29, 5.41) * mm, v(250.02, 4.5) * mm, v(248.57, 4.72) * mm]});
            skFitSpline(sketch, "E896", {"points": [v(248.57, 4.72) * mm, v(246.24, 5.05) * mm, v(245.97, 5.76) * mm, v(246.29, 10.78) * mm]});
            skFitSpline(sketch, "E897", {"points": [v(246.29, 10.78) * mm, v(246.56, 15.12) * mm, v(246.08, 17) * mm, v(244.27, 18.72) * mm]});
            skFitSpline(sketch, "E898", {"points": [v(244.27, 18.72) * mm, v(242.96, 19.97) * mm, v(240.96, 22.83) * mm, v(239.81, 25.07) * mm]});
            skFitSpline(sketch, "E899", {"points": [v(239.81, 25.07) * mm, v(237.89, 28.86) * mm, v(237.58, 29.01) * mm, v(235.6, 27.2) * mm]});
            skFitSpline(sketch, "E900", {"points": [v(235.6, 27.2) * mm, v(234.41, 26.14) * mm, v(231.7, 25.27) * mm, v(229.57, 25.27) * mm]});
            skFitSpline(sketch, "E901", {"points": [v(229.57, 25.27) * mm, v(227.28, 25.27) * mm, v(225.7, 24.64) * mm, v(225.7, 23.74) * mm]});
            skFitSpline(sketch, "E902", {"points": [v(225.7, 23.74) * mm, v(225.69, 21.9) * mm, v(208.06, 4.49) * mm, v(206.2, 4.49) * mm]});
            skFitSpline(sketch, "E903", {"points": [v(206.2, 4.49) * mm, v(205.46, 4.49) * mm, v(204.91, 1.77) * mm, v(204.9, -1.93) * mm]});
            skFitSpline(sketch, "E904", {"points": [v(204.9, -1.93) * mm, v(204.9, -10.17) * mm, v(203.06, -16.69) * mm, v(199.62, -20.68) * mm]});
            skFitSpline(sketch, "E905", {"points": [v(199.62, -20.68) * mm, v(198.71, -21.74) * mm, v(197.8, -22.8) * mm, v(196.9, -23.86) * mm]});
            skFitSpline(sketch, "E906", {"points": [v(196.9, -23.86) * mm, v(195.38, -20.87) * mm, v(193.86, -17.87) * mm, v(192.34, -14.88) * mm]});
            skFitSpline(sketch, "E907", {"points": [v(192.34, -14.88) * mm, v(189.84, -9.94) * mm, v(187.8, -4.97) * mm, v(187.8, -3.83) * mm]});
            skFitSpline(sketch, "E908", {"points": [v(187.8, -3.83) * mm, v(187.8, -2.7) * mm, v(187.32, -1.47) * mm, v(186.73, -1.1) * mm]});
            skFitSpline(sketch, "E909", {"points": [v(186.73, -1.1) * mm, v(186.14, -0.74) * mm, v(184.96, 2.18) * mm, v(184.1, 5.38) * mm]});
            skFitSpline(sketch, "E910", {"points": [v(184.1, 5.38) * mm, v(183.24, 8.59) * mm, v(182.3, 12.04) * mm, v(182.02, 13.04) * mm]});
            skFitSpline(sketch, "E911", {"points": [v(182.02, 13.04) * mm, v(181.73, 14.05) * mm, v(181.52, 17.9) * mm, v(181.54, 21.6) * mm]});
            skFitSpline(sketch, "E912", {"points": [v(181.54, 21.6) * mm, v(181.56, 26.84) * mm, v(181.32, 27.72) * mm, v(180.45, 25.57) * mm]});
            skFitSpline(sketch, "E913", {"points": [v(180.45, 25.57) * mm, v(179.08, 22.2) * mm, v(176.65, 22.05) * mm, v(173.85, 25.16) * mm]});
            skFitSpline(sketch, "E914", {"points": [v(173.85, 25.16) * mm, v(171.85, 27.37) * mm, v(171.85, 27.55) * mm, v(173.86, 28.68) * mm]});
            skFitSpline(sketch, "E915", {"points": [v(173.86, 28.68) * mm, v(175.68, 29.7) * mm, v(175.43, 30) * mm, v(172.16, 30.71) * mm]});
            skFitSpline(sketch, "E916", {"points": [v(172.16, 30.71) * mm, v(170.05, 31.18) * mm, v(167.29, 32.97) * mm, v(166.03, 34.7) * mm]});
            skFitSpline(sketch, "E917", {"points": [v(166.03, 34.7) * mm, v(163.91, 37.6) * mm, v(162.94, 37.87) * mm, v(153.46, 38.12) * mm]});
            skFitSpline(sketch, "E918", {"points": [v(153.46, 38.12) * mm, v(142.19, 38.41) * mm, v(136.47, 40.06) * mm, v(136.47, 43.01) * mm]});
            skFitSpline(sketch, "E919", {"points": [v(136.47, 43.01) * mm, v(136.47, 44.54) * mm, v(135.6, 44.77) * mm, v(132.22, 44.14) * mm]});
            skFitSpline(sketch, "E920", {"points": [v(132.22, 44.14) * mm, v(128.65, 43.47) * mm, v(127.22, 43.94) * mm, v(123.12, 47.19) * mm]});
            skFitSpline(sketch, "E921", {"points": [v(123.12, 47.19) * mm, v(120.45, 49.3) * mm, v(117.94, 52.05) * mm, v(117.55, 53.3) * mm]});
            skFitSpline(sketch, "E922", {"points": [v(117.55, 53.3) * mm, v(116.76, 55.79) * mm, v(113.08, 57.23) * mm, v(110.91, 55.9) * mm]});
            skFitSpline(sketch, "E923", {"points": [v(110.91, 55.9) * mm, v(109.98, 55.31) * mm, v(110.72, 53.29) * mm, v(113.2, 49.62) * mm]});
            skFitSpline(sketch, "E924", {"points": [v(113.2, 49.62) * mm, v(115.22, 46.65) * mm, v(116.88, 43.32) * mm, v(116.9, 42.22) * mm]});
            skFitSpline(sketch, "E925", {"points": [v(116.9, 42.22) * mm, v(116.9, 41.13) * mm, v(117.74, 39.55) * mm, v(118.75, 38.71) * mm]});
            skFitSpline(sketch, "E926", {"points": [v(118.75, 38.71) * mm, v(119.75, 37.87) * mm, v(120.58, 36.37) * mm, v(120.58, 35.37) * mm]});
            skFitSpline(sketch, "E927", {"points": [v(120.58, 35.37) * mm, v(120.58, 34.22) * mm, v(121.28, 33.83) * mm, v(122.51, 34.3) * mm]});
            skFitSpline(sketch, "E928", {"points": [v(122.51, 34.3) * mm, v(123.58, 34.71) * mm, v(125, 35.04) * mm, v(125.69, 35.04) * mm]});
            skFitSpline(sketch, "E929", {"points": [v(125.69, 35.04) * mm, v(126.37, 35.04) * mm, v(128.5, 36.73) * mm, v(130.43, 38.79) * mm]});
            skFitSpline(sketch, "E930", {"points": [v(130.43, 38.79) * mm, v(131.6, 40.04) * mm, v(133.66, 43.18) * mm, v(133.93, 42.53) * mm]});
            skFitSpline(sketch, "E931", {"points": [v(133.93, 42.53) * mm, v(134.53, 41.08) * mm, v(135.14, 39.63) * mm, v(135.75, 38.18) * mm]});
            skFitSpline(sketch, "E932", {"points": [v(135.75, 38.18) * mm, v(136.75, 35.78) * mm, v(138.07, 33.82) * mm, v(138.69, 33.82) * mm]});
            skFitSpline(sketch, "E933", {"points": [v(138.69, 33.82) * mm, v(139.3, 33.82) * mm, v(141.28, 32.66) * mm, v(143.1, 31.24) * mm]});
            skFitSpline(sketch, "E934", {"points": [v(143.1, 31.24) * mm, v(146.17, 28.82) * mm, v(146.25, 28.52) * mm, v(144.36, 26.43) * mm]});
            skFitSpline(sketch, "E935", {"points": [v(144.36, 26.43) * mm, v(143.25, 25.2) * mm, v(142.68, 23.64) * mm, v(143.1, 22.96) * mm]});
            skFitSpline(sketch, "E936", {"points": [v(143.1, 22.96) * mm, v(143.53, 22.28) * mm, v(142.76, 21.13) * mm, v(141.4, 20.4) * mm]});
            skFitSpline(sketch, "E937", {"points": [v(141.4, 20.4) * mm, v(140.05, 19.68) * mm, v(139.07, 18.66) * mm, v(139.23, 18.14) * mm]});
            skFitSpline(sketch, "E938", {"points": [v(139.23, 18.14) * mm, v(139.61, 16.9) * mm, v(131.3, 9.6) * mm, v(126.31, 6.8) * mm]});
            skFitSpline(sketch, "E939", {"points": [v(126.31, 6.8) * mm, v(124.17, 5.6) * mm, v(118.29, 2.62) * mm, v(113.25, 0.17) * mm]});
            skFitSpline(sketch, "E940", {"points": [v(113.25, 0.17) * mm, v(108.2, -2.27) * mm, v(103.12, -4.77) * mm, v(101.96, -5.4) * mm]});
            skFitSpline(sketch, "E941", {"points": [v(101.96, -5.4) * mm, v(96.54, -8.25) * mm, v(93.66, -4.71) * mm, v(93.15, 5.43) * mm]});
            skFitSpline(sketch, "E942", {"points": [v(93.15, 5.43) * mm, v(92.97, 9.05) * mm, v(91.94, 11.66) * mm, v(89.8, 13.98) * mm]});
            skFitSpline(sketch, "E943", {"points": [v(89.8, 13.98) * mm, v(84.67, 19.56) * mm, v(82.7, 23.19) * mm, v(82.67, 27.07) * mm]});
            skFitSpline(sketch, "E944", {"points": [v(82.67, 27.07) * mm, v(82.65, 31.36) * mm, v(81.7, 33.08) * mm, v(78.72, 34.18) * mm]});
            skFitSpline(sketch, "E945", {"points": [v(78.72, 34.18) * mm, v(77.54, 34.61) * mm, v(76.58, 36.02) * mm, v(76.58, 37.31) * mm]});
            skFitSpline(sketch, "E946", {"points": [v(76.58, 37.31) * mm, v(76.58, 39.9) * mm, v(74.44, 45.21) * mm, v(71.74, 49.31) * mm]});
            skFitSpline(sketch, "E947", {"points": [v(71.74, 49.31) * mm, v(70.14, 51.76) * mm, v(69.87, 51.8) * mm, v(68.48, 49.93) * mm]});
            skFitSpline(sketch, "E948", {"points": [v(68.48, 49.93) * mm, v(67.11, 48.07) * mm, v(66.85, 48.17) * mm, v(65.74, 50.93) * mm]});
            skFitSpline(sketch, "E949", {"points": [v(65.74, 50.93) * mm, v(64.95, 52.89) * mm, v(64.48, 53.26) * mm, v(64.43, 51.96) * mm]});
            skFitSpline(sketch, "E950", {"points": [v(64.43, 51.96) * mm, v(64.4, 50.84) * mm, v(66.3, 46.99) * mm, v(68.67, 43.4) * mm]});
            skFitSpline(sketch, "E951", {"points": [v(68.67, 43.4) * mm, v(71.05, 39.81) * mm, v(73.33, 35.5) * mm, v(73.74, 33.82) * mm]});
            skFitSpline(sketch, "E952", {"points": [v(73.74, 33.82) * mm, v(74.16, 32.14) * mm, v(75.24, 29.68) * mm, v(76.15, 28.36) * mm]});
            skFitSpline(sketch, "E953", {"points": [v(76.15, 28.36) * mm, v(77.06, 27.03) * mm, v(77.8, 23.38) * mm, v(77.8, 20.24) * mm]});
            skFitSpline(sketch, "E954", {"points": [v(77.8, 20.24) * mm, v(77.8, 16.21) * mm, v(78.36, 14.31) * mm, v(79.7, 13.8) * mm]});
            skFitSpline(sketch, "E955", {"points": [v(79.7, 13.8) * mm, v(80.73, 13.4) * mm, v(82.16, 11.42) * mm, v(82.87, 9.4) * mm]});
            skFitSpline(sketch, "E956", {"points": [v(82.87, 9.4) * mm, v(83.57, 7.37) * mm, v(84.62, 5.71) * mm, v(85.2, 5.71) * mm]});
            skFitSpline(sketch, "E957", {"points": [v(85.2, 5.71) * mm, v(85.78, 5.71) * mm, v(87.68, 3.28) * mm, v(89.42, 0.31) * mm]});
            skFitSpline(sketch, "E958", {"points": [v(89.42, 0.31) * mm, v(91.16, -2.65) * mm, v(93.37, -5.74) * mm, v(94.34, -6.55) * mm]});
            skFitSpline(sketch, "E959", {"points": [v(94.34, -6.55) * mm, v(95.31, -7.35) * mm, v(95.84, -8.44) * mm, v(95.52, -8.96) * mm]});
            skFitSpline(sketch, "E960", {"points": [v(95.52, -8.96) * mm, v(95.2, -9.48) * mm, v(96.18, -10.73) * mm, v(97.7, -11.73) * mm]});
            skFitSpline(sketch, "E961", {"points": [v(97.7, -11.73) * mm, v(100.5, -13.56) * mm, v(102.85, -13.3) * mm, v(118.9, -9.36) * mm]});
            skFitSpline(sketch, "E962", {"points": [v(118.9, -9.36) * mm, v(122.19, -8.56) * mm, v(123.95, -11.1) * mm, v(120.96, -12.33) * mm]});
            skFitSpline(sketch, "E963", {"points": [v(120.96, -12.33) * mm, v(119.74, -12.83) * mm, v(118.6, -14.6) * mm, v(118.43, -16.29) * mm]});
            skFitSpline(sketch, "E964", {"points": [v(118.43, -16.29) * mm, v(118.01, -20.26) * mm, v(111.45, -33.78) * mm, v(106.67, -40.53) * mm]});
            skFitSpline(sketch, "E965", {"points": [v(106.67, -40.53) * mm, v(104.6, -43.44) * mm, v(100.83, -47.35) * mm, v(98.3, -49.22) * mm]});
            skFitSpline(sketch, "E966", {"points": [v(98.3, -49.22) * mm, v(90.1, -55.25) * mm, v(80.67, -71.08) * mm, v(82.83, -75.18) * mm]});
            skFitSpline(sketch, "E967", {"points": [v(82.83, -75.18) * mm, v(83.42, -76.32) * mm, v(83.91, -78.8) * mm, v(83.91, -80.72) * mm]});
            skFitSpline(sketch, "E968", {"points": [v(83.91, -80.72) * mm, v(83.91, -82.63) * mm, v(84.7, -85.3) * mm, v(85.65, -86.67) * mm]});
            skFitSpline(sketch, "E969", {"points": [v(85.65, -86.67) * mm, v(87.1, -88.74) * mm, v(88.4, -100.28) * mm, v(87.53, -103.37) * mm]});
            skFitSpline(sketch, "E970", {"points": [v(87.53, -103.37) * mm, v(87.39, -103.88) * mm, v(87.18, -104.7) * mm, v(87.08, -105.2) * mm]});
            skFitSpline(sketch, "E971", {"points": [v(87.08, -105.2) * mm, v(86.43, -108.23) * mm, v(83.2, -112.05) * mm, v(79.05, -114.66) * mm]});
            skFitSpline(sketch, "E972", {"points": [v(79.05, -114.66) * mm, v(72.13, -119.03) * mm, v(69.14, -122.58) * mm, v(70.38, -124.94) * mm]});
            skFitSpline(sketch, "E973", {"points": [v(70.38, -124.94) * mm, v(70.94, -126.02) * mm, v(71.78, -129.16) * mm, v(72.24, -131.92) * mm]});
            skFitSpline(sketch, "E974", {"points": [v(72.24, -131.92) * mm, v(73, -136.52) * mm, v(72.74, -137.22) * mm, v(69.23, -140.17) * mm]});
            skFitSpline(sketch, "E975", {"points": [v(69.23, -140.17) * mm, v(67.12, -141.95) * mm, v(65.02, -143.4) * mm, v(64.57, -143.41) * mm]});
            skFitSpline(sketch, "E976", {"points": [v(64.57, -143.41) * mm, v(64.11, -143.42) * mm, v(63.68, -145.75) * mm, v(63.6, -148.6) * mm]});
            skFitSpline(sketch, "E977", {"points": [v(63.6, -148.6) * mm, v(63.44, -154.17) * mm, v(60.45, -159.91) * mm, v(53.46, -168.02) * mm]});
            skFitSpline(sketch, "E978", {"points": [v(53.46, -168.02) * mm, v(48.06, -174.29) * mm, v(46, -175.31) * mm, v(36.32, -176.5) * mm]});
            skFitSpline(sketch, "E979", {"points": [v(36.32, -176.5) * mm, v(31.9, -177.04) * mm, v(27.14, -177.83) * mm, v(25.73, -178.26) * mm]});
            skFitSpline(sketch, "E980", {"points": [v(25.73, -178.26) * mm, v(23.88, -178.82) * mm, v(22.02, -178) * mm, v(19.1, -175.32) * mm]});
            skFitSpline(sketch, "E981", {"points": [v(19.1, -175.32) * mm, v(19.1, -175.32) * mm, v(19.1, -175.32) * mm, v(19.1, -175.32) * mm]});
            skFitSpline(sketch, "E982", {"points": [v(19.1, -175.32) * mm, v(15.66, -172.19) * mm, v(15.35, -171.49) * mm, v(17.08, -170.82) * mm]});
            skFitSpline(sketch, "E983", {"points": [v(17.08, -170.82) * mm, v(19.99, -169.7) * mm, v(19.73, -168.47) * mm, v(14.36, -158.11) * mm]});
            skFitSpline(sketch, "E984", {"points": [v(14.36, -158.11) * mm, v(9.46, -148.65) * mm, v(7.5, -142.78) * mm, v(6.42, -134.24) * mm]});
            skFitSpline(sketch, "E985", {"points": [v(6.42, -134.24) * mm, v(5.56, -127.46) * mm, v(4.59, -124.08) * mm, v(1.7, -117.9) * mm]});
            skFitSpline(sketch, "E986", {"points": [v(1.7, -117.9) * mm, v(-0.5, -113.18) * mm, v(-0.61, -111.86) * mm, v(0.63, -106.45) * mm]});
            skFitSpline(sketch, "E987", {"points": [v(0.63, -106.45) * mm, v(1.41, -103.08) * mm, v(2.93, -98.47) * mm, v(4, -96.2) * mm]});
            skFitSpline(sketch, "E988", {"points": [v(4, -96.2) * mm, v(5.26, -93.55) * mm, v(5.67, -90.85) * mm, v(5.12, -88.7) * mm]});
            skFitSpline(sketch, "E989", {"points": [v(5.12, -88.7) * mm, v(4.07, -84.88) * mm, v(4.84, -80) * mm, v(2.23, -76.97) * mm]});
            skFitSpline(sketch, "E990", {"points": [v(2.23, -76.97) * mm, v(1.1, -75.72) * mm, v(0.26, -74.35) * mm, v(0.35, -73.91) * mm]});
            skFitSpline(sketch, "E991", {"points": [v(0.35, -73.91) * mm, v(0.72, -72.1) * mm, v(-2.01, -66.79) * mm, v(-4.85, -63.81) * mm]});
            skFitSpline(sketch, "E992", {"points": [v(-4.85, -63.81) * mm, v(-8.09, -60.42) * mm, v(-8.47, -57.7) * mm, v(-7.4, -45.62) * mm]});
            skFitSpline(sketch, "E993", {"points": [v(-7.4, -45.62) * mm, v(-6.65, -37.32) * mm, v(-7.76, -35.66) * mm, v(-13.01, -37.18) * mm]});
            skFitSpline(sketch, "E994", {"points": [v(-13.01, -37.18) * mm, v(-16.2, -38.1) * mm, v(-17.2, -37.9) * mm, v(-18.4, -36.16) * mm]});
            skFitSpline(sketch, "E995", {"points": [v(-18.4, -36.16) * mm, v(-22.7, -29.97) * mm, v(-24.46, -29.67) * mm, v(-34.66, -33.42) * mm]});
            skFitSpline(sketch, "E996", {"points": [v(-34.66, -33.42) * mm, v(-38.5, -34.83) * mm, v(-42.73, -35.59) * mm, v(-44.56, -35.2) * mm]});
            skFitSpline(sketch, "E997", {"points": [v(-44.56, -35.2) * mm, v(-46.32, -34.81) * mm, v(-50.3, -35.15) * mm, v(-53.42, -35.93) * mm]});
            skFitSpline(sketch, "E998", {"points": [v(-53.42, -35.93) * mm, v(-58.8, -37.28) * mm, v(-59.38, -37.17) * mm, v(-64.6, -33.78) * mm]});
            skFitSpline(sketch, "E999", {"points": [v(-64.6, -33.78) * mm, v(-70.87, -29.7) * mm, v(-76.34, -22.96) * mm, v(-75.4, -20.49) * mm]});
            skFitSpline(sketch, "E1000", {"points": [v(-75.4, -20.49) * mm, v(-75.04, -19.57) * mm, v(-76.73, -16.4) * mm, v(-79.14, -13.46) * mm]});
            skFitSpline(sketch, "E1001", {"points": [v(-79.14, -13.46) * mm, v(-81.56, -10.5) * mm, v(-83.54, -7.55) * mm, v(-83.54, -6.88) * mm]});
            skFitSpline(sketch, "E1002", {"points": [v(-83.54, -6.88) * mm, v(-83.54, -6.21) * mm, v(-84.59, -4.72) * mm, v(-85.88, -3.55) * mm]});
            skFitSpline(sketch, "E1003", {"points": [v(-85.88, -3.55) * mm, v(-88.04, -1.6) * mm, v(-88.08, -1.1) * mm, v(-86.43, 2.86) * mm]});
            skFitSpline(sketch, "E1004", {"points": [v(-86.43, 2.86) * mm, v(-85.23, 5.73) * mm, v(-84.73, 10.63) * mm, v(-84.91, 17.73) * mm]});
            skFitSpline(sketch, "E1005", {"points": [v(-84.91, 17.73) * mm, v(-85.22, 29.61) * mm, v(-84.76, 32.33) * mm, v(-82.13, 34.3) * mm]});
            skFitSpline(sketch, "E1006", {"points": [v(-82.13, 34.3) * mm, v(-81.12, 35.04) * mm, v(-78.73, 38.35) * mm, v(-76.8, 41.65) * mm]});
            skFitSpline(sketch, "E1007", {"points": [v(-76.8, 41.65) * mm, v(-74.88, 44.94) * mm, v(-71.77, 48.52) * mm, v(-69.9, 49.6) * mm]});
            skFitSpline(sketch, "E1008", {"points": [v(-69.9, 49.6) * mm, v(-66.7, 51.41) * mm, v(-63.58, 56.45) * mm, v(-64.06, 58.98) * mm]});
            skFitSpline(sketch, "E1009", {"points": [v(-64.06, 58.98) * mm, v(-64.96, 63.73) * mm, v(-63.7, 66.9) * mm, v(-60.22, 68.7) * mm]});
            skFitSpline(sketch, "E1010", {"points": [v(-60.22, 68.7) * mm, v(-58.09, 69.8) * mm, v(-55.7, 72.47) * mm, v(-54.7, 74.85) * mm]});
            skFitSpline(sketch, "E1011", {"points": [v(-54.7, 74.85) * mm, v(-52.93, 79.07) * mm, v(-51.32, 80.08) * mm, v(-49.92, 77.82) * mm]});
            skFitSpline(sketch, "E1012", {"points": [v(-49.92, 77.82) * mm, v(-48.68, 75.81) * mm, v(-44.8, 76.4) * mm, v(-33.94, 80.23) * mm]});
            skFitSpline(sketch, "E1013", {"points": [v(-33.94, 80.23) * mm, v(-28.28, 82.23) * mm, v(-22.88, 83.56) * mm, v(-21.94, 83.2) * mm]});
            skFitSpline(sketch, "E1014", {"points": [v(-21.94, 83.2) * mm, v(-21, 82.84) * mm, v(-17.09, 83.12) * mm, v(-13.26, 83.83) * mm]});
            skFitSpline(sketch, "E1015", {"points": [v(-13.26, 83.83) * mm, v(-8.77, 84.66) * mm, v(-5.52, 84.7) * mm, v(-4.11, 83.95) * mm]});
            skFitSpline(sketch, "E1016", {"points": [v(-4.11, 83.95) * mm, v(-1.33, 82.46) * mm, v(0, 77.25) * mm, v(-1.61, 74.22) * mm]});
            skFitSpline(sketch, "E1017", {"points": [v(-1.61, 74.22) * mm, v(-3.07, 71.5) * mm, v(-0.43, 68.04) * mm, v(3.09, 68.04) * mm]});
            skFitSpline(sketch, "E1018", {"points": [v(3.09, 68.04) * mm, v(4.25, 68.04) * mm, v(8.64, 65.8) * mm, v(12.84, 63.08) * mm]});
            skFitSpline(sketch, "E1019", {"points": [v(12.84, 63.08) * mm, v(21.02, 57.77) * mm, v(24.4, 57.33) * mm, v(25, 61.51) * mm]});
            skFitSpline(sketch, "E1020", {"points": [v(25, 61.51) * mm, v(25.21, 62.95) * mm, v(26.44, 65.08) * mm, v(27.73, 66.25) * mm]});
            skFitSpline(sketch, "E1021", {"points": [v(27.73, 66.25) * mm, v(29.96, 68.27) * mm, v(30.36, 68.25) * mm, v(35.9, 65.96) * mm]});
            skFitSpline(sketch, "E1022", {"points": [v(35.9, 65.96) * mm, v(47.27, 61.28) * mm, v(51.93, 60.22) * mm, v(55.04, 61.64) * mm]});
            skFitSpline(sketch, "E1023", {"points": [v(55.04, 61.64) * mm, v(57.2, 62.63) * mm, v(58.71, 62.56) * mm, v(60.98, 61.39) * mm]});
            skFitSpline(sketch, "E1024", {"points": [v(60.98, 61.39) * mm, v(62.88, 60.4) * mm, v(64.73, 60.21) * mm, v(65.94, 60.89) * mm]});
            skFitSpline(sketch, "E1025", {"points": [v(65.94, 60.89) * mm, v(67.72, 61.88) * mm, v(70.32, 69.21) * mm, v(72.3, 78.76) * mm]});
            skFitSpline(sketch, "E1026", {"points": [v(72.3, 78.76) * mm, v(73.1, 82.7) * mm, v(73.07, 82.73) * mm, v(69.95, 81.3) * mm]});
            skFitSpline(sketch, "E1027", {"points": [v(69.95, 81.3) * mm, v(67.64, 80.26) * mm, v(65.64, 80.21) * mm, v(62.61, 81.14) * mm]});
            skFitSpline(sketch, "E1028", {"points": [v(62.61, 81.14) * mm, v(59.8, 82) * mm, v(58.04, 82.02) * mm, v(57.2, 81.18) * mm]});
            skFitSpline(sketch, "E1029", {"points": [v(57.2, 81.18) * mm, v(56.52, 80.5) * mm, v(54.97, 80.33) * mm, v(53.74, 80.8) * mm]});
            skFitSpline(sketch, "E1030", {"points": [v(53.74, 80.8) * mm, v(50.93, 81.87) * mm, v(50.34, 81.79) * mm, v(50.15, 80.27) * mm]});
            skFitSpline(sketch, "E1031", {"points": [v(50.15, 80.27) * mm, v(49.85, 77.87) * mm, v(49.67, 77.69) * mm, v(48.4, 78.47) * mm]});
            skFitSpline(sketch, "E1032", {"points": [v(48.4, 78.47) * mm, v(47.52, 79.02) * mm, v(47.52, 79.74) * mm, v(48.42, 80.82) * mm]});
            skFitSpline(sketch, "E1033", {"points": [v(48.42, 80.82) * mm, v(49.36, 81.96) * mm, v(49.21, 82.8) * mm, v(47.88, 83.9) * mm]});
            skFitSpline(sketch, "E1034", {"points": [v(47.88, 83.9) * mm, v(46.88, 84.75) * mm, v(46.33, 85.88) * mm, v(46.67, 86.43) * mm]});
            skFitSpline(sketch, "E1035", {"points": [v(46.67, 86.43) * mm, v(47.25, 87.37) * mm, v(45.28, 89.2) * mm, v(43.27, 89.57) * mm]});
            skFitSpline(sketch, "E1036", {"points": [v(43.27, 89.57) * mm, v(42.77, 89.66) * mm, v(42.05, 89.8) * mm, v(41.67, 89.9) * mm]});
            skFitSpline(sketch, "E1037", {"points": [v(41.67, 89.9) * mm, v(41.3, 89.98) * mm, v(41.35, 90.62) * mm, v(41.78, 91.33) * mm]});
            skFitSpline(sketch, "E1038", {"points": [v(41.78, 91.33) * mm, v(42.32, 92.2) * mm, v(43.1, 92.17) * mm, v(44.26, 91.21) * mm]});
            skFitSpline(sketch, "E1039", {"points": [v(44.26, 91.21) * mm, v(45.63, 90.07) * mm, v(45.9, 90.5) * mm, v(45.68, 93.5) * mm]});
            skFitSpline(sketch, "E1040", {"points": [v(45.68, 93.5) * mm, v(45.45, 96.66) * mm, v(44.93, 97.18) * mm, v(42.11, 97.1) * mm]});
            skFitSpline(sketch, "E1041", {"points": [v(42.11, 97.1) * mm, v(40.3, 97.05) * mm, v(38.51, 96.23) * mm, v(38.15, 95.28) * mm]});
            skFitSpline(sketch, "E1042", {"points": [v(38.15, 95.28) * mm, v(37.78, 94.33) * mm, v(36.93, 93.9) * mm, v(36.25, 94.32) * mm]});
            skFitSpline(sketch, "E1043", {"points": [v(36.25, 94.32) * mm, v(35.58, 94.74) * mm, v(35.02, 94.52) * mm, v(35.02, 93.83) * mm]});
            skFitSpline(sketch, "E1044", {"points": [v(35.02, 93.83) * mm, v(35.02, 93.14) * mm, v(36.12, 91.99) * mm, v(37.47, 91.27) * mm]});
            skFitSpline(sketch, "E1045", {"points": [v(37.47, 91.27) * mm, v(38.81, 90.55) * mm, v(39.91, 89.12) * mm, v(39.91, 88.1) * mm]});
            skFitSpline(sketch, "E1046", {"points": [v(39.91, 88.1) * mm, v(39.91, 87.07) * mm, v(40.42, 86.55) * mm, v(41.05, 86.94) * mm]});
            skFitSpline(sketch, "E1047", {"points": [v(41.05, 86.94) * mm, v(42.77, 88) * mm, v(44.05, 85.14) * mm, v(42.53, 83.62) * mm]});
            skFitSpline(sketch, "E1048", {"points": [v(42.53, 83.62) * mm, v(41.59, 82.68) * mm, v(41, 82.88) * mm, v(40.44, 84.33) * mm]});
            skFitSpline(sketch, "E1049", {"points": [v(40.44, 84.33) * mm, v(39.73, 86.17) * mm, v(39.32, 86.12) * mm, v(36.13, 83.85) * mm]});
            skFitSpline(sketch, "E1050", {"points": [v(36.13, 83.85) * mm, v(32.26, 81.1) * mm, v(29.6, 81.73) * mm, v(30.5, 85.19) * mm]});
            skFitSpline(sketch, "E1051", {"points": [v(30.5, 85.19) * mm, v(30.83, 86.45) * mm, v(29.64, 89.12) * mm, v(27.71, 91.47) * mm]});
            skFitSpline(sketch, "E1052", {"points": [v(27.71, 91.47) * mm, v(25.86, 93.7) * mm, v(23.99, 97.2) * mm, v(23.54, 99.21) * mm]});
            skFitSpline(sketch, "E1053", {"points": [v(23.54, 99.21) * mm, v(23.04, 101.49) * mm, v(21.1, 104) * mm, v(18.43, 105.82) * mm]});
            skFitSpline(sketch, "E1054", {"points": [v(18.43, 105.82) * mm, v(16.07, 107.45) * mm, v(12.78, 110.37) * mm, v(11.13, 112.34) * mm]});
            skFitSpline(sketch, "E1055", {"points": [v(11.13, 112.34) * mm, v(9.48, 114.3) * mm, v(8.12, 115.44) * mm, v(8.1, 114.89) * mm]});
            skFitSpline(sketch, "E1056", {"points": [v(8.1, 114.89) * mm, v(8.07, 114.33) * mm, v(7.26, 114.93) * mm, v(6.3, 116.2) * mm]});
            skFitSpline(sketch, "E1057", {"points": [v(6.3, 116.2) * mm, v(2.93, 120.65) * mm, v(2.87, 115.14) * mm, v(6.23, 110.2) * mm]});
            skFitSpline(sketch, "E1058", {"points": [v(6.23, 110.2) * mm, v(7.95, 107.67) * mm, v(9.35, 105.22) * mm, v(9.35, 104.76) * mm]});
            skFitSpline(sketch, "E1059", {"points": [v(9.35, 104.76) * mm, v(9.35, 104.3) * mm, v(11.82, 102.7) * mm, v(14.83, 101.19) * mm]});
            skFitSpline(sketch, "E1060", {"points": [v(14.83, 101.19) * mm, v(20.8, 98.2) * mm, v(22.14, 96.83) * mm, v(20.93, 94.87) * mm]});
            skFitSpline(sketch, "E1061", {"points": [v(20.93, 94.87) * mm, v(20.4, 94) * mm, v(19.56, 94.07) * mm, v(18.34, 95.09) * mm]});
            skFitSpline(sketch, "E1062", {"points": [v(18.34, 95.09) * mm, v(16.8, 96.36) * mm, v(16.66, 96.1) * mm, v(17.36, 93.3) * mm]});
            skFitSpline(sketch, "E1063", {"points": [v(17.36, 93.3) * mm, v(18.21, 89.89) * mm, v(16.39, 84.69) * mm, v(13.94, 85.62) * mm]});
            skFitSpline(sketch, "E1064", {"points": [v(13.94, 85.62) * mm, v(13.1, 87.81) * mm, v(13.35, 86.43) * mm, v(13.38, 88.02) * mm]});
            skFitSpline(sketch, "E1065", {"points": [v(13.38, 88.02) * mm, v(13.46, 88.3) * mm, v(13.55, 88.58) * mm, v(13.63, 88.86) * mm]});
            skFitSpline(sketch, "E1066", {"points": [v(114.4, 84.6) * mm, v(111.54, 87.66) * mm, v(111.52, 87.85) * mm, v(113.4, 93.1) * mm]});
            skFitSpline(sketch, "E1067", {"points": [v(113.4, 93.1) * mm, v(114.92, 97.3) * mm, v(115, 98.6) * mm, v(113.8, 99.06) * mm]});
            skFitSpline(sketch, "E1068", {"points": [v(113.8, 99.06) * mm, v(112.95, 99.39) * mm, v(111.07, 102.83) * mm, v(109.62, 106.72) * mm]});
            skFitSpline(sketch, "E1069", {"points": [v(109.62, 106.72) * mm, v(107.6, 112.13) * mm, v(107.27, 114.42) * mm, v(108.23, 116.53) * mm]});
            skFitSpline(sketch, "E1070", {"points": [v(108.23, 116.53) * mm, v(109.76, 119.88) * mm, v(117.62, 124.04) * mm, v(121.8, 123.7) * mm]});
            skFitSpline(sketch, "E1071", {"points": [v(121.8, 123.7) * mm, v(124.3, 123.5) * mm, v(124.86, 122.81) * mm, v(124.86, 119.89) * mm]});
            skFitSpline(sketch, "E1072", {"points": [v(124.86, 119.89) * mm, v(124.86, 117.14) * mm, v(124.3, 116.32) * mm, v(122.41, 116.32) * mm]});
            skFitSpline(sketch, "E1073", {"points": [v(122.41, 116.32) * mm, v(121.07, 116.32) * mm, v(120.06, 115.77) * mm, v(120.17, 115.1) * mm]});
            skFitSpline(sketch, "E1074", {"points": [v(120.17, 115.1) * mm, v(120.28, 114.43) * mm, v(119.88, 113.28) * mm, v(119.27, 112.56) * mm]});
            skFitSpline(sketch, "E1075", {"points": [v(119.27, 112.56) * mm, v(118.58, 111.73) * mm, v(119.18, 110.16) * mm, v(120.9, 108.32) * mm]});
            skFitSpline(sketch, "E1076", {"points": [v(120.9, 108.32) * mm, v(122.39, 106.72) * mm, v(123.43, 104.29) * mm, v(123.22, 102.92) * mm]});
            skFitSpline(sketch, "E1077", {"points": [v(123.22, 102.92) * mm, v(122.84, 100.53) * mm, v(122.9, 100.52) * mm, v(124.53, 102.7) * mm]});
            skFitSpline(sketch, "E1078", {"points": [v(124.53, 102.7) * mm, v(126.17, 104.88) * mm, v(126.32, 104.85) * mm, v(128.23, 101.93) * mm]});
            skFitSpline(sketch, "E1079", {"points": [v(128.23, 101.93) * mm, v(130.45, 98.54) * mm, v(129.94, 97.38) * mm, v(126.25, 97.38) * mm]});
            skFitSpline(sketch, "E1080", {"points": [v(126.25, 97.38) * mm, v(123.82, 97.38) * mm, v(123.81, 97.35) * mm, v(126.15, 95.58) * mm]});
            skFitSpline(sketch, "E1081", {"points": [v(126.15, 95.58) * mm, v(127.46, 94.6) * mm, v(128.18, 93.77) * mm, v(127.77, 93.75) * mm]});
            skFitSpline(sketch, "E1082", {"points": [v(127.77, 93.75) * mm, v(127.36, 93.73) * mm, v(127.43, 91.47) * mm, v(127.93, 88.74) * mm]});
            skFitSpline(sketch, "E1083", {"points": [v(127.93, 88.74) * mm, v(128.76, 84.2) * mm, v(128.58, 83.66) * mm, v(125.85, 82.63) * mm]});
            skFitSpline(sketch, "E1084", {"points": [v(125.85, 82.63) * mm, v(120.89, 80.74) * mm, v(117.5, 81.33) * mm, v(114.4, 84.6) * mm]});
            skFitSpline(sketch, "E1085", {"points": [v(141.28, 112.2) * mm, v(140.1, 114.39) * mm, v(140.36, 115.27) * mm, v(142.94, 117.85) * mm]});
            skFitSpline(sketch, "E1086", {"points": [v(142.94, 117.85) * mm, v(144.62, 119.53) * mm, v(146.6, 120.53) * mm, v(147.34, 120.07) * mm]});
            skFitSpline(sketch, "E1087", {"points": [v(147.34, 120.07) * mm, v(149.44, 118.77) * mm, v(148.93, 113.86) * mm, v(146.46, 111.62) * mm]});
            skFitSpline(sketch, "E1088", {"points": [v(146.46, 111.62) * mm, v(143.56, 109) * mm, v(142.95, 109.07) * mm, v(141.28, 112.2) * mm]});
            skFitSpline(sketch, "E1089", {"points": [v(56.7, 182.73) * mm, v(55.38, 185.36) * mm, v(55.24, 186.77) * mm, v(56.19, 187.72) * mm]});
            skFitSpline(sketch, "E1090", {"points": [v(56.19, 187.72) * mm, v(58.4, 189.94) * mm, v(61.75, 189.2) * mm, v(63.82, 186.05) * mm]});
            skFitSpline(sketch, "E1091", {"points": [v(63.82, 186.05) * mm, v(65.9, 182.87) * mm, v(65.17, 179.92) * mm, v(62.55, 180.92) * mm]});
            skFitSpline(sketch, "E1092", {"points": [v(62.55, 180.92) * mm, v(61.7, 181.25) * mm, v(60.43, 180.97) * mm, v(59.76, 180.3) * mm]});
            skFitSpline(sketch, "E1093", {"points": [v(59.76, 180.3) * mm, v(58.93, 179.47) * mm, v(57.92, 180.27) * mm, v(56.7, 182.73) * mm]});
            skFitSpline(sketch, "E1094", {"points": [v(11.8, 85.16) * mm, v(11.8, 87.06) * mm, v(10.99, 87.6) * mm, v(8.13, 87.6) * mm]});
            skFitSpline(sketch, "E1095", {"points": [v(8.13, 87.6) * mm, v(3.8, 87.6) * mm, v(3.37, 86.06) * mm, v(7.22, 84.2) * mm]});
            skFitSpline(sketch, "E1096", {"points": [v(7.22, 84.2) * mm, v(11.18, 82.3) * mm, v(11.8, 82.42) * mm, v(11.8, 85.16) * mm]});
            skFitSpline(sketch, "E1097", {"points": [v(52.58, 99.21) * mm, v(52.96, 100.22) * mm, v(54.53, 101.06) * mm, v(56.07, 101.09) * mm]});
            skFitSpline(sketch, "E1098", {"points": [v(56.07, 101.09) * mm, v(57.6, 101.11) * mm, v(60.23, 101.92) * mm, v(61.91, 102.88) * mm]});
            skFitSpline(sketch, "E1099", {"points": [v(61.91, 102.88) * mm, v(66.04, 105.24) * mm, v(69.12, 105.14) * mm, v(74.37, 102.46) * mm]});
            skFitSpline(sketch, "E1100", {"points": [v(74.37, 102.46) * mm, v(79.1, 100.05) * mm, v(86.72, 99.7) * mm, v(88.82, 101.8) * mm]});
            skFitSpline(sketch, "E1101", {"points": [v(88.82, 101.8) * mm, v(90.78, 103.76) * mm, v(89.24, 106.1) * mm, v(82.58, 111.25) * mm]});
            skFitSpline(sketch, "E1102", {"points": [v(82.58, 111.25) * mm, v(77.47, 115.2) * mm, v(76.73, 116.26) * mm, v(78, 117.8) * mm]});
            skFitSpline(sketch, "E1103", {"points": [v(78, 117.8) * mm, v(80.29, 120.54) * mm, v(80.4, 123.37) * mm, v(78.2, 122.52) * mm]});
            skFitSpline(sketch, "E1104", {"points": [v(78.2, 122.52) * mm, v(77.19, 122.13) * mm, v(75.03, 121.48) * mm, v(73.41, 121.07) * mm]});
            skFitSpline(sketch, "E1105", {"points": [v(73.41, 121.07) * mm, v(70.01, 120.22) * mm, v(69.6, 118.75) * mm, v(72.44, 117.66) * mm]});
            skFitSpline(sketch, "E1106", {"points": [v(72.44, 117.66) * mm, v(74.03, 117.05) * mm, v(74.12, 116.56) * mm, v(72.9, 115.09) * mm]});
            skFitSpline(sketch, "E1107", {"points": [v(72.9, 115.09) * mm, v(70.98, 112.77) * mm, v(69.87, 112.8) * mm, v(66.13, 115.26) * mm]});
            skFitSpline(sketch, "E1108", {"points": [v(66.13, 115.26) * mm, v(63.9, 116.72) * mm, v(63.43, 117.65) * mm, v(64.37, 118.78) * mm]});
            skFitSpline(sketch, "E1109", {"points": [v(64.37, 118.78) * mm, v(66.5, 121.36) * mm, v(62.1, 122.07) * mm, v(58.78, 119.68) * mm]});
            skFitSpline(sketch, "E1110", {"points": [v(58.78, 119.68) * mm, v(54.65, 116.7) * mm, v(49.48, 105.83) * mm, v(51.2, 103.75) * mm]});
            skFitSpline(sketch, "E1111", {"points": [v(51.2, 103.75) * mm, v(52.15, 102.61) * mm, v(52.12, 101.76) * mm, v(51.1, 100.75) * mm]});
            skFitSpline(sketch, "E1112", {"points": [v(51.1, 100.75) * mm, v(50.33, 99.97) * mm, v(49.69, 98.9) * mm, v(49.69, 98.36) * mm]});
            skFitSpline(sketch, "E1113", {"points": [v(49.69, 98.36) * mm, v(49.69, 96.66) * mm, v(51.84, 97.3) * mm, v(52.58, 99.21) * mm]});
            skFitSpline(sketch, "E1114", {"points": [v(455.97, 189.19) * mm, v(456.94, 191.13) * mm, v(457.2, 192.71) * mm, v(456.57, 192.71) * mm]});
            skFitSpline(sketch, "E1115", {"points": [v(456.57, 192.71) * mm, v(455.93, 192.71) * mm, v(454.9, 191.34) * mm, v(454.25, 189.66) * mm]});
            skFitSpline(sketch, "E1116", {"points": [v(454.25, 189.66) * mm, v(453.61, 187.98) * mm, v(452.28, 186.6) * mm, v(451.3, 186.6) * mm]});
            skFitSpline(sketch, "E1117", {"points": [v(451.3, 186.6) * mm, v(450.31, 186.6) * mm, v(449.22, 186.13) * mm, v(448.86, 185.56) * mm]});
            skFitSpline(sketch, "E1118", {"points": [v(448.86, 185.56) * mm, v(448.5, 184.98) * mm, v(449.56, 184.77) * mm, v(451.21, 185.08) * mm]});
            skFitSpline(sketch, "E1119", {"points": [v(451.21, 185.08) * mm, v(452.95, 185.42) * mm, v(454.95, 187.14) * mm, v(455.97, 189.19) * mm]});
            skFitSpline(sketch, "E1120", {"points": [v(181.07, 212.25) * mm, v(181.49, 212.93) * mm, v(181.04, 213.16) * mm, v(180.04, 212.78) * mm]});
            skFitSpline(sketch, "E1121", {"points": [v(180.04, 212.78) * mm, v(179.07, 212.4) * mm, v(177.9, 212.7) * mm, v(177.47, 213.4) * mm]});
            skFitSpline(sketch, "E1122", {"points": [v(177.47, 213.4) * mm, v(177.02, 214.13) * mm, v(175.45, 214.7) * mm, v(173.98, 214.7) * mm]});
            skFitSpline(sketch, "E1123", {"points": [v(173.98, 214.7) * mm, v(171.4, 214.68) * mm, v(171.42, 214.61) * mm, v(174.36, 212.98) * mm]});
            skFitSpline(sketch, "E1124", {"points": [v(174.36, 212.98) * mm, v(178.12, 210.9) * mm, v(180.1, 210.68) * mm, v(181.07, 212.25) * mm]});
            skFitSpline(sketch, "E1125", {"points": [v(291.2, 248.04) * mm, v(291.7, 248.53) * mm, v(293.25, 248.95) * mm, v(294.65, 248.97) * mm]});
            skFitSpline(sketch, "E1126", {"points": [v(294.65, 248.97) * mm, v(296.98, 249) * mm, v(297.01, 249.12) * mm, v(295.03, 250.27) * mm]});
            skFitSpline(sketch, "E1127", {"points": [v(295.03, 250.27) * mm, v(293.83, 250.97) * mm, v(293.24, 252.18) * mm, v(293.71, 252.98) * mm]});
            skFitSpline(sketch, "E1128", {"points": [v(293.71, 252.98) * mm, v(294.18, 253.78) * mm, v(293.46, 253.47) * mm, v(292.11, 252.3) * mm]});
            skFitSpline(sketch, "E1129", {"points": [v(292.11, 252.3) * mm, v(290.77, 251.12) * mm, v(289.13, 250.16) * mm, v(288.47, 250.16) * mm]});
            skFitSpline(sketch, "E1130", {"points": [v(288.47, 250.16) * mm, v(287.81, 250.16) * mm, v(286.22, 249.4) * mm, v(284.94, 248.46) * mm]});
            skFitSpline(sketch, "E1131", {"points": [v(284.94, 248.46) * mm, v(282.78, 246.87) * mm, v(282.88, 246.76) * mm, v(286.46, 246.94) * mm]});
            skFitSpline(sketch, "E1132", {"points": [v(286.46, 246.94) * mm, v(288.57, 247.05) * mm, v(290.7, 247.54) * mm, v(291.2, 248.04) * mm]});
            skFitSpline(sketch, "E1133", {"points": [v(96.93, -141.28) * mm, v(93.79, -135.13) * mm, v(93.3, -130.13) * mm, v(95.5, -126.76) * mm]});
            skFitSpline(sketch, "E1134", {"points": [v(95.5, -126.76) * mm, v(96.92, -124.6) * mm, v(97.32, -122.28) * mm, v(96.82, -119.17) * mm]});
            skFitSpline(sketch, "E1135", {"points": [v(96.82, -119.17) * mm, v(95.9, -113.37) * mm, v(98.03, -109.4) * mm, v(103.58, -106.52) * mm]});
            skFitSpline(sketch, "E1136", {"points": [v(103.58, -106.52) * mm, v(107.68, -104.4) * mm, v(109.54, -102) * mm, v(111.32, -96.52) * mm]});
            skFitSpline(sketch, "E1137", {"points": [v(111.32, -96.52) * mm, v(111.89, -94.75) * mm, v(112.43, -94.55) * mm, v(113.71, -95.62) * mm]});
            skFitSpline(sketch, "E1138", {"points": [v(113.71, -95.62) * mm, v(115.75, -97.3) * mm, v(117.1, -106.35) * mm, v(115.71, -109.04) * mm]});
            skFitSpline(sketch, "E1139", {"points": [v(115.71, -109.04) * mm, v(115.15, -110.13) * mm, v(113.77, -115.41) * mm, v(112.64, -120.8) * mm]});
            skFitSpline(sketch, "E1140", {"points": [v(112.64, -120.8) * mm, v(108.38, -140.98) * mm, v(107.65, -142.56) * mm, v(101.98, -143.88) * mm]});
            skFitSpline(sketch, "E1141", {"points": [v(101.98, -143.88) * mm, v(99.2, -144.53) * mm, v(98.37, -144.1) * mm, v(96.93, -141.28) * mm]});
            skFitSpline(sketch, "E1142", {"points": [v(374.26, -100.73) * mm, v(373.87, -100.1) * mm, v(374.06, -99.25) * mm, v(374.7, -98.86) * mm]});
            skFitSpline(sketch, "E1143", {"points": [v(374.7, -98.86) * mm, v(375.34, -98.46) * mm, v(376.18, -98.66) * mm, v(376.58, -99.3) * mm]});
            skFitSpline(sketch, "E1144", {"points": [v(376.58, -99.3) * mm, v(376.97, -99.94) * mm, v(376.77, -100.78) * mm, v(376.13, -101.17) * mm]});
            skFitSpline(sketch, "E1145", {"points": [v(376.13, -101.17) * mm, v(375.5, -101.56) * mm, v(374.65, -101.37) * mm, v(374.26, -100.73) * mm]});
            skFitSpline(sketch, "E1146", {"points": [v(334.95, -88.18) * mm, v(333.67, -86.12) * mm, v(343.28, -78.56) * mm, v(345.18, -80.12) * mm]});
            skFitSpline(sketch, "E1147", {"points": [v(345.18, -80.12) * mm, v(347.12, -81.72) * mm, v(345.64, -83.68) * mm, v(339.9, -87.06) * mm]});
            skFitSpline(sketch, "E1148", {"points": [v(339.9, -87.06) * mm, v(337.13, -88.7) * mm, v(335.5, -89.07) * mm, v(334.95, -88.18) * mm]});
            skFitSpline(sketch, "E1149", {"points": [v(409.29, -88.24) * mm, v(406.83, -87.54) * mm, v(404.84, -85.96) * mm, v(404.17, -84.2) * mm]});
            skFitSpline(sketch, "E1150", {"points": [v(404.17, -84.2) * mm, v(403.56, -82.6) * mm, v(402.45, -80.93) * mm, v(401.7, -80.46) * mm]});
            skFitSpline(sketch, "E1151", {"points": [v(401.7, -80.46) * mm, v(399.7, -79.23) * mm, v(394.32, -80.86) * mm, v(394.67, -82.59) * mm]});
            skFitSpline(sketch, "E1152", {"points": [v(394.67, -82.59) * mm, v(395.18, -85.1) * mm, v(389.96, -85) * mm, v(385.12, -82.4) * mm]});
            skFitSpline(sketch, "E1153", {"points": [v(385.12, -82.4) * mm, v(382.6, -81.05) * mm, v(380.06, -80.23) * mm, v(379.5, -80.58) * mm]});
            skFitSpline(sketch, "E1154", {"points": [v(379.5, -80.58) * mm, v(377.17, -82.02) * mm, v(375.92, -79.55) * mm, v(377.88, -77.38) * mm]});
            skFitSpline(sketch, "E1155", {"points": [v(377.88, -77.38) * mm, v(380.73, -74.23) * mm, v(378.7, -71.08) * mm, v(371.34, -67.24) * mm]});
            skFitSpline(sketch, "E1156", {"points": [v(371.34, -67.24) * mm, v(367.19, -65.06) * mm, v(364.97, -64.5) * mm, v(364.09, -65.39) * mm]});
            skFitSpline(sketch, "E1157", {"points": [v(364.09, -65.39) * mm, v(363.2, -66.28) * mm, v(362.4, -65.9) * mm, v(361.47, -64.15) * mm]});
            skFitSpline(sketch, "E1158", {"points": [v(361.47, -64.15) * mm, v(360.38, -62.13) * mm, v(360.54, -61.4) * mm, v(362.27, -60.4) * mm]});
            skFitSpline(sketch, "E1159", {"points": [v(362.27, -60.4) * mm, v(364.1, -59.33) * mm, v(364.13, -59.14) * mm, v(362.47, -59.1) * mm]});
            skFitSpline(sketch, "E1160", {"points": [v(362.47, -59.1) * mm, v(360.2, -59.06) * mm, v(356.1, -54.95) * mm, v(357.22, -53.83) * mm]});
            skFitSpline(sketch, "E1161", {"points": [v(357.22, -53.83) * mm, v(358.23, -52.83) * mm, v(365.2, -54.19) * mm, v(367.22, -55.77) * mm]});
            skFitSpline(sketch, "E1162", {"points": [v(367.22, -55.77) * mm, v(368.1, -56.46) * mm, v(368.54, -57.71) * mm, v(368.21, -58.56) * mm]});
            skFitSpline(sketch, "E1163", {"points": [v(368.21, -58.56) * mm, v(367.89, -59.42) * mm, v(368.43, -60.78) * mm, v(369.41, -61.6) * mm]});
            skFitSpline(sketch, "E1164", {"points": [v(369.41, -61.6) * mm, v(370.87, -62.8) * mm, v(371.75, -62.59) * mm, v(374.01, -60.46) * mm]});
            skFitSpline(sketch, "E1165", {"points": [v(374.01, -60.46) * mm, v(374.95, -59.58) * mm, v(375.88, -58.7) * mm, v(376.82, -57.83) * mm]});
            skFitSpline(sketch, "E1166", {"points": [v(376.82, -57.83) * mm, v(379.2, -58.65) * mm, v(381.58, -59.47) * mm, v(383.96, -60.29) * mm]});
            skFitSpline(sketch, "E1167", {"points": [v(383.96, -60.29) * mm, v(396.94, -64.75) * mm, v(407.75, -72.45) * mm, v(408.31, -77.62) * mm]});
            skFitSpline(sketch, "E1168", {"points": [v(408.31, -77.62) * mm, v(408.76, -81.64) * mm, v(415.1, -87.5) * mm, v(417.17, -85.8) * mm]});
            skFitSpline(sketch, "E1169", {"points": [v(417.17, -85.8) * mm, v(418.09, -85.03) * mm, v(418.87, -85.07) * mm, v(419.38, -85.9) * mm]});
            skFitSpline(sketch, "E1170", {"points": [v(419.38, -85.9) * mm, v(420.15, -87.15) * mm, v(419.98, -87.33) * mm, v(417.69, -87.64) * mm]});
            skFitSpline(sketch, "E1171", {"points": [v(417.69, -87.64) * mm, v(417.07, -87.72) * mm, v(416.15, -88.2) * mm, v(415.65, -88.7) * mm]});
            skFitSpline(sketch, "E1172", {"points": [v(415.65, -88.7) * mm, v(414.59, -89.77) * mm, v(414.58, -89.77) * mm, v(409.29, -88.24) * mm]});
            skFitSpline(sketch, "E1173", {"points": [v(314.26, -83.43) * mm, v(313.92, -82.9) * mm, v(314.08, -82.25) * mm, v(314.6, -82) * mm]});
            skFitSpline(sketch, "E1174", {"points": [v(314.6, -82) * mm, v(316.27, -81.14) * mm, v(319.18, -81.65) * mm, v(319.8, -82.9) * mm]});
            skFitSpline(sketch, "E1175", {"points": [v(319.8, -82.9) * mm, v(320.53, -84.34) * mm, v(315.14, -84.86) * mm, v(314.26, -83.43) * mm]});
            skFitSpline(sketch, "E1176", {"points": [v(324.13, -83.6) * mm, v(323.75, -82.97) * mm, v(324.02, -82.1) * mm, v(324.73, -81.66) * mm]});
            skFitSpline(sketch, "E1177", {"points": [v(324.73, -81.66) * mm, v(326.54, -80.54) * mm, v(329.9, -82) * mm, v(328.98, -83.5) * mm]});
            skFitSpline(sketch, "E1178", {"points": [v(328.98, -83.5) * mm, v(328.02, -85.05) * mm, v(325.07, -85.1) * mm, v(324.13, -83.6) * mm]});
            skFitSpline(sketch, "E1179", {"points": [v(303.74, -82.93) * mm, v(303.39, -82.58) * mm, v(301.5, -82.02) * mm, v(299.54, -81.7) * mm]});
            skFitSpline(sketch, "E1180", {"points": [v(299.54, -81.7) * mm, v(297.58, -81.37) * mm, v(294.05, -80.77) * mm, v(291.7, -80.37) * mm]});
            skFitSpline(sketch, "E1181", {"points": [v(291.7, -80.37) * mm, v(289.34, -79.97) * mm, v(285.62, -78.83) * mm, v(283.43, -77.85) * mm]});
            skFitSpline(sketch, "E1182", {"points": [v(283.43, -77.85) * mm, v(280.08, -76.34) * mm, v(279.65, -75.7) * mm, v(280.68, -73.76) * mm]});
            skFitSpline(sketch, "E1183", {"points": [v(280.68, -73.76) * mm, v(281.75, -71.77) * mm, v(282.45, -71.64) * mm, v(285.89, -72.78) * mm]});
            skFitSpline(sketch, "E1184", {"points": [v(285.89, -72.78) * mm, v(288.07, -73.5) * mm, v(292.1, -74.2) * mm, v(294.82, -74.32) * mm]});
            skFitSpline(sketch, "E1185", {"points": [v(294.82, -74.32) * mm, v(302.18, -74.64) * mm, v(310.55, -81.5) * mm, v(305.6, -83.16) * mm]});
            skFitSpline(sketch, "E1186", {"points": [v(305.6, -83.16) * mm, v(304.93, -83.38) * mm, v(304.09, -83.28) * mm, v(303.74, -82.93) * mm]});
            skFitSpline(sketch, "E1187", {"points": [v(304.58, -76.26) * mm, v(303.68, -74.8) * mm, v(305.97, -73.35) * mm, v(307.6, -74.36) * mm]});
            skFitSpline(sketch, "E1188", {"points": [v(307.6, -74.36) * mm, v(308.97, -75.2) * mm, v(308.07, -77.4) * mm, v(306.36, -77.4) * mm]});
            skFitSpline(sketch, "E1189", {"points": [v(306.36, -77.4) * mm, v(305.77, -77.4) * mm, v(304.97, -76.89) * mm, v(304.58, -76.26) * mm]});
            skFitSpline(sketch, "E1190", {"points": [v(322.94, -73.08) * mm, v(321.83, -71.39) * mm, v(321.27, -69.44) * mm, v(321.7, -68.76) * mm]});
            skFitSpline(sketch, "E1191", {"points": [v(321.7, -68.76) * mm, v(322.11, -68.08) * mm, v(321.86, -66.8) * mm, v(321.14, -65.92) * mm]});
            skFitSpline(sketch, "E1192", {"points": [v(321.14, -65.92) * mm, v(319.03, -63.39) * mm, v(322.01, -50.71) * mm, v(325.19, -48.7) * mm]});
            skFitSpline(sketch, "E1193", {"points": [v(325.19, -48.7) * mm, v(327.77, -47.06) * mm, v(338.45, -46.75) * mm, v(339.98, -48.27) * mm]});
            skFitSpline(sketch, "E1194", {"points": [v(339.98, -48.27) * mm, v(341.37, -49.68) * mm, v(335.58, -52) * mm, v(332.27, -51.37) * mm]});
            skFitSpline(sketch, "E1195", {"points": [v(332.27, -51.37) * mm, v(328.51, -50.65) * mm, v(325.92, -51.47) * mm, v(325.92, -53.4) * mm]});
            skFitSpline(sketch, "E1196", {"points": [v(325.92, -53.4) * mm, v(325.91, -54.2) * mm, v(327.88, -54.8) * mm, v(330.5, -54.8) * mm]});
            skFitSpline(sketch, "E1197", {"points": [v(330.5, -54.8) * mm, v(333.76, -54.8) * mm, v(335.08, -55.32) * mm, v(335.08, -56.62) * mm]});
            skFitSpline(sketch, "E1198", {"points": [v(335.08, -56.62) * mm, v(335.08, -57.9) * mm, v(334.05, -58.35) * mm, v(331.72, -58.1) * mm]});
            skFitSpline(sketch, "E1199", {"points": [v(331.72, -58.1) * mm, v(327.59, -57.67) * mm, v(327.37, -59.59) * mm, v(331.27, -62.14) * mm]});
            skFitSpline(sketch, "E1200", {"points": [v(331.27, -62.14) * mm, v(334.23, -64.08) * mm, v(334.96, -68.87) * mm, v(332.81, -72.27) * mm]});
            skFitSpline(sketch, "E1201", {"points": [v(332.81, -72.27) * mm, v(331.41, -74.48) * mm, v(328.37, -71.84) * mm, v(328.34, -68.4) * mm]});
            skFitSpline(sketch, "E1202", {"points": [v(328.34, -68.4) * mm, v(328.33, -66.96) * mm, v(327.74, -64.97) * mm, v(327.02, -63.96) * mm]});
            skFitSpline(sketch, "E1203", {"points": [v(327.02, -63.96) * mm, v(326.06, -62.6) * mm, v(325.89, -63.8) * mm, v(326.37, -68.5) * mm]});
            skFitSpline(sketch, "E1204", {"points": [v(326.37, -68.5) * mm, v(327.11, -75.83) * mm, v(325.85, -77.52) * mm, v(322.94, -73.08) * mm]});
            skFitSpline(sketch, "E1205", {"points": [v(412.09, -72.51) * mm, v(411.14, -71) * mm, v(412.38, -68.85) * mm, v(414.2, -68.85) * mm]});
            skFitSpline(sketch, "E1206", {"points": [v(414.2, -68.85) * mm, v(414.95, -68.85) * mm, v(416.5, -67.99) * mm, v(417.67, -66.93) * mm]});
            skFitSpline(sketch, "E1207", {"points": [v(417.67, -66.93) * mm, v(421.16, -63.78) * mm, v(421.76, -67.23) * mm, v(418.32, -70.67) * mm]});
            skFitSpline(sketch, "E1208", {"points": [v(418.32, -70.67) * mm, v(415.03, -73.95) * mm, v(413.3, -74.47) * mm, v(412.09, -72.51) * mm]});
            skFitSpline(sketch, "E1209", {"points": [v(271.83, -66.1) * mm, v(268.64, -62.57) * mm, v(266.03, -58.81) * mm, v(266.03, -57.75) * mm]});
            skFitSpline(sketch, "E1210", {"points": [v(266.03, -57.75) * mm, v(266.03, -56.7) * mm, v(264.65, -54.54) * mm, v(262.97, -52.96) * mm]});
            skFitSpline(sketch, "E1211", {"points": [v(262.97, -52.96) * mm, v(261.3, -51.38) * mm, v(259.92, -49.15) * mm, v(259.92, -48.02) * mm]});
            skFitSpline(sketch, "E1212", {"points": [v(259.92, -48.02) * mm, v(259.92, -46.88) * mm, v(257.7, -43.16) * mm, v(255, -39.76) * mm]});
            skFitSpline(sketch, "E1213", {"points": [v(255, -39.76) * mm, v(252.29, -36.36) * mm, v(250.5, -33.35) * mm, v(251.02, -33.06) * mm]});
            skFitSpline(sketch, "E1214", {"points": [v(251.02, -33.06) * mm, v(253.08, -31.93) * mm, v(259.94, -34.83) * mm, v(261.29, -37.4) * mm]});
            skFitSpline(sketch, "E1215", {"points": [v(261.29, -37.4) * mm, v(262.07, -38.9) * mm, v(265.4, -42.71) * mm, v(268.66, -45.88) * mm]});
            skFitSpline(sketch, "E1216", {"points": [v(268.66, -45.88) * mm, v(271.94, -49.04) * mm, v(274.47, -52.07) * mm, v(274.3, -52.6) * mm]});
            skFitSpline(sketch, "E1217", {"points": [v(274.3, -52.6) * mm, v(273.82, -54.03) * mm, v(279.39, -59.26) * mm, v(280.6, -58.52) * mm]});
            skFitSpline(sketch, "E1218", {"points": [v(280.6, -58.52) * mm, v(281.17, -58.16) * mm, v(282.34, -58.71) * mm, v(283.2, -59.75) * mm]});
            skFitSpline(sketch, "E1219", {"points": [v(283.2, -59.75) * mm, v(284.37, -61.16) * mm, v(284.4, -61.96) * mm, v(283.33, -63.03) * mm]});
            skFitSpline(sketch, "E1220", {"points": [v(283.33, -63.03) * mm, v(282.55, -63.8) * mm, v(281.92, -65.6) * mm, v(281.92, -67.01) * mm]});
            skFitSpline(sketch, "E1221", {"points": [v(281.92, -67.01) * mm, v(281.92, -69.4) * mm, v(279.87, -72.51) * mm, v(278.3, -72.51) * mm]});
            skFitSpline(sketch, "E1222", {"points": [v(278.3, -72.51) * mm, v(277.92, -72.51) * mm, v(275.01, -69.63) * mm, v(271.83, -66.1) * mm]});
            skFitSpline(sketch, "E1223", {"points": [v(308.29, -66.55) * mm, v(307.88, -65.9) * mm, v(305.68, -65.54) * mm, v(303.38, -65.75) * mm]});
            skFitSpline(sketch, "E1224", {"points": [v(303.38, -65.75) * mm, v(300.32, -66.04) * mm, v(298.6, -65.44) * mm, v(296.9, -63.52) * mm]});
            skFitSpline(sketch, "E1225", {"points": [v(296.9, -63.52) * mm, v(288.92, -54.47) * mm, v(287.63, -45.62) * mm, v(294.29, -45.62) * mm]});
            skFitSpline(sketch, "E1226", {"points": [v(294.29, -45.62) * mm, v(295.55, -45.62) * mm, v(296.58, -44.79) * mm, v(296.58, -43.76) * mm]});
            skFitSpline(sketch, "E1227", {"points": [v(296.58, -43.76) * mm, v(296.58, -42.74) * mm, v(298.07, -41.33) * mm, v(299.88, -40.64) * mm]});
            skFitSpline(sketch, "E1228", {"points": [v(299.88, -40.64) * mm, v(301.7, -39.95) * mm, v(305.8, -36.66) * mm, v(309, -33.32) * mm]});
            skFitSpline(sketch, "E1229", {"points": [v(309, -33.32) * mm, v(310.94, -31.3) * mm, v(312.88, -29.27) * mm, v(314.82, -27.24) * mm]});
            skFitSpline(sketch, "E1230", {"points": [v(314.82, -27.24) * mm, v(316.1, -28.38) * mm, v(317.37, -29.51) * mm, v(318.64, -30.65) * mm]});
            skFitSpline(sketch, "E1231", {"points": [v(318.64, -30.65) * mm, v(319.9, -31.78) * mm, v(321.18, -32.92) * mm, v(322.45, -34.05) * mm]});
            skFitSpline(sketch, "E1232", {"points": [v(322.45, -34.05) * mm, v(321.45, -35.13) * mm, v(320.45, -36.21) * mm, v(319.45, -37.3) * mm]});
            skFitSpline(sketch, "E1233", {"points": [v(319.45, -37.3) * mm, v(316.65, -40.31) * mm, v(316.6, -40.57) * mm, v(318.74, -41.13) * mm]});
            skFitSpline(sketch, "E1234", {"points": [v(318.74, -41.13) * mm, v(320.17, -41.5) * mm, v(320.77, -42.42) * mm, v(320.34, -43.55) * mm]});
            skFitSpline(sketch, "E1235", {"points": [v(320.34, -43.55) * mm, v(319.95, -44.56) * mm, v(320.27, -45.77) * mm, v(321.04, -46.24) * mm]});
            skFitSpline(sketch, "E1236", {"points": [v(321.04, -46.24) * mm, v(322, -46.83) * mm, v(321.64, -47.85) * mm, v(319.9, -49.47) * mm]});
            skFitSpline(sketch, "E1237", {"points": [v(319.9, -49.47) * mm, v(318.5, -50.77) * mm, v(317.36, -52.57) * mm, v(317.36, -53.47) * mm]});
            skFitSpline(sketch, "E1238", {"points": [v(317.36, -53.47) * mm, v(317.36, -54.37) * mm, v(316.51, -55.8) * mm, v(315.48, -56.67) * mm]});
            skFitSpline(sketch, "E1239", {"points": [v(315.48, -56.67) * mm, v(314.43, -57.53) * mm, v(313.75, -59.65) * mm, v(313.95, -61.4) * mm]});
            skFitSpline(sketch, "E1240", {"points": [v(313.95, -61.4) * mm, v(314.14, -63.14) * mm, v(313.76, -64.75) * mm, v(313.08, -64.98) * mm]});
            skFitSpline(sketch, "E1241", {"points": [v(313.08, -64.98) * mm, v(312.41, -65.2) * mm, v(311.22, -65.92) * mm, v(310.44, -66.57) * mm]});
            skFitSpline(sketch, "E1242", {"points": [v(310.44, -66.57) * mm, v(309.53, -67.32) * mm, v(308.76, -67.32) * mm, v(308.29, -66.55) * mm]});
            skFitSpline(sketch, "E1243", {"points": [v(308.29, -66.55) * mm, v(308.29, -66.55) * mm, v(308.29, -66.55) * mm, v(308.29, -66.55) * mm, v(308.29, -66.55) * mm]});
            skFitSpline(sketch, "E1244", {"points": [v(422.06, -64.7) * mm, v(419.58, -60.91) * mm, v(421.34, -59.46) * mm, v(424.36, -62.8) * mm]});
            skFitSpline(sketch, "E1245", {"points": [v(424.36, -62.8) * mm, v(425.87, -64.47) * mm, v(426.17, -65.63) * mm, v(425.32, -66.5) * mm]});
            skFitSpline(sketch, "E1246", {"points": [v(425.32, -66.5) * mm, v(424.46, -67.35) * mm, v(423.43, -66.79) * mm, v(422.06, -64.7) * mm]});
            skFitSpline(sketch, "E1247", {"points": [v(348.57, -64.02) * mm, v(348.12, -63.3) * mm, v(348.59, -62.4) * mm, v(349.6, -62.01) * mm]});
            skFitSpline(sketch, "E1248", {"points": [v(349.6, -62.01) * mm, v(352.09, -61.06) * mm, v(355.86, -61.87) * mm, v(355.86, -63.36) * mm]});
            skFitSpline(sketch, "E1249", {"points": [v(355.86, -63.36) * mm, v(355.86, -65.04) * mm, v(349.55, -65.61) * mm, v(348.57, -64.02) * mm]});
            skFitSpline(sketch, "E1250", {"points": [v(347.76, -59.75) * mm, v(347.68, -59.38) * mm, v(347.53, -58.66) * mm, v(347.44, -58.15) * mm]});
            skFitSpline(sketch, "E1251", {"points": [v(347.44, -58.15) * mm, v(347.35, -57.65) * mm, v(346.93, -56.68) * mm, v(346.53, -56.01) * mm]});
            skFitSpline(sketch, "E1252", {"points": [v(346.53, -56.01) * mm, v(346.12, -55.34) * mm, v(345.85, -52.92) * mm, v(345.93, -50.63) * mm]});
            skFitSpline(sketch, "E1253", {"points": [v(345.93, -50.63) * mm, v(346.04, -47.62) * mm, v(346.7, -46.38) * mm, v(348.3, -46.14) * mm]});
            skFitSpline(sketch, "E1254", {"points": [v(348.3, -46.14) * mm, v(351.4, -45.69) * mm, v(352.13, -48.55) * mm, v(350, -52.81) * mm]});
            skFitSpline(sketch, "E1255", {"points": [v(350, -52.81) * mm, v(348.84, -55.14) * mm, v(348.62, -56.84) * mm, v(349.39, -57.6) * mm]});
            skFitSpline(sketch, "E1256", {"points": [v(349.39, -57.6) * mm, v(350.15, -58.37) * mm, v(350.1, -59.08) * mm, v(349.25, -59.61) * mm]});
            skFitSpline(sketch, "E1257", {"points": [v(349.25, -59.61) * mm, v(348.51, -60.07) * mm, v(347.85, -60.13) * mm, v(347.76, -59.75) * mm]});
            skFitSpline(sketch, "E1258", {"points": [v(353.48, -59.17) * mm, v(352.21, -57.12) * mm, v(354.01, -54.9) * mm, v(355.63, -56.52) * mm]});
            skFitSpline(sketch, "E1259", {"points": [v(355.63, -56.52) * mm, v(356.59, -57.47) * mm, v(356.59, -58.22) * mm, v(355.63, -59.17) * mm]});
            skFitSpline(sketch, "E1260", {"points": [v(355.63, -59.17) * mm, v(354.68, -60.13) * mm, v(354.07, -60.13) * mm, v(353.48, -59.17) * mm]});
            skFitSpline(sketch, "E1261", {"points": [v(370.6, -57.95) * mm, v(370.2, -57.32) * mm, v(370.4, -56.47) * mm, v(371.03, -56.08) * mm]});
            skFitSpline(sketch, "E1262", {"points": [v(371.03, -56.08) * mm, v(371.67, -55.69) * mm, v(372.51, -55.88) * mm, v(372.9, -56.52) * mm]});
            skFitSpline(sketch, "E1263", {"points": [v(372.9, -56.52) * mm, v(373.3, -57.16) * mm, v(373.1, -58) * mm, v(372.47, -58.4) * mm]});
            skFitSpline(sketch, "E1264", {"points": [v(372.47, -58.4) * mm, v(371.83, -58.79) * mm, v(370.99, -58.59) * mm, v(370.6, -57.95) * mm]});
            skFitSpline(sketch, "E1265", {"points": [v(353.48, -53.06) * mm, v(353.09, -52.43) * mm, v(353.29, -51.58) * mm, v(353.92, -51.19) * mm]});
            skFitSpline(sketch, "E1266", {"points": [v(353.92, -51.19) * mm, v(354.56, -50.8) * mm, v(355.4, -51) * mm, v(355.8, -51.63) * mm]});
            skFitSpline(sketch, "E1267", {"points": [v(355.8, -51.63) * mm, v(356.2, -52.27) * mm, v(356, -53.11) * mm, v(355.35, -53.5) * mm]});
            skFitSpline(sketch, "E1268", {"points": [v(355.35, -53.5) * mm, v(354.72, -53.9) * mm, v(353.87, -53.7) * mm, v(353.48, -53.06) * mm]});
            skFitSpline(sketch, "E1269", {"points": [v(348.6, -43.28) * mm, v(348.2, -42.65) * mm, v(348.4, -41.8) * mm, v(349.03, -41.41) * mm]});
            skFitSpline(sketch, "E1270", {"points": [v(349.03, -41.41) * mm, v(349.67, -41.02) * mm, v(350.51, -41.22) * mm, v(350.9, -41.85) * mm]});
            skFitSpline(sketch, "E1271", {"points": [v(350.9, -41.85) * mm, v(351.3, -42.49) * mm, v(351.1, -43.33) * mm, v(350.47, -43.73) * mm]});
            skFitSpline(sketch, "E1272", {"points": [v(350.47, -43.73) * mm, v(349.83, -44.12) * mm, v(348.99, -43.92) * mm, v(348.6, -43.28) * mm]});
            skFitSpline(sketch, "E1273", {"points": [v(325.37, -32.28) * mm, v(324.98, -31.65) * mm, v(325.18, -30.8) * mm, v(325.81, -30.41) * mm]});
            skFitSpline(sketch, "E1274", {"points": [v(325.81, -30.41) * mm, v(326.45, -30.02) * mm, v(327.3, -30.22) * mm, v(327.69, -30.85) * mm]});
            skFitSpline(sketch, "E1275", {"points": [v(327.69, -30.85) * mm, v(328.08, -31.49) * mm, v(327.88, -32.33) * mm, v(327.24, -32.73) * mm]});
            skFitSpline(sketch, "E1276", {"points": [v(327.24, -32.73) * mm, v(326.6, -33.12) * mm, v(325.76, -32.92) * mm, v(325.37, -32.28) * mm]});
            skFitSpline(sketch, "E1277", {"points": [v(337.78, -30.78) * mm, v(336.63, -30.14) * mm, v(335.7, -28.82) * mm, v(335.7, -27.84) * mm]});
            skFitSpline(sketch, "E1278", {"points": [v(335.7, -27.84) * mm, v(335.7, -25.74) * mm, v(334.26, -25.55) * mm, v(332.4, -27.4) * mm]});
            skFitSpline(sketch, "E1279", {"points": [v(332.4, -27.4) * mm, v(330.12, -29.68) * mm, v(329.18, -26.26) * mm, v(331.23, -23.12) * mm]});
            skFitSpline(sketch, "E1280", {"points": [v(331.23, -23.12) * mm, v(332.62, -21) * mm, v(332.74, -19.93) * mm, v(331.7, -18.9) * mm]});
            skFitSpline(sketch, "E1281", {"points": [v(331.7, -18.9) * mm, v(330.94, -18.14) * mm, v(330.7, -17.51) * mm, v(331.17, -17.51) * mm]});
            skFitSpline(sketch, "E1282", {"points": [v(331.17, -17.51) * mm, v(331.64, -17.51) * mm, v(332.44, -17.51) * mm, v(332.94, -17.51) * mm]});
            skFitSpline(sketch, "E1283", {"points": [v(332.94, -17.51) * mm, v(333.45, -17.51) * mm, v(333.87, -18.2) * mm, v(333.9, -19.04) * mm]});
            skFitSpline(sketch, "E1284", {"points": [v(333.9, -19.04) * mm, v(333.92, -20.54) * mm, v(334.53, -20.6) * mm, v(340.5, -19.76) * mm]});
            skFitSpline(sketch, "E1285", {"points": [v(340.5, -19.76) * mm, v(342.97, -19.42) * mm, v(343.61, -19.99) * mm, v(344.28, -23.13) * mm]});
            skFitSpline(sketch, "E1286", {"points": [v(344.28, -23.13) * mm, v(345.3, -27.9) * mm, v(341.21, -32.7) * mm, v(337.78, -30.78) * mm]});
            skFitSpline(sketch, "E1287", {"points": [v(366.74, -30.47) * mm, v(366.3, -29.3) * mm, v(366.53, -27.74) * mm, v(367.27, -27) * mm]});
            skFitSpline(sketch, "E1288", {"points": [v(367.27, -27) * mm, v(369.89, -25.3) * mm, v(370.04, -30.02) * mm, v(368.9, -31.24) * mm]});
            skFitSpline(sketch, "E1289", {"points": [v(368.9, -31.24) * mm, v(367.92, -32.22) * mm, v(367.33, -32.01) * mm, v(366.74, -30.47) * mm]});
            skFitSpline(sketch, "E1290", {"points": [v(203.94, -29.49) * mm, v(201.03, -26.59) * mm, v(202.86, -18.73) * mm, v(206.44, -18.73) * mm]});
            skFitSpline(sketch, "E1291", {"points": [v(206.44, -18.73) * mm, v(207.02, -18.73) * mm, v(208.33, -20.77) * mm, v(209.37, -23.25) * mm]});
            skFitSpline(sketch, "E1292", {"points": [v(209.37, -23.25) * mm, v(211.12, -27.44) * mm, v(211.1, -27.88) * mm, v(209.07, -29.36) * mm]});
            skFitSpline(sketch, "E1293", {"points": [v(209.07, -29.36) * mm, v(206.39, -31.33) * mm, v(205.79, -31.34) * mm, v(203.94, -29.49) * mm]});
            skFitSpline(sketch, "E1294", {"points": [v(316.78, -21.23) * mm, v(315.93, -19.86) * mm, v(319.35, -12.62) * mm, v(320.85, -12.62) * mm]});
            skFitSpline(sketch, "E1295", {"points": [v(320.85, -12.62) * mm, v(323.03, -12.62) * mm, v(323.29, -14.33) * mm, v(321.6, -17.6) * mm]});
            skFitSpline(sketch, "E1296", {"points": [v(321.6, -17.6) * mm, v(319.5, -21.63) * mm, v(317.82, -22.91) * mm, v(316.78, -21.23) * mm]});
            skFitSpline(sketch, "E1297", {"points": [v(336.73, -16.84) * mm, v(336.5, -15.37) * mm, v(336.06, -13.5) * mm, v(335.68, -12.32) * mm]});
            skFitSpline(sketch, "E1298", {"points": [v(335.68, -12.32) * mm, v(335.52, -11.81) * mm, v(335.3, -10.99) * mm, v(335.18, -10.48) * mm]});
            skFitSpline(sketch, "E1299", {"points": [v(335.18, -10.48) * mm, v(334.17, -6.14) * mm, v(332.65, -3.96) * mm, v(330.2, -3.35) * mm]});
            skFitSpline(sketch, "E1300", {"points": [v(330.2, -3.35) * mm, v(324.7, -1.97) * mm, v(323.14, 1.14) * mm, v(324.3, 8.37) * mm]});
            skFitSpline(sketch, "E1301", {"points": [v(324.3, 8.37) * mm, v(325.28, 14.57) * mm, v(325.5, 14.88) * mm, v(328.99, 14.82) * mm]});
            skFitSpline(sketch, "E1302", {"points": [v(328.99, 14.82) * mm, v(331.84, 14.78) * mm, v(332.73, 14.16) * mm, v(333.04, 11.97) * mm]});
            skFitSpline(sketch, "E1303", {"points": [v(333.04, 11.97) * mm, v(333.26, 10.43) * mm, v(332.5, 8.13) * mm, v(331.35, 6.85) * mm]});
            skFitSpline(sketch, "E1304", {"points": [v(331.35, 6.85) * mm, v(328.93, 4.18) * mm, v(329.3, 3.5) * mm, v(337.47, -4.27) * mm]});
            skFitSpline(sketch, "E1305", {"points": [v(337.47, -4.27) * mm, v(341.84, -8.42) * mm, v(342.4, -10.51) * mm, v(339.26, -10.94) * mm]});
            skFitSpline(sketch, "E1306", {"points": [v(339.26, -10.94) * mm, v(338.64, -11.03) * mm, v(337.8, -11.16) * mm, v(337.38, -11.25) * mm]});
            skFitSpline(sketch, "E1307", {"points": [v(337.38, -11.25) * mm, v(336.96, -11.33) * mm, v(337.32, -12.25) * mm, v(338.18, -13.29) * mm]});
            skFitSpline(sketch, "E1308", {"points": [v(338.18, -13.29) * mm, v(339.37, -14.71) * mm, v(339.4, -15.51) * mm, v(338.33, -16.59) * mm]});
            skFitSpline(sketch, "E1309", {"points": [v(338.33, -16.59) * mm, v(337.55, -17.36) * mm, v(336.83, -17.48) * mm, v(336.73, -16.84) * mm]});
            skFitSpline(sketch, "E1310", {"points": [v(341.26, -16.4) * mm, v(340.86, -15.76) * mm, v(341.06, -14.91) * mm, v(341.7, -14.52) * mm]});
            skFitSpline(sketch, "E1311", {"points": [v(341.7, -14.52) * mm, v(342.34, -14.13) * mm, v(343.18, -14.33) * mm, v(343.57, -14.96) * mm]});
            skFitSpline(sketch, "E1312", {"points": [v(343.57, -14.96) * mm, v(343.97, -15.6) * mm, v(343.77, -16.44) * mm, v(343.13, -16.84) * mm]});
            skFitSpline(sketch, "E1313", {"points": [v(343.13, -16.84) * mm, v(342.5, -17.23) * mm, v(341.65, -17.03) * mm, v(341.26, -16.4) * mm]});
            skFitSpline(sketch, "E1314", {"points": [v(326.6, -7.84) * mm, v(325.32, -5.78) * mm, v(327.12, -3.56) * mm, v(328.74, -5.18) * mm]});
            skFitSpline(sketch, "E1315", {"points": [v(328.74, -5.18) * mm, v(329.7, -6.14) * mm, v(329.7, -6.88) * mm, v(328.74, -7.84) * mm]});
            skFitSpline(sketch, "E1316", {"points": [v(328.74, -7.84) * mm, v(327.79, -8.8) * mm, v(327.18, -8.8) * mm, v(326.6, -7.84) * mm]});
            skFitSpline(sketch, "E1317", {"points": [v(337.6, -1.73) * mm, v(337.2, -1.09) * mm, v(337.4, -0.25) * mm, v(338.03, 0.15) * mm]});
            skFitSpline(sketch, "E1318", {"points": [v(338.03, 0.15) * mm, v(338.67, 0.54) * mm, v(339.51, 0.34) * mm, v(339.9, -0.3) * mm]});
            skFitSpline(sketch, "E1319", {"points": [v(339.9, -0.3) * mm, v(340.3, -0.93) * mm, v(340.1, -1.78) * mm, v(339.47, -2.17) * mm]});
            skFitSpline(sketch, "E1320", {"points": [v(339.47, -2.17) * mm, v(338.83, -2.56) * mm, v(337.99, -2.36) * mm, v(337.6, -1.73) * mm]});
            skFitSpline(sketch, "E1321", {"points": [v(-251.6, 11.52) * mm, v(-257.12, 12.53) * mm, v(-257.87, 13.1) * mm, v(-255.75, 14.66) * mm]});
            skFitSpline(sketch, "E1322", {"points": [v(-255.75, 14.66) * mm, v(-254.67, 15.45) * mm, v(-253.57, 16.62) * mm, v(-253.3, 17.25) * mm]});
            skFitSpline(sketch, "E1323", {"points": [v(-253.3, 17.25) * mm, v(-251.97, 20.4) * mm, v(-237.96, 17.1) * mm, v(-239.13, 13.9) * mm]});
            skFitSpline(sketch, "E1324", {"points": [v(-239.13, 13.9) * mm, v(-239.43, 13.1) * mm, v(-240.23, 12.55) * mm, v(-240.91, 12.7) * mm]});
            skFitSpline(sketch, "E1325", {"points": [v(-240.91, 12.7) * mm, v(-241.6, 12.84) * mm, v(-243.73, 12.53) * mm, v(-245.65, 12) * mm]});
            skFitSpline(sketch, "E1326", {"points": [v(-245.65, 12) * mm, v(-247.57, 11.49) * mm, v(-250.25, 11.27) * mm, v(-251.6, 11.52) * mm]});
            skFitSpline(sketch, "E1327", {"points": [v(-267.02, 18.85) * mm, v(-267.1, 19.35) * mm, v(-267.11, 20.12) * mm, v(-267.06, 20.56) * mm]});
            skFitSpline(sketch, "E1328", {"points": [v(-267.06, 20.56) * mm, v(-266.94, 21.48) * mm, v(-279.72, 27.71) * mm, v(-281.72, 27.71) * mm]});
            skFitSpline(sketch, "E1329", {"points": [v(-281.72, 27.71) * mm, v(-282.65, 27.71) * mm, v(-282.62, 27.18) * mm, v(-281.63, 25.99) * mm]});
            skFitSpline(sketch, "E1330", {"points": [v(-281.63, 25.99) * mm, v(-280.65, 24.8) * mm, v(-280.6, 24.01) * mm, v(-281.48, 23.47) * mm]});
            skFitSpline(sketch, "E1331", {"points": [v(-281.48, 23.47) * mm, v(-282.72, 22.7) * mm, v(-283.09, 23.21) * mm, v(-282.46, 24.82) * mm]});
            skFitSpline(sketch, "E1332", {"points": [v(-282.46, 24.82) * mm, v(-282.29, 25.25) * mm, v(-283.52, 26.11) * mm, v(-285.2, 26.74) * mm]});
            skFitSpline(sketch, "E1333", {"points": [v(-285.2, 26.74) * mm, v(-288.17, 27.85) * mm, v(-288.2, 27.93) * mm, v(-285.89, 29.63) * mm]});
            skFitSpline(sketch, "E1334", {"points": [v(-285.89, 29.63) * mm, v(-282.04, 32.47) * mm, v(-277.54, 31.68) * mm, v(-267, 26.33) * mm]});
            skFitSpline(sketch, "E1335", {"points": [v(-267, 26.33) * mm, v(-258.96, 22.26) * mm, v(-257.32, 20.97) * mm, v(-258.45, 19.61) * mm]});
            skFitSpline(sketch, "E1336", {"points": [v(-258.45, 19.61) * mm, v(-259.9, 17.86) * mm, v(-266.76, 17.25) * mm, v(-267.02, 18.85) * mm]});
            skFitSpline(sketch, "E1337", {"points": [v(326.16, 26.73) * mm, v(323.97, 28.93) * mm, v(324.4, 34.4) * mm, v(326.93, 36.7) * mm]});
            skFitSpline(sketch, "E1338", {"points": [v(326.93, 36.7) * mm, v(329.94, 39.42) * mm, v(330.68, 38.32) * mm, v(329.91, 32.22) * mm]});
            skFitSpline(sketch, "E1339", {"points": [v(329.91, 32.22) * mm, v(329.16, 26.18) * mm, v(328.17, 24.73) * mm, v(326.16, 26.73) * mm]});
            skFitSpline(sketch, "E1340", {"points": [v(346.12, 41.1) * mm, v(344.87, 43.12) * mm, v(347.96, 46.5) * mm, v(349.58, 44.87) * mm]});
            skFitSpline(sketch, "E1341", {"points": [v(349.58, 44.87) * mm, v(350.48, 43.97) * mm, v(350.28, 43) * mm, v(348.93, 41.64) * mm]});
            skFitSpline(sketch, "E1342", {"points": [v(348.93, 41.64) * mm, v(347.55, 40.26) * mm, v(346.73, 40.1) * mm, v(346.12, 41.1) * mm]});
            skFitSpline(sketch, "E1343", {"points": [v(354.5, 61.27) * mm, v(354.12, 62.24) * mm, v(354.17, 63.62) * mm, v(354.6, 64.33) * mm]});
            skFitSpline(sketch, "E1344", {"points": [v(354.6, 64.33) * mm, v(355.05, 65.04) * mm, v(354.29, 67.19) * mm, v(352.92, 69.1) * mm]});
            skFitSpline(sketch, "E1345", {"points": [v(352.92, 69.1) * mm, v(350.37, 72.69) * mm, v(350.75, 75.14) * mm, v(353.5, 72.86) * mm]});
            skFitSpline(sketch, "E1346", {"points": [v(353.5, 72.86) * mm, v(354.62, 71.93) * mm, v(355.84, 72.46) * mm, v(358.01, 74.8) * mm]});
            skFitSpline(sketch, "E1347", {"points": [v(358.01, 74.8) * mm, v(359.97, 76.9) * mm, v(362.76, 78.24) * mm, v(366.16, 78.7) * mm]});
            skFitSpline(sketch, "E1348", {"points": [v(366.16, 78.7) * mm, v(370.2, 79.24) * mm, v(371.58, 80.05) * mm, v(372.48, 82.4) * mm]});
            skFitSpline(sketch, "E1349", {"points": [v(372.48, 82.4) * mm, v(373.37, 84.76) * mm, v(373.99, 85.12) * mm, v(375.27, 84.05) * mm]});
            skFitSpline(sketch, "E1350", {"points": [v(375.27, 84.05) * mm, v(376.52, 83.02) * mm, v(377.29, 83.12) * mm, v(378.37, 84.42) * mm]});
            skFitSpline(sketch, "E1351", {"points": [v(378.37, 84.42) * mm, v(379.37, 85.63) * mm, v(379.42, 86.4) * mm, v(378.51, 86.97) * mm]});
            skFitSpline(sketch, "E1352", {"points": [v(378.51, 86.97) * mm, v(377.8, 87.4) * mm, v(377.54, 88.31) * mm, v(377.95, 88.97) * mm]});
            skFitSpline(sketch, "E1353", {"points": [v(377.95, 88.97) * mm, v(378.42, 89.73) * mm, v(379.3, 89.66) * mm, v(380.36, 88.78) * mm]});
            skFitSpline(sketch, "E1354", {"points": [v(380.36, 88.78) * mm, v(382.11, 87.33) * mm, v(382.82, 88.94) * mm, v(383.63, 96.16) * mm]});
            skFitSpline(sketch, "E1355", {"points": [v(383.63, 96.16) * mm, v(383.98, 99.31) * mm, v(386.47, 100.24) * mm, v(389.17, 98.22) * mm]});
            skFitSpline(sketch, "E1356", {"points": [v(389.17, 98.22) * mm, v(390.83, 96.98) * mm, v(391.25, 91) * mm, v(389.78, 89.55) * mm]});
            skFitSpline(sketch, "E1357", {"points": [v(389.78, 89.55) * mm, v(389.27, 89.06) * mm, v(388.04, 85.26) * mm, v(387.03, 81.12) * mm]});
            skFitSpline(sketch, "E1358", {"points": [v(387.03, 81.12) * mm, v(386.42, 78.6) * mm, v(385.8, 76.1) * mm, v(385.2, 73.59) * mm]});
            skFitSpline(sketch, "E1359", {"points": [v(385.2, 73.59) * mm, v(383.57, 73.58) * mm, v(381.94, 73.57) * mm, v(380.3, 73.57) * mm]});
            skFitSpline(sketch, "E1360", {"points": [v(380.3, 73.57) * mm, v(376.98, 73.55) * mm, v(374.79, 72.79) * mm, v(373.45, 71.18) * mm]});
            skFitSpline(sketch, "E1361", {"points": [v(373.45, 71.18) * mm, v(371.5, 68.84) * mm, v(371.45, 68.84) * mm, v(370.04, 71.48) * mm]});
            skFitSpline(sketch, "E1362", {"points": [v(370.04, 71.48) * mm, v(369.2, 73.05) * mm, v(367.5, 74.12) * mm, v(365.9, 74.08) * mm]});
            skFitSpline(sketch, "E1363", {"points": [v(365.9, 74.08) * mm, v(363.22, 74) * mm, v(363.23, 74) * mm, v(366.08, 72.84) * mm]});
            skFitSpline(sketch, "E1364", {"points": [v(366.08, 72.84) * mm, v(368.53, 71.86) * mm, v(368.73, 71.4) * mm, v(367.4, 69.78) * mm]});
            skFitSpline(sketch, "E1365", {"points": [v(367.4, 69.78) * mm, v(366.52, 68.73) * mm, v(364.87, 68.12) * mm, v(363.71, 68.42) * mm]});
            skFitSpline(sketch, "E1366", {"points": [v(363.71, 68.42) * mm, v(362.19, 68.82) * mm, v(361.1, 67.68) * mm, v(359.75, 64.23) * mm]});
            skFitSpline(sketch, "E1367", {"points": [v(359.75, 64.23) * mm, v(357.84, 59.35) * mm, v(355.7, 58.14) * mm, v(354.5, 61.27) * mm]});
            skFitSpline(sketch, "E1368", {"points": [v(38.14, 80.16) * mm, v(37.75, 80.8) * mm, v(37.95, 81.64) * mm, v(38.58, 82.04) * mm]});
            skFitSpline(sketch, "E1369", {"points": [v(38.58, 82.04) * mm, v(39.22, 82.43) * mm, v(40.07, 82.23) * mm, v(40.46, 81.6) * mm]});
            skFitSpline(sketch, "E1370", {"points": [v(40.46, 81.6) * mm, v(40.85, 80.96) * mm, v(40.65, 80.11) * mm, v(40.02, 79.72) * mm]});
            skFitSpline(sketch, "E1371", {"points": [v(40.02, 79.72) * mm, v(39.38, 79.33) * mm, v(38.54, 79.53) * mm, v(38.14, 80.16) * mm]});
            skFitSpline(sketch, "E1372", {"points": [v(-5.56, 95.9) * mm, v(-6.2, 99.22) * mm, v(-8.98, 99.05) * mm, v(-8.98, 95.68) * mm]});
            skFitSpline(sketch, "E1373", {"points": [v(-8.98, 95.68) * mm, v(-8.98, 93.37) * mm, v(-8.49, 92.75) * mm, v(-7.08, 93.3) * mm]});
            skFitSpline(sketch, "E1374", {"points": [v(-7.08, 93.3) * mm, v(-6.04, 93.7) * mm, v(-5.36, 94.87) * mm, v(-5.56, 95.9) * mm]});
            skFitSpline(sketch, "E1375", {"points": [v(-24.87, 93.03) * mm, v(-24.87, 93.4) * mm, v(-24.87, 94.12) * mm, v(-24.87, 94.63) * mm]});
            skFitSpline(sketch, "E1376", {"points": [v(-24.87, 94.63) * mm, v(-24.87, 95.13) * mm, v(-24.45, 95.55) * mm, v(-23.95, 95.56) * mm]});
            skFitSpline(sketch, "E1377", {"points": [v(-23.95, 95.56) * mm, v(-23.45, 95.57) * mm, v(-22.38, 96) * mm, v(-21.6, 96.5) * mm]});
            skFitSpline(sketch, "E1378", {"points": [v(-21.6, 96.5) * mm, v(-20.8, 97) * mm, v(-19.8, 96.86) * mm, v(-19.38, 96.18) * mm]});
            skFitSpline(sketch, "E1379", {"points": [v(-19.38, 96.18) * mm, v(-18.96, 95.5) * mm, v(-18.92, 94.86) * mm, v(-19.3, 94.78) * mm]});
            skFitSpline(sketch, "E1380", {"points": [v(-19.3, 94.78) * mm, v(-19.67, 94.7) * mm, v(-20.4, 94.55) * mm, v(-20.9, 94.46) * mm]});
            skFitSpline(sketch, "E1381", {"points": [v(-20.9, 94.46) * mm, v(-21.4, 94.36) * mm, v(-22.5, 93.85) * mm, v(-23.34, 93.31) * mm]});
            skFitSpline(sketch, "E1382", {"points": [v(-23.34, 93.31) * mm, v(-24.18, 92.78) * mm, v(-24.87, 92.65) * mm, v(-24.87, 93.03) * mm]});
            skFitSpline(sketch, "E1383", {"points": [v(384.58, 104.1) * mm, v(383.2, 107.74) * mm, v(383.85, 109.6) * mm, v(386.5, 109.6) * mm]});
            skFitSpline(sketch, "E1384", {"points": [v(386.5, 109.6) * mm, v(387.62, 109.6) * mm, v(388.25, 110.88) * mm, v(388.25, 113.2) * mm]});
            skFitSpline(sketch, "E1385", {"points": [v(388.25, 113.2) * mm, v(388.25, 118.1) * mm, v(389.8, 118.66) * mm, v(393.2, 115.03) * mm]});
            skFitSpline(sketch, "E1386", {"points": [v(393.2, 115.03) * mm, v(394.79, 113.35) * mm, v(396.84, 112.27) * mm, v(397.78, 112.62) * mm]});
            skFitSpline(sketch, "E1387", {"points": [v(397.78, 112.62) * mm, v(398.7, 112.98) * mm, v(399.97, 112.96) * mm, v(400.59, 112.59) * mm]});
            skFitSpline(sketch, "E1388", {"points": [v(400.59, 112.59) * mm, v(402.12, 111.64) * mm, v(399.6, 107.16) * mm, v(397.52, 107.16) * mm]});
            skFitSpline(sketch, "E1389", {"points": [v(397.52, 107.16) * mm, v(396.62, 107.16) * mm, v(395.19, 106.32) * mm, v(394.34, 105.3) * mm]});
            skFitSpline(sketch, "E1390", {"points": [v(394.34, 105.3) * mm, v(393.44, 104.2) * mm, v(391.84, 103.74) * mm, v(390.5, 104.16) * mm]});
            skFitSpline(sketch, "E1391", {"points": [v(390.5, 104.16) * mm, v(389.04, 104.63) * mm, v(388.31, 104.35) * mm, v(388.53, 103.43) * mm]});
            skFitSpline(sketch, "E1392", {"points": [v(388.53, 103.43) * mm, v(389.22, 100.4) * mm, v(385.77, 100.98) * mm, v(384.58, 104.1) * mm]});
            skFitSpline(sketch, "E1393", {"points": [v(-8.3, 103.38) * mm, v(-9.57, 105.44) * mm, v(-7.77, 107.66) * mm, v(-6.15, 106.04) * mm]});
            skFitSpline(sketch, "E1394", {"points": [v(-6.15, 106.04) * mm, v(-5.2, 105.08) * mm, v(-5.2, 104.34) * mm, v(-6.15, 103.38) * mm]});
            skFitSpline(sketch, "E1395", {"points": [v(-6.15, 103.38) * mm, v(-7.1, 102.43) * mm, v(-7.7, 102.43) * mm, v(-8.3, 103.38) * mm]});
            skFitSpline(sketch, "E1396", {"points": [v(-200.28, 123.3) * mm, v(-200.72, 124.44) * mm, v(-200.67, 126.04) * mm, v(-200.17, 126.86) * mm]});
            skFitSpline(sketch, "E1397", {"points": [v(-200.17, 126.86) * mm, v(-199.52, 127.9) * mm, v(-199.89, 128.1) * mm, v(-201.4, 127.53) * mm]});
            skFitSpline(sketch, "E1398", {"points": [v(-201.4, 127.53) * mm, v(-207.48, 125.2) * mm, v(-209.83, 125.16) * mm, v(-211.47, 127.4) * mm]});
            skFitSpline(sketch, "E1399", {"points": [v(-211.47, 127.4) * mm, v(-212.96, 129.44) * mm, v(-212.6, 130.16) * mm, v(-208.08, 134.3) * mm]});
            skFitSpline(sketch, "E1400", {"points": [v(-208.08, 134.3) * mm, v(-202.95, 138.99) * mm, v(-198.87, 139.54) * mm, v(-202.93, 134.98) * mm]});
            skFitSpline(sketch, "E1401", {"points": [v(-202.93, 134.98) * mm, v(-205.1, 132.55) * mm, v(-205.09, 132.52) * mm, v(-202.31, 133.38) * mm]});
            skFitSpline(sketch, "E1402", {"points": [v(-202.31, 133.38) * mm, v(-198.59, 134.54) * mm, v(-194.4, 130.98) * mm, v(-195.48, 127.58) * mm]});
            skFitSpline(sketch, "E1403", {"points": [v(-195.48, 127.58) * mm, v(-195.96, 126.08) * mm, v(-195.77, 125.48) * mm, v(-194.97, 125.97) * mm]});
            skFitSpline(sketch, "E1404", {"points": [v(-194.97, 125.97) * mm, v(-194.28, 126.4) * mm, v(-193.38, 126.23) * mm, v(-192.99, 125.6) * mm]});
            skFitSpline(sketch, "E1405", {"points": [v(-192.99, 125.6) * mm, v(-192.6, 124.96) * mm, v(-192.8, 124.11) * mm, v(-193.43, 123.72) * mm]});
            skFitSpline(sketch, "E1406", {"points": [v(-193.43, 123.72) * mm, v(-194.07, 123.33) * mm, v(-194.96, 123.6) * mm, v(-195.4, 124.32) * mm]});
            skFitSpline(sketch, "E1407", {"points": [v(-195.4, 124.32) * mm, v(-195.93, 125.17) * mm, v(-196.8, 124.85) * mm, v(-197.84, 123.42) * mm]});
            skFitSpline(sketch, "E1408", {"points": [v(-197.84, 123.42) * mm, v(-199.36, 121.37) * mm, v(-199.53, 121.36) * mm, v(-200.28, 123.3) * mm]});
            skFitSpline(sketch, "E1409", {"points": [v(-224.78, 132.12) * mm, v(-226.92, 133.7) * mm, v(-226.95, 133.95) * mm, v(-225.1, 134.66) * mm]});
            skFitSpline(sketch, "E1410", {"points": [v(-225.1, 134.66) * mm, v(-222.65, 135.62) * mm, v(-217.61, 133.18) * mm, v(-218.63, 131.54) * mm]});
            skFitSpline(sketch, "E1411", {"points": [v(-218.63, 131.54) * mm, v(-219.66, 129.88) * mm, v(-222.03, 130.1) * mm, v(-224.78, 132.12) * mm]});
            skFitSpline(sketch, "E1412", {"points": [v(-50.97, 137.34) * mm, v(-52.56, 138.92) * mm, v(-51.66, 140.2) * mm, v(-47.78, 141.89) * mm]});
            skFitSpline(sketch, "E1413", {"points": [v(-47.78, 141.89) * mm, v(-44.5, 143.33) * mm, v(-44.27, 143.64) * mm, v(-46.49, 143.72) * mm]});
            skFitSpline(sketch, "E1414", {"points": [v(-46.49, 143.72) * mm, v(-49.53, 143.84) * mm, v(-51.2, 145.7) * mm, v(-49.31, 146.88) * mm]});
            skFitSpline(sketch, "E1415", {"points": [v(-49.31, 146.88) * mm, v(-48.62, 147.3) * mm, v(-48.39, 148.2) * mm, v(-48.8, 148.88) * mm]});
            skFitSpline(sketch, "E1416", {"points": [v(-48.8, 148.88) * mm, v(-49.22, 149.55) * mm, v(-48.46, 150.38) * mm, v(-47.13, 150.74) * mm]});
            skFitSpline(sketch, "E1417", {"points": [v(-47.13, 150.74) * mm, v(-42.34, 152.31) * mm, v(-47.03, 159.33) * mm, v(-47.63, 155.03) * mm]});
            skFitSpline(sketch, "E1418", {"points": [v(-47.63, 155.03) * mm, v(-47.91, 152.42) * mm, v(-48.08, 152.23) * mm, v(-49.37, 153.03) * mm]});
            skFitSpline(sketch, "E1419", {"points": [v(-49.37, 153.03) * mm, v(-50.25, 153.57) * mm, v(-50.22, 154.34) * mm, v(-49.28, 155.48) * mm]});
            skFitSpline(sketch, "E1420", {"points": [v(-49.28, 155.48) * mm, v(-48.22, 156.75) * mm, v(-48.48, 157.63) * mm, v(-50.4, 159.27) * mm]});
            skFitSpline(sketch, "E1421", {"points": [v(-50.4, 159.27) * mm, v(-52.16, 160.78) * mm, v(-52.53, 161.84) * mm, v(-51.65, 162.9) * mm]});
            skFitSpline(sketch, "E1422", {"points": [v(-51.65, 162.9) * mm, v(-50.88, 163.83) * mm, v(-50.85, 164.65) * mm, v(-51.58, 165.1) * mm]});
            skFitSpline(sketch, "E1423", {"points": [v(-51.58, 165.1) * mm, v(-53.59, 166.35) * mm, v(-51.55, 171.15) * mm, v(-47.2, 175.45) * mm]});
            skFitSpline(sketch, "E1424", {"points": [v(-47.2, 175.45) * mm, v(-42.31, 180.26) * mm, v(-39.15, 179.2) * mm, v(-43.17, 174.1) * mm]});
            skFitSpline(sketch, "E1425", {"points": [v(-43.17, 174.1) * mm, v(-45.86, 170.67) * mm, v(-46.4, 168.88) * mm, v(-44.36, 170.14) * mm]});
            skFitSpline(sketch, "E1426", {"points": [v(-44.36, 170.14) * mm, v(-43.66, 170.57) * mm, v(-42.23, 170.6) * mm, v(-41.18, 170.2) * mm]});
            skFitSpline(sketch, "E1427", {"points": [v(-41.18, 170.2) * mm, v(-39.46, 169.54) * mm, v(-39.47, 169.16) * mm, v(-41.26, 166.42) * mm]});
            skFitSpline(sketch, "E1428", {"points": [v(-41.26, 166.42) * mm, v(-44, 162.78) * mm, v(-39.9, 161.5) * mm, v(-37.89, 159.02) * mm]});
            skFitSpline(sketch, "E1429", {"points": [v(-37.89, 159.02) * mm, v(-34.83, 155.18) * mm, v(-33.87, 153.14) * mm, v(-33.52, 149.63) * mm]});
            skFitSpline(sketch, "E1430", {"points": [v(-33.52, 149.63) * mm, v(-33.47, 149.12) * mm, v(-32.63, 148.71) * mm, v(-31.66, 148.71) * mm]});
            skFitSpline(sketch, "E1431", {"points": [v(-31.66, 148.71) * mm, v(-29.06, 148.71) * mm, v(-28.37, 146.86) * mm, v(-29.68, 143.42) * mm]});
            skFitSpline(sketch, "E1432", {"points": [v(-29.68, 143.42) * mm, v(-31, 139.91) * mm, v(-32.85, 139.15) * mm, v(-41.68, 138.41) * mm]});
            skFitSpline(sketch, "E1433", {"points": [v(-41.68, 138.41) * mm, v(-45.18, 138.12) * mm, v(-48.53, 137.59) * mm, v(-49.12, 137.22) * mm]});
            skFitSpline(sketch, "E1434", {"points": [v(-49.12, 137.22) * mm, v(-49.7, 136.86) * mm, v(-50.54, 136.9) * mm, v(-50.97, 137.34) * mm]});
            skFitSpline(sketch, "E1435", {"points": [v(-431.17, 143.18) * mm, v(-433.24, 148.13) * mm, v(-432.68, 150.9) * mm, v(-430.05, 148.72) * mm]});
            skFitSpline(sketch, "E1436", {"points": [v(-430.05, 148.72) * mm, v(-427.84, 146.89) * mm, v(-426.59, 141.29) * mm, v(-428.06, 139.82) * mm]});
            skFitSpline(sketch, "E1437", {"points": [v(-428.06, 139.82) * mm, v(-428.85, 139.03) * mm, v(-429.92, 140.18) * mm, v(-431.17, 143.18) * mm]});
            skFitSpline(sketch, "E1438", {"points": [v(-64.82, 144.6) * mm, v(-65.24, 145.7) * mm, v(-64.99, 147.55) * mm, v(-64.26, 148.72) * mm]});
            skFitSpline(sketch, "E1439", {"points": [v(-64.26, 148.72) * mm, v(-63.3, 150.25) * mm, v(-63.3, 151.22) * mm, v(-64.27, 152.19) * mm]});
            skFitSpline(sketch, "E1440", {"points": [v(-64.27, 152.19) * mm, v(-65.25, 153.16) * mm, v(-64.8, 153.85) * mm, v(-62.66, 154.7) * mm]});
            skFitSpline(sketch, "E1441", {"points": [v(-62.66, 154.7) * mm, v(-61.03, 155.36) * mm, v(-60.2, 155.93) * mm, v(-60.8, 155.97) * mm]});
            skFitSpline(sketch, "E1442", {"points": [v(-60.8, 155.97) * mm, v(-61.42, 156.01) * mm, v(-60.94, 157.13) * mm, v(-59.74, 158.45) * mm]});
            skFitSpline(sketch, "E1443", {"points": [v(-59.74, 158.45) * mm, v(-57.78, 160.62) * mm, v(-57.25, 160.68) * mm, v(-54.23, 159.12) * mm]});
            skFitSpline(sketch, "E1444", {"points": [v(-54.23, 159.12) * mm, v(-51.24, 157.57) * mm, v(-50.97, 156.93) * mm, v(-51.65, 152.75) * mm]});
            skFitSpline(sketch, "E1445", {"points": [v(-51.65, 152.75) * mm, v(-52.28, 148.93) * mm, v(-53.27, 147.63) * mm, v(-57.28, 145.45) * mm]});
            skFitSpline(sketch, "E1446", {"points": [v(-57.28, 145.45) * mm, v(-63.3, 142.17) * mm, v(-62.16, 144.6) * mm, v(-64.82, 144.6) * mm]});
            skFitSpline(sketch, "E1447", {"points": [v(-64.82, 144.6) * mm, v(-64.82, 144.6) * mm, v(-64.82, 144.6) * mm, v(-64.82, 144.6) * mm]});
            skFitSpline(sketch, "E1448", {"points": [v(-494.6, 166.62) * mm, v(-495.06, 167.08) * mm, v(-495.43, 167.87) * mm, v(-495.43, 168.39) * mm]});
            skFitSpline(sketch, "E1449", {"points": [v(-495.43, 168.39) * mm, v(-495.43, 169.96) * mm, v(-488.31, 174.5) * mm, v(-487.61, 173.37) * mm]});
            skFitSpline(sketch, "E1450", {"points": [v(-487.61, 173.37) * mm, v(-486.78, 172) * mm, v(-493.5, 165.52) * mm, v(-494.6, 166.62) * mm]});
            skFitSpline(sketch, "E1451", {"points": [v(-442.2, 169.39) * mm, v(-442.6, 170.02) * mm, v(-442.4, 170.87) * mm, v(-441.76, 171.26) * mm]});
            skFitSpline(sketch, "E1452", {"points": [v(-441.76, 171.26) * mm, v(-441.12, 171.65) * mm, v(-440.28, 171.45) * mm, v(-439.88, 170.82) * mm]});
            skFitSpline(sketch, "E1453", {"points": [v(-439.88, 170.82) * mm, v(-439.49, 170.18) * mm, v(-439.69, 169.34) * mm, v(-440.33, 168.94) * mm]});
            skFitSpline(sketch, "E1454", {"points": [v(-440.33, 168.94) * mm, v(-440.96, 168.55) * mm, v(-441.8, 168.75) * mm, v(-442.2, 169.39) * mm]});
            skFitSpline(sketch, "E1455", {"points": [v(-171.4, 182.16) * mm, v(-172.13, 183.04) * mm, v(-172.33, 184.2) * mm, v(-171.83, 184.73) * mm]});
            skFitSpline(sketch, "E1456", {"points": [v(-171.83, 184.73) * mm, v(-171.33, 185.25) * mm, v(-172.1, 185.32) * mm, v(-173.54, 184.88) * mm]});
            skFitSpline(sketch, "E1457", {"points": [v(-173.54, 184.88) * mm, v(-175.38, 184.32) * mm, v(-177.3, 185.05) * mm, v(-180.07, 187.38) * mm]});
            skFitSpline(sketch, "E1458", {"points": [v(-180.07, 187.38) * mm, v(-184.63, 191.22) * mm, v(-190.53, 199.96) * mm, v(-190.07, 202.2) * mm]});
            skFitSpline(sketch, "E1459", {"points": [v(-190.07, 202.2) * mm, v(-189.9, 203.06) * mm, v(-190.44, 203.6) * mm, v(-191.28, 203.43) * mm]});
            skFitSpline(sketch, "E1460", {"points": [v(-191.28, 203.43) * mm, v(-192.13, 203.25) * mm, v(-192.85, 203.65) * mm, v(-192.89, 204.32) * mm]});
            skFitSpline(sketch, "E1461", {"points": [v(-192.89, 204.32) * mm, v(-192.93, 205) * mm, v(-193.38, 206.2) * mm, v(-193.89, 207) * mm]});
            skFitSpline(sketch, "E1462", {"points": [v(-193.89, 207) * mm, v(-194.43, 207.85) * mm, v(-193.91, 208.97) * mm, v(-192.65, 209.71) * mm]});
            skFitSpline(sketch, "E1463", {"points": [v(-192.65, 209.71) * mm, v(-191.45, 210.4) * mm, v(-190.98, 210.99) * mm, v(-191.59, 211) * mm]});
            skFitSpline(sketch, "E1464", {"points": [v(-191.59, 211) * mm, v(-192.2, 211.03) * mm, v(-191.7, 212.15) * mm, v(-190.48, 213.5) * mm]});
            skFitSpline(sketch, "E1465", {"points": [v(-190.48, 213.5) * mm, v(-188.22, 216) * mm, v(-189.53, 217) * mm, v(-191.93, 214.6) * mm]});
            skFitSpline(sketch, "E1466", {"points": [v(-191.93, 214.6) * mm, v(-192.89, 213.65) * mm, v(-193.5, 213.67) * mm, v(-194.12, 214.66) * mm]});
            skFitSpline(sketch, "E1467", {"points": [v(-194.12, 214.66) * mm, v(-195.2, 216.43) * mm, v(-192.62, 219.6) * mm, v(-190.03, 219.64) * mm]});
            skFitSpline(sketch, "E1468", {"points": [v(-190.03, 219.64) * mm, v(-188.34, 219.67) * mm, v(-188.38, 219.87) * mm, v(-190.28, 220.98) * mm]});
            skFitSpline(sketch, "E1469", {"points": [v(-190.28, 220.98) * mm, v(-192.42, 222.23) * mm, v(-192.4, 222.4) * mm, v(-189.93, 225.04) * mm]});
            skFitSpline(sketch, "E1470", {"points": [v(-189.93, 225.04) * mm, v(-186.88, 228.29) * mm, v(-188.23, 230.13) * mm, v(-194.15, 230.8) * mm]});
            skFitSpline(sketch, "E1471", {"points": [v(-194.15, 230.8) * mm, v(-198.5, 231.3) * mm, v(-198.98, 233.27) * mm, v(-195, 234.21) * mm]});
            skFitSpline(sketch, "E1472", {"points": [v(-195, 234.21) * mm, v(-192.03, 234.91) * mm, v(-191.72, 235.76) * mm, v(-192.92, 239.77) * mm]});
            skFitSpline(sketch, "E1473", {"points": [v(-192.92, 239.77) * mm, v(-193.63, 242.1) * mm, v(-193.72, 242.08) * mm, v(-194.82, 239.36) * mm]});
            skFitSpline(sketch, "E1474", {"points": [v(-194.82, 239.36) * mm, v(-196.4, 235.48) * mm, v(-199.04, 236.68) * mm, v(-199.04, 241.28) * mm]});
            skFitSpline(sketch, "E1475", {"points": [v(-199.04, 241.28) * mm, v(-199.04, 243.33) * mm, v(-200, 246.08) * mm, v(-201.18, 247.38) * mm]});
            skFitSpline(sketch, "E1476", {"points": [v(-201.18, 247.38) * mm, v(-202.35, 248.68) * mm, v(-203.32, 250.17) * mm, v(-203.32, 250.7) * mm]});
            skFitSpline(sketch, "E1477", {"points": [v(-203.32, 250.7) * mm, v(-203.32, 251.23) * mm, v(-204.97, 253.55) * mm, v(-206.98, 255.84) * mm]});
            skFitSpline(sketch, "E1478", {"points": [v(-206.98, 255.84) * mm, v(-209, 258.14) * mm, v(-210.65, 260.58) * mm, v(-210.65, 261.27) * mm]});
            skFitSpline(sketch, "E1479", {"points": [v(-210.65, 261.27) * mm, v(-210.65, 261.96) * mm, v(-211.1, 262.25) * mm, v(-211.64, 261.91) * mm]});
            skFitSpline(sketch, "E1480", {"points": [v(-211.64, 261.91) * mm, v(-212.19, 261.57) * mm, v(-217, 261.2) * mm, v(-222.33, 261.06) * mm]});
            skFitSpline(sketch, "E1481", {"points": [v(-222.33, 261.06) * mm, v(-227.67, 260.93) * mm, v(-233.14, 260.42) * mm, v(-234.48, 259.92) * mm]});
            skFitSpline(sketch, "E1482", {"points": [v(-234.48, 259.92) * mm, v(-237.44, 258.84) * mm, v(-242.89, 260.65) * mm, v(-241.82, 262.37) * mm]});
            skFitSpline(sketch, "E1483", {"points": [v(-241.82, 262.37) * mm, v(-241.4, 263.05) * mm, v(-242.16, 263.6) * mm, v(-243.5, 263.6) * mm]});
            skFitSpline(sketch, "E1484", {"points": [v(-243.5, 263.6) * mm, v(-244.85, 263.6) * mm, v(-246.29, 264.15) * mm, v(-246.7, 264.83) * mm]});
            skFitSpline(sketch, "E1485", {"points": [v(-246.7, 264.83) * mm, v(-247.6, 266.26) * mm, v(-242.34, 268.5) * mm, v(-238.07, 268.5) * mm]});
            skFitSpline(sketch, "E1486", {"points": [v(-238.07, 268.5) * mm, v(-236.43, 268.5) * mm, v(-235.1, 269) * mm, v(-235.1, 269.61) * mm]});
            skFitSpline(sketch, "E1487", {"points": [v(-235.1, 269.61) * mm, v(-235.1, 270.23) * mm, v(-237.1, 270.57) * mm, v(-239.56, 270.38) * mm]});
            skFitSpline(sketch, "E1488", {"points": [v(-239.56, 270.38) * mm, v(-245.05, 269.94) * mm, v(-250.05, 271.19) * mm, v(-250.7, 273.16) * mm]});
            skFitSpline(sketch, "E1489", {"points": [v(-250.7, 273.16) * mm, v(-251.29, 274.9) * mm, v(-242.89, 278.7) * mm, v(-240.49, 277.79) * mm]});
            skFitSpline(sketch, "E1490", {"points": [v(-240.49, 277.79) * mm, v(-239.58, 277.44) * mm, v(-238.51, 277.68) * mm, v(-238.12, 278.32) * mm]});
            skFitSpline(sketch, "E1491", {"points": [v(-238.12, 278.32) * mm, v(-237.72, 278.97) * mm, v(-236, 279.5) * mm, v(-234.3, 279.5) * mm]});
            skFitSpline(sketch, "E1492", {"points": [v(-234.3, 279.5) * mm, v(-231.58, 279.5) * mm, v(-226.7, 283.5) * mm, v(-226.58, 285.82) * mm]});
            skFitSpline(sketch, "E1493", {"points": [v(-226.58, 285.82) * mm, v(-226.56, 286.28) * mm, v(-228.3, 286.15) * mm, v(-230.47, 285.53) * mm]});
            skFitSpline(sketch, "E1494", {"points": [v(-230.47, 285.53) * mm, v(-233.43, 284.68) * mm, v(-234.84, 284.83) * mm, v(-236.15, 286.13) * mm]});
            skFitSpline(sketch, "E1495", {"points": [v(-236.15, 286.13) * mm, v(-237.65, 287.64) * mm, v(-237.14, 288.22) * mm, v(-232.38, 290.46) * mm]});
            skFitSpline(sketch, "E1496", {"points": [v(-232.38, 290.46) * mm, v(-229.35, 291.88) * mm, v(-226.38, 292.96) * mm, v(-225.79, 292.85) * mm]});
            skFitSpline(sketch, "E1497", {"points": [v(-225.79, 292.85) * mm, v(-225.2, 292.74) * mm, v(-224.15, 292.78) * mm, v(-223.48, 292.93) * mm]});
            skFitSpline(sketch, "E1498", {"points": [v(-223.48, 292.93) * mm, v(-222.8, 293.1) * mm, v(-221.43, 293.3) * mm, v(-220.43, 293.38) * mm]});
            skFitSpline(sketch, "E1499", {"points": [v(-220.43, 293.38) * mm, v(-219.42, 293.47) * mm, v(-218.59, 294.52) * mm, v(-218.58, 295.71) * mm]});
            skFitSpline(sketch, "E1500", {"points": [v(-218.58, 295.71) * mm, v(-218.56, 299.3) * mm, v(-212.14, 301.77) * mm, v(-204.3, 301.22) * mm]});
            skFitSpline(sketch, "E1501", {"points": [v(-204.3, 301.22) * mm, v(-200.48, 300.95) * mm, v(-197.6, 301.14) * mm, v(-197.9, 301.64) * mm]});
            skFitSpline(sketch, "E1502", {"points": [v(-197.9, 301.64) * mm, v(-199.22, 303.76) * mm, v(-195.62, 303.98) * mm, v(-193.34, 301.92) * mm]});
            skFitSpline(sketch, "E1503", {"points": [v(-193.34, 301.92) * mm, v(-190.91, 299.73) * mm, v(-190.86, 299.73) * mm, v(-191.27, 302.03) * mm]});
            skFitSpline(sketch, "E1504", {"points": [v(-191.27, 302.03) * mm, v(-191.6, 303.88) * mm, v(-190.77, 304.6) * mm, v(-187.46, 305.29) * mm]});
            skFitSpline(sketch, "E1505", {"points": [v(-187.46, 305.29) * mm, v(-185.13, 305.78) * mm, v(-182.33, 305.7) * mm, v(-181.24, 305.12) * mm]});
            skFitSpline(sketch, "E1506", {"points": [v(-181.24, 305.12) * mm, v(-179.7, 304.3) * mm, v(-171.35, 304.24) * mm, v(-169.4, 305.04) * mm]});
            skFitSpline(sketch, "E1507", {"points": [v(-169.4, 305.04) * mm, v(-169.23, 305.1) * mm, v(-170.05, 306.15) * mm, v(-171.23, 307.35) * mm]});
            skFitSpline(sketch, "E1508", {"points": [v(-171.23, 307.35) * mm, v(-173.07, 309.23) * mm, v(-173.56, 309.29) * mm, v(-174.71, 307.77) * mm]});
            skFitSpline(sketch, "E1509", {"points": [v(-174.71, 307.77) * mm, v(-176.2, 305.82) * mm, v(-178.87, 306.84) * mm, v(-178.87, 309.36) * mm]});
            skFitSpline(sketch, "E1510", {"points": [v(-178.87, 309.36) * mm, v(-178.87, 312.18) * mm, v(-175.25, 314.35) * mm, v(-172.96, 312.9) * mm]});
            skFitSpline(sketch, "E1511", {"points": [v(-172.96, 312.9) * mm, v(-171.62, 312.05) * mm, v(-170.04, 312) * mm, v(-168.34, 312.78) * mm]});
            skFitSpline(sketch, "E1512", {"points": [v(-168.34, 312.78) * mm, v(-166.49, 313.62) * mm, v(-164.7, 313.4) * mm, v(-161.99, 312) * mm]});
            skFitSpline(sketch, "E1513", {"points": [v(-161.99, 312) * mm, v(-157.52, 309.69) * mm, v(-155.53, 309.51) * mm, v(-155.95, 311.47) * mm]});
            skFitSpline(sketch, "E1514", {"points": [v(-155.95, 311.47) * mm, v(-156.33, 313.24) * mm, v(-148.58, 315.1) * mm, v(-145.26, 314.05) * mm]});
            skFitSpline(sketch, "E1515", {"points": [v(-145.26, 314.05) * mm, v(-143.91, 313.62) * mm, v(-140.06, 313.23) * mm, v(-136.7, 313.19) * mm]});
            skFitSpline(sketch, "E1516", {"points": [v(-136.7, 313.19) * mm, v(-129.45, 313.09) * mm, v(-127.74, 310.97) * mm, v(-134.1, 309.93) * mm]});
            skFitSpline(sketch, "E1517", {"points": [v(-134.1, 309.93) * mm, v(-136.55, 309.53) * mm, v(-138.93, 308.84) * mm, v(-139.37, 308.4) * mm]});
            skFitSpline(sketch, "E1518", {"points": [v(-139.37, 308.4) * mm, v(-140.34, 307.43) * mm, v(-129.89, 308.62) * mm, v(-123.87, 310.16) * mm]});
            skFitSpline(sketch, "E1519", {"points": [v(-123.87, 310.16) * mm, v(-118.25, 311.6) * mm, v(-108.31, 311.58) * mm, v(-107.41, 310.12) * mm]});
            skFitSpline(sketch, "E1520", {"points": [v(-107.41, 310.12) * mm, v(-107.02, 309.5) * mm, v(-107.68, 308.38) * mm, v(-108.87, 307.65) * mm]});
            skFitSpline(sketch, "E1521", {"points": [v(-108.87, 307.65) * mm, v(-110.52, 306.64) * mm, v(-109.38, 306.5) * mm, v(-104.15, 307.08) * mm]});
            skFitSpline(sketch, "E1522", {"points": [v(-104.15, 307.08) * mm, v(-99.78, 307.57) * mm, v(-96.98, 307.37) * mm, v(-96.47, 306.54) * mm]});
            skFitSpline(sketch, "E1523", {"points": [v(-96.47, 306.54) * mm, v(-95.23, 304.55) * mm, v(-103.8, 301.5) * mm, v(-110.63, 301.5) * mm]});
            skFitSpline(sketch, "E1524", {"points": [v(-110.63, 301.5) * mm, v(-116.7, 301.5) * mm, v(-138.04, 294.2) * mm, v(-134.97, 293.17) * mm]});
            skFitSpline(sketch, "E1525", {"points": [v(-134.97, 293.17) * mm, v(-134.15, 292.9) * mm, v(-130.08, 294.23) * mm, v(-125.92, 296.13) * mm]});
            skFitSpline(sketch, "E1526", {"points": [v(-125.92, 296.13) * mm, v(-119.83, 298.9) * mm, v(-116.6, 299.58) * mm, v(-109.2, 299.62) * mm]});
            skFitSpline(sketch, "E1527", {"points": [v(-109.2, 299.62) * mm, v(-101.38, 299.65) * mm, v(-100.08, 299.37) * mm, v(-100.36, 297.66) * mm]});
            skFitSpline(sketch, "E1528", {"points": [v(-100.36, 297.66) * mm, v(-100.66, 295.82) * mm, v(-100.35, 295.82) * mm, v(-96.46, 297.58) * mm]});
            skFitSpline(sketch, "E1529", {"points": [v(-96.46, 297.58) * mm, v(-94.13, 298.63) * mm, v(-92.48, 299.9) * mm, v(-92.79, 300.41) * mm]});
            skFitSpline(sketch, "E1530", {"points": [v(-92.79, 300.41) * mm, v(-93.1, 300.91) * mm, v(-92.83, 301.65) * mm, v(-92.2, 302.04) * mm]});
            skFitSpline(sketch, "E1531", {"points": [v(-92.2, 302.04) * mm, v(-91.56, 302.43) * mm, v(-90.71, 302.23) * mm, v(-90.32, 301.6) * mm]});
            skFitSpline(sketch, "E1532", {"points": [v(-90.32, 301.6) * mm, v(-89.93, 300.96) * mm, v(-90.17, 300.09) * mm, v(-90.87, 299.66) * mm]});
            skFitSpline(sketch, "E1533", {"points": [v(-90.87, 299.66) * mm, v(-93.65, 297.94) * mm, v(-90.6, 296.94) * mm, v(-86.3, 298.14) * mm]});
            skFitSpline(sketch, "E1534", {"points": [v(-86.3, 298.14) * mm, v(-80.54, 299.76) * mm, v(-71.52, 299.74) * mm, v(-69.9, 298.12) * mm]});
            skFitSpline(sketch, "E1535", {"points": [v(-69.9, 298.12) * mm, v(-68.5, 296.73) * mm, v(-75.05, 292.94) * mm, v(-78.83, 292.94) * mm]});
            skFitSpline(sketch, "E1536", {"points": [v(-78.83, 292.94) * mm, v(-80.08, 292.94) * mm, v(-80.95, 292.25) * mm, v(-80.79, 291.4) * mm]});
            skFitSpline(sketch, "E1537", {"points": [v(-80.79, 291.4) * mm, v(-80.58, 290.4) * mm, v(-82.38, 289.75) * mm, v(-85.98, 289.5) * mm]});
            skFitSpline(sketch, "E1538", {"points": [v(-85.98, 289.5) * mm, v(-89, 289.29) * mm, v(-92.03, 288.56) * mm, v(-92.7, 287.88) * mm]});
            skFitSpline(sketch, "E1539", {"points": [v(-92.7, 287.88) * mm, v(-93.52, 287.06) * mm, v(-92.86, 286.92) * mm, v(-90.7, 287.45) * mm]});
            skFitSpline(sketch, "E1540", {"points": [v(-90.7, 287.45) * mm, v(-87.18, 288.32) * mm, v(-84.91, 286.37) * mm, v(-87.57, 284.76) * mm]});
            skFitSpline(sketch, "E1541", {"points": [v(-87.57, 284.76) * mm, v(-88.48, 284.22) * mm, v(-89.58, 282.8) * mm, v(-90.02, 281.6) * mm]});
            skFitSpline(sketch, "E1542", {"points": [v(-90.02, 281.6) * mm, v(-90.46, 280.4) * mm, v(-92.06, 278.93) * mm, v(-93.6, 278.32) * mm]});
            skFitSpline(sketch, "E1543", {"points": [v(-93.6, 278.32) * mm, v(-96.16, 277.29) * mm, v(-96.04, 277.05) * mm, v(-92.7, 276.6) * mm]});
            skFitSpline(sketch, "E1544", {"points": [v(-92.7, 276.6) * mm, v(-90.9, 276.36) * mm, v(-91.2, 273.96) * mm, v(-93, 274.16) * mm]});
            skFitSpline(sketch, "E1545", {"points": [v(-93, 274.16) * mm, v(-93.85, 274.26) * mm, v(-94.54, 273.84) * mm, v(-94.54, 273.25) * mm]});
            skFitSpline(sketch, "E1546", {"points": [v(-94.54, 273.25) * mm, v(-94.54, 272.65) * mm, v(-93.99, 272.09) * mm, v(-93.31, 272) * mm]});
            skFitSpline(sketch, "E1547", {"points": [v(-93.31, 272) * mm, v(-90.88, 271.7) * mm, v(-90.23, 271.5) * mm, v(-88.73, 270.54) * mm]});
            skFitSpline(sketch, "E1548", {"points": [v(-88.73, 270.54) * mm, v(-85.6, 268.56) * mm, v(-87.18, 266.95) * mm, v(-91.55, 267.66) * mm]});
            skFitSpline(sketch, "E1549", {"points": [v(-91.55, 267.66) * mm, v(-93.94, 268.04) * mm, v(-96.83, 267.99) * mm, v(-97.97, 267.53) * mm]});
            skFitSpline(sketch, "E1550", {"points": [v(-97.97, 267.53) * mm, v(-99.45, 266.93) * mm, v(-98.83, 266.52) * mm, v(-95.76, 266.07) * mm]});
            skFitSpline(sketch, "E1551", {"points": [v(-95.76, 266.07) * mm, v(-90.52, 265.3) * mm, v(-90.16, 263.17) * mm, v(-95.15, 262.49) * mm]});
            skFitSpline(sketch, "E1552", {"points": [v(-95.15, 262.49) * mm, v(-99.2, 261.97) * mm, v(-99.2, 262.06) * mm, v(-95.22, 261.26) * mm]});
            skFitSpline(sketch, "E1553", {"points": [v(-95.22, 261.26) * mm, v(-93.24, 260.87) * mm, v(-91.69, 260) * mm, v(-91.77, 259.33) * mm]});
            skFitSpline(sketch, "E1554", {"points": [v(-91.77, 259.33) * mm, v(-91.85, 258.65) * mm, v(-91.12, 257.66) * mm, v(-90.15, 257.11) * mm]});
            skFitSpline(sketch, "E1555", {"points": [v(-90.15, 257.11) * mm, v(-87.44, 255.6) * mm, v(-89.33, 253.83) * mm, v(-93.7, 253.8) * mm]});
            skFitSpline(sketch, "E1556", {"points": [v(-93.7, 253.8) * mm, v(-97.69, 253.8) * mm, v(-98.1, 254.16) * mm, v(-94.79, 251.61) * mm]});
            skFitSpline(sketch, "E1557", {"points": [v(-94.79, 251.61) * mm, v(-92.05, 249.5) * mm, v(-92.24, 247.71) * mm, v(-95.18, 247.71) * mm]});
            skFitSpline(sketch, "E1558", {"points": [v(-95.18, 247.71) * mm, v(-96, 247.71) * mm, v(-98.19, 248.92) * mm, v(-100.06, 250.4) * mm]});
            skFitSpline(sketch, "E1559", {"points": [v(-100.06, 250.4) * mm, v(-104.43, 253.83) * mm, v(-107.85, 254.17) * mm, v(-107.63, 251.14) * mm]});
            skFitSpline(sketch, "E1560", {"points": [v(-107.63, 251.14) * mm, v(-107.5, 249.6) * mm, v(-106.65, 248.98) * mm, v(-104.97, 249.2) * mm]});
            skFitSpline(sketch, "E1561", {"points": [v(-104.97, 249.2) * mm, v(-103.5, 249.4) * mm, v(-102.6, 248.92) * mm, v(-102.79, 248.02) * mm]});
            skFitSpline(sketch, "E1562", {"points": [v(-102.79, 248.02) * mm, v(-102.95, 247.18) * mm, v(-102.08, 246.5) * mm, v(-100.85, 246.5) * mm]});
            skFitSpline(sketch, "E1563", {"points": [v(-100.85, 246.5) * mm, v(-99.62, 246.5) * mm, v(-98.25, 246.13) * mm, v(-97.8, 245.69) * mm]});
            skFitSpline(sketch, "E1564", {"points": [v(-97.8, 245.69) * mm, v(-96.43, 244.32) * mm, v(-99.49, 241.71) * mm, v(-101.65, 242.4) * mm]});
            skFitSpline(sketch, "E1565", {"points": [v(-101.65, 242.4) * mm, v(-102.95, 242.81) * mm, v(-102.65, 242.2) * mm, v(-100.82, 240.7) * mm]});
            skFitSpline(sketch, "E1566", {"points": [v(-100.82, 240.7) * mm, v(-97.55, 238.02) * mm, v(-97.67, 233.91) * mm, v(-101.05, 233.26) * mm]});
            skFitSpline(sketch, "E1567", {"points": [v(-101.05, 233.26) * mm, v(-102.48, 232.99) * mm, v(-103.5, 233.74) * mm, v(-103.93, 235.39) * mm]});
            skFitSpline(sketch, "E1568", {"points": [v(-103.93, 235.39) * mm, v(-104.38, 237.1) * mm, v(-105.58, 237.94) * mm, v(-107.58, 237.94) * mm]});
            skFitSpline(sketch, "E1569", {"points": [v(-107.58, 237.94) * mm, v(-109.52, 237.94) * mm, v(-110.26, 237.44) * mm, v(-109.7, 236.53) * mm]});
            skFitSpline(sketch, "E1570", {"points": [v(-109.7, 236.53) * mm, v(-109.22, 235.75) * mm, v(-109.87, 234.36) * mm, v(-111.14, 233.43) * mm]});
            skFitSpline(sketch, "E1571", {"points": [v(-111.14, 233.43) * mm, v(-113.3, 231.86) * mm, v(-113.2, 231.75) * mm, v(-109.8, 232) * mm]});
            skFitSpline(sketch, "E1572", {"points": [v(-109.8, 232) * mm, v(-97.88, 232.88) * mm, v(-94.43, 230.15) * mm, v(-103.96, 227.39) * mm]});
            skFitSpline(sketch, "E1573", {"points": [v(-103.96, 227.39) * mm, v(-106.69, 226.6) * mm, v(-110.2, 225.27) * mm, v(-111.75, 224.43) * mm]});
            skFitSpline(sketch, "E1574", {"points": [v(-111.75, 224.43) * mm, v(-113.31, 223.6) * mm, v(-118.05, 222.98) * mm, v(-122.28, 223.05) * mm]});
            skFitSpline(sketch, "E1575", {"points": [v(-122.28, 223.05) * mm, v(-128.59, 223.16) * mm, v(-130.4, 222.72) * mm, v(-132.32, 220.65) * mm]});
            skFitSpline(sketch, "E1576", {"points": [v(-132.32, 220.65) * mm, v(-133.62, 219.26) * mm, v(-135.31, 218.5) * mm, v(-136.08, 218.98) * mm]});
            skFitSpline(sketch, "E1577", {"points": [v(-136.08, 218.98) * mm, v(-136.9, 219.49) * mm, v(-137.36, 219.16) * mm, v(-137.2, 218.2) * mm]});
            skFitSpline(sketch, "E1578", {"points": [v(-137.2, 218.2) * mm, v(-136.49, 213.9) * mm, v(-143.78, 207.54) * mm, v(-147.7, 209.04) * mm]});
            skFitSpline(sketch, "E1579", {"points": [v(-147.7, 209.04) * mm, v(-149.9, 209.89) * mm, v(-159.31, 201.6) * mm, v(-159.31, 198.8) * mm]});
            skFitSpline(sketch, "E1580", {"points": [v(-159.31, 198.8) * mm, v(-159.31, 197.55) * mm, v(-159.85, 196.2) * mm, v(-160.5, 195.8) * mm]});
            skFitSpline(sketch, "E1581", {"points": [v(-160.5, 195.8) * mm, v(-161.15, 195.4) * mm, v(-161.6, 193.08) * mm, v(-161.51, 190.66) * mm]});
            skFitSpline(sketch, "E1582", {"points": [v(-161.51, 190.66) * mm, v(-161.4, 187.6) * mm, v(-162.07, 185.72) * mm, v(-163.7, 184.5) * mm]});
            skFitSpline(sketch, "E1583", {"points": [v(-163.7, 184.5) * mm, v(-168.41, 180.98) * mm, v(-170.02, 180.5) * mm, v(-171.4, 182.16) * mm]});
            skFitSpline(sketch, "E1584", {"points": [v(-234.19, 189.4) * mm, v(-236.72, 190.67) * mm, v(-240.57, 191.8) * mm, v(-242.74, 191.92) * mm]});
            skFitSpline(sketch, "E1585", {"points": [v(-242.74, 191.92) * mm, v(-245.15, 192.05) * mm, v(-246.59, 192.73) * mm, v(-246.4, 193.65) * mm]});
            skFitSpline(sketch, "E1586", {"points": [v(-246.4, 193.65) * mm, v(-246.23, 194.48) * mm, v(-246.9, 195.16) * mm, v(-247.87, 195.16) * mm]});
            skFitSpline(sketch, "E1587", {"points": [v(-247.87, 195.16) * mm, v(-248.84, 195.16) * mm, v(-250.08, 195.9) * mm, v(-250.62, 196.79) * mm]});
            skFitSpline(sketch, "E1588", {"points": [v(-250.62, 196.79) * mm, v(-252.19, 199.4) * mm, v(-259.09, 202.3) * mm, v(-260.94, 201.13) * mm]});
            skFitSpline(sketch, "E1589", {"points": [v(-260.94, 201.13) * mm, v(-263.6, 199.45) * mm, v(-268.1, 199.89) * mm, v(-268.88, 201.9) * mm]});
            skFitSpline(sketch, "E1590", {"points": [v(-268.88, 201.9) * mm, v(-270.06, 204.96) * mm, v(-266.92, 207.38) * mm, v(-261.76, 207.38) * mm]});
            skFitSpline(sketch, "E1591", {"points": [v(-261.76, 207.38) * mm, v(-259.11, 207.38) * mm, v(-257.26, 207.89) * mm, v(-257.64, 208.5) * mm]});
            skFitSpline(sketch, "E1592", {"points": [v(-257.64, 208.5) * mm, v(-258.03, 209.12) * mm, v(-256.9, 210.76) * mm, v(-255.13, 212.15) * mm]});
            skFitSpline(sketch, "E1593", {"points": [v(-255.13, 212.15) * mm, v(-252.6, 214.15) * mm, v(-252.1, 215.33) * mm, v(-252.73, 217.86) * mm]});
            skFitSpline(sketch, "E1594", {"points": [v(-252.73, 217.86) * mm, v(-253.34, 220.3) * mm, v(-253.9, 220.73) * mm, v(-255.12, 219.72) * mm]});
            skFitSpline(sketch, "E1595", {"points": [v(-255.12, 219.72) * mm, v(-257.23, 217.97) * mm, v(-258.67, 219.53) * mm, v(-256.9, 221.66) * mm]});
            skFitSpline(sketch, "E1596", {"points": [v(-256.9, 221.66) * mm, v(-255.32, 223.57) * mm, v(-256.15, 224.8) * mm, v(-259.23, 225.1) * mm]});
            skFitSpline(sketch, "E1597", {"points": [v(-259.23, 225.1) * mm, v(-260.4, 225.22) * mm, v(-263.57, 226.3) * mm, v(-266.26, 227.51) * mm]});
            skFitSpline(sketch, "E1598", {"points": [v(-266.26, 227.51) * mm, v(-269.66, 229.05) * mm, v(-274.88, 229.83) * mm, v(-283.37, 230.09) * mm]});
            skFitSpline(sketch, "E1599", {"points": [v(-283.37, 230.09) * mm, v(-290.1, 230.29) * mm, v(-296.51, 230.49) * mm, v(-297.63, 230.53) * mm]});
            skFitSpline(sketch, "E1600", {"points": [v(-297.63, 230.53) * mm, v(-300.05, 230.62) * mm, v(-304.76, 237.77) * mm, v(-304.76, 241.33) * mm]});
            skFitSpline(sketch, "E1601", {"points": [v(-304.76, 241.33) * mm, v(-304.76, 246.95) * mm, v(-292.33, 253.01) * mm, v(-290.52, 248.28) * mm]});
            skFitSpline(sketch, "E1602", {"points": [v(-290.52, 248.28) * mm, v(-289.87, 246.6) * mm, v(-289.51, 246.6) * mm, v(-286.93, 248.28) * mm]});
            skFitSpline(sketch, "E1603", {"points": [v(-286.93, 248.28) * mm, v(-285.36, 249.31) * mm, v(-282.63, 250.16) * mm, v(-280.88, 250.16) * mm]});
            skFitSpline(sketch, "E1604", {"points": [v(-280.88, 250.16) * mm, v(-278.01, 250.16) * mm, v(-277.73, 249.75) * mm, v(-278.07, 246.19) * mm]});
            skFitSpline(sketch, "E1605", {"points": [v(-278.07, 246.19) * mm, v(-278.38, 243.04) * mm, v(-278.04, 242.28) * mm, v(-276.43, 242.55) * mm]});
            skFitSpline(sketch, "E1606", {"points": [v(-276.43, 242.55) * mm, v(-275.3, 242.74) * mm, v(-274.04, 242.33) * mm, v(-273.61, 241.64) * mm]});
            skFitSpline(sketch, "E1607", {"points": [v(-273.61, 241.64) * mm, v(-272.55, 239.9) * mm, v(-269.24, 240.05) * mm, v(-269.62, 241.8) * mm]});
            skFitSpline(sketch, "E1608", {"points": [v(-269.62, 241.8) * mm, v(-269.79, 242.59) * mm, v(-268.11, 243.63) * mm, v(-265.9, 244.1) * mm]});
            skFitSpline(sketch, "E1609", {"points": [v(-265.9, 244.1) * mm, v(-262.44, 244.86) * mm, v(-261.17, 244.4) * mm, v(-256.89, 240.82) * mm]});
            skFitSpline(sketch, "E1610", {"points": [v(-256.89, 240.82) * mm, v(-253.01, 237.58) * mm, v(-251.54, 236.97) * mm, v(-250.24, 238.05) * mm]});
            skFitSpline(sketch, "E1611", {"points": [v(-250.24, 238.05) * mm, v(-249.32, 238.8) * mm, v(-247.6, 239.06) * mm, v(-246.41, 238.6) * mm]});
            skFitSpline(sketch, "E1612", {"points": [v(-246.41, 238.6) * mm, v(-244.4, 237.82) * mm, v(-244.43, 237.63) * mm, v(-246.7, 235.92) * mm]});
            skFitSpline(sketch, "E1613", {"points": [v(-246.7, 235.92) * mm, v(-249.15, 234.07) * mm, v(-249.15, 234.07) * mm, v(-246.7, 234.35) * mm]});
            skFitSpline(sketch, "E1614", {"points": [v(-246.7, 234.35) * mm, v(-240.82, 235.03) * mm, v(-231.17, 227.9) * mm, v(-235.65, 226.18) * mm]});
            skFitSpline(sketch, "E1615", {"points": [v(-235.65, 226.18) * mm, v(-238.49, 225.09) * mm, v(-236.32, 222.05) * mm, v(-232.7, 222.05) * mm]});
            skFitSpline(sketch, "E1616", {"points": [v(-232.7, 222.05) * mm, v(-230.87, 222.05) * mm, v(-228.35, 220.93) * mm, v(-227.1, 219.56) * mm]});
            skFitSpline(sketch, "E1617", {"points": [v(-227.1, 219.56) * mm, v(-225.87, 218.2) * mm, v(-224.2, 217.33) * mm, v(-223.38, 217.64) * mm]});
            skFitSpline(sketch, "E1618", {"points": [v(-223.38, 217.64) * mm, v(-222.57, 217.95) * mm, v(-220.63, 216.85) * mm, v(-219.08, 215.19) * mm]});
            skFitSpline(sketch, "E1619", {"points": [v(-219.08, 215.19) * mm, v(-218.13, 214.18) * mm, v(-217.19, 213.18) * mm, v(-216.24, 212.18) * mm]});
            skFitSpline(sketch, "E1620", {"points": [v(-216.24, 212.18) * mm, v(-217.14, 211.94) * mm, v(-218.04, 211.7) * mm, v(-218.93, 211.47) * mm]});
            skFitSpline(sketch, "E1621", {"points": [v(-218.93, 211.47) * mm, v(-220.41, 211.09) * mm, v(-221.37, 210.36) * mm, v(-221.05, 209.85) * mm]});
            skFitSpline(sketch, "E1622", {"points": [v(-221.05, 209.85) * mm, v(-220.74, 209.34) * mm, v(-221.55, 207.97) * mm, v(-222.85, 206.79) * mm]});
            skFitSpline(sketch, "E1623", {"points": [v(-222.85, 206.79) * mm, v(-225.12, 204.73) * mm, v(-225.36, 204.8) * mm, v(-229.03, 208.46) * mm]});
            skFitSpline(sketch, "E1624", {"points": [v(-229.03, 208.46) * mm, v(-233.2, 212.63) * mm, v(-233.62, 212.78) * mm, v(-236.32, 211.06) * mm]});
            skFitSpline(sketch, "E1625", {"points": [v(-236.32, 211.06) * mm, v(-237.82, 210.1) * mm, v(-237.14, 208.93) * mm, v(-232.54, 204.5) * mm]});
            skFitSpline(sketch, "E1626", {"points": [v(-232.54, 204.5) * mm, v(-226.63, 198.82) * mm, v(-225.28, 193.73) * mm, v(-229.48, 192.91) * mm]});
            skFitSpline(sketch, "E1627", {"points": [v(-229.48, 192.91) * mm, v(-231.46, 192.53) * mm, v(-231.47, 192.34) * mm, v(-229.6, 190.28) * mm]});
            skFitSpline(sketch, "E1628", {"points": [v(-229.6, 190.28) * mm, v(-226.74, 187.11) * mm, v(-228.84, 186.7) * mm, v(-234.19, 189.4) * mm]});
            skFitSpline(sketch, "E1629", {"points": [v(-97.6, 198.73) * mm, v(-98.94, 199.25) * mm, v(-99.76, 200.17) * mm, v(-99.42, 200.77) * mm]});
            skFitSpline(sketch, "E1630", {"points": [v(-99.42, 200.77) * mm, v(-99.09, 201.37) * mm, v(-100.43, 202.14) * mm, v(-102.41, 202.48) * mm]});
            skFitSpline(sketch, "E1631", {"points": [v(-102.41, 202.48) * mm, v(-107.09, 203.29) * mm, v(-107.16, 205.43) * mm, v(-102.54, 205.96) * mm]});
            skFitSpline(sketch, "E1632", {"points": [v(-102.54, 205.96) * mm, v(-98.52, 206.41) * mm, v(-93.59, 209.38) * mm, v(-94.54, 210.76) * mm]});
            skFitSpline(sketch, "E1633", {"points": [v(-94.54, 210.76) * mm, v(-94.87, 211.26) * mm, v(-94.03, 211.71) * mm, v(-92.67, 211.78) * mm]});
            skFitSpline(sketch, "E1634", {"points": [v(-92.67, 211.78) * mm, v(-91.31, 211.85) * mm, v(-87.6, 212.3) * mm, v(-84.41, 212.78) * mm]});
            skFitSpline(sketch, "E1635", {"points": [v(-84.41, 212.78) * mm, v(-79.47, 213.52) * mm, v(-78.5, 213.32) * mm, v(-77.8, 211.43) * mm]});
            skFitSpline(sketch, "E1636", {"points": [v(-77.8, 211.43) * mm, v(-77.34, 210.2) * mm, v(-76.22, 208.66) * mm, v(-75.32, 207.98) * mm]});
            skFitSpline(sketch, "E1637", {"points": [v(-75.32, 207.98) * mm, v(-72.8, 206.08) * mm, v(-75.65, 203.36) * mm, v(-83.4, 200.25) * mm]});
            skFitSpline(sketch, "E1638", {"points": [v(-83.4, 200.25) * mm, v(-90.27, 197.48) * mm, v(-93.5, 197.13) * mm, v(-97.6, 198.73) * mm]});
            skFitSpline(sketch, "E1639", {"points": [v(-106.14, 208.6) * mm, v(-107.16, 210.25) * mm, v(-101.31, 212.79) * mm, v(-98.75, 211.8) * mm]});
            skFitSpline(sketch, "E1640", {"points": [v(-98.75, 211.8) * mm, v(-97.1, 211.17) * mm, v(-96.99, 210.68) * mm, v(-98.21, 209.2) * mm]});
            skFitSpline(sketch, "E1641", {"points": [v(-98.21, 209.2) * mm, v(-99.92, 207.14) * mm, v(-105, 206.75) * mm, v(-106.14, 208.6) * mm]});
            skFitSpline(sketch, "E1642", {"points": [v(-266.25, 217.14) * mm, v(-266.7, 217.88) * mm, v(-266.46, 219.24) * mm, v(-265.7, 220.16) * mm]});
            skFitSpline(sketch, "E1643", {"points": [v(-265.7, 220.16) * mm, v(-264.73, 221.33) * mm, v(-264.7, 222.07) * mm, v(-265.6, 222.63) * mm]});
            skFitSpline(sketch, "E1644", {"points": [v(-265.6, 222.63) * mm, v(-266.33, 223.08) * mm, v(-266.59, 223.96) * mm, v(-266.2, 224.6) * mm]});
            skFitSpline(sketch, "E1645", {"points": [v(-266.2, 224.6) * mm, v(-265.8, 225.23) * mm, v(-264.96, 225.43) * mm, v(-264.32, 225.04) * mm]});
            skFitSpline(sketch, "E1646", {"points": [v(-264.32, 225.04) * mm, v(-263.69, 224.64) * mm, v(-263.44, 223.87) * mm, v(-263.78, 223.32) * mm]});
            skFitSpline(sketch, "E1647", {"points": [v(-263.78, 223.32) * mm, v(-264.12, 222.77) * mm, v(-263.26, 222.03) * mm, v(-261.86, 221.66) * mm]});
            skFitSpline(sketch, "E1648", {"points": [v(-261.86, 221.66) * mm, v(-260.22, 221.23) * mm, v(-259.48, 220.2) * mm, v(-259.75, 218.77) * mm]});
            skFitSpline(sketch, "E1649", {"points": [v(-259.75, 218.77) * mm, v(-260.23, 216.27) * mm, v(-264.97, 215.08) * mm, v(-266.25, 217.14) * mm]});
            skFitSpline(sketch, "E1650", {"points": [v(124.25, 233.96) * mm, v(124.25, 235.2) * mm, v(125.02, 236.05) * mm, v(125.89, 235.76) * mm]});
            skFitSpline(sketch, "E1651", {"points": [v(125.89, 235.76) * mm, v(126.46, 235.57) * mm, v(126.69, 236.12) * mm, v(126.4, 236.98) * mm]});
            skFitSpline(sketch, "E1652", {"points": [v(126.4, 236.98) * mm, v(126.11, 237.84) * mm, v(125.1, 238.54) * mm, v(124.15, 238.54) * mm]});
            skFitSpline(sketch, "E1653", {"points": [v(124.15, 238.54) * mm, v(123.2, 238.55) * mm, v(122.33, 239.1) * mm, v(122.23, 239.77) * mm]});
            skFitSpline(sketch, "E1654", {"points": [v(122.23, 239.77) * mm, v(121.96, 241.65) * mm, v(125.38, 247.71) * mm, v(126.72, 247.71) * mm]});
            skFitSpline(sketch, "E1655", {"points": [v(126.72, 247.71) * mm, v(127.38, 247.71) * mm, v(127.78, 248.2) * mm, v(127.6, 248.79) * mm]});
            skFitSpline(sketch, "E1656", {"points": [v(127.6, 248.79) * mm, v(127.44, 249.38) * mm, v(128.81, 251.27) * mm, v(130.65, 253) * mm]});
            skFitSpline(sketch, "E1657", {"points": [v(130.65, 253) * mm, v(132.56, 254.79) * mm, v(133.48, 256.46) * mm, v(132.77, 256.9) * mm]});
            skFitSpline(sketch, "E1658", {"points": [v(132.77, 256.9) * mm, v(130.67, 258.2) * mm, v(132.77, 259.94) * mm, v(136.44, 259.94) * mm]});
            skFitSpline(sketch, "E1659", {"points": [v(136.44, 259.94) * mm, v(138.36, 259.94) * mm, v(142.32, 260.96) * mm, v(145.24, 262.21) * mm]});
            skFitSpline(sketch, "E1660", {"points": [v(145.24, 262.21) * mm, v(148.3, 263.52) * mm, v(152.17, 264.25) * mm, v(154.37, 263.93) * mm]});
            skFitSpline(sketch, "E1661", {"points": [v(154.37, 263.93) * mm, v(156.7, 263.59) * mm, v(160.48, 264.38) * mm, v(164.06, 265.96) * mm]});
            skFitSpline(sketch, "E1662", {"points": [v(164.06, 265.96) * mm, v(169.15, 268.21) * mm, v(170.16, 268.33) * mm, v(171.67, 266.81) * mm]});
            skFitSpline(sketch, "E1663", {"points": [v(171.67, 266.81) * mm, v(173.19, 265.3) * mm, v(173.07, 264.88) * mm, v(170.8, 263.66) * mm]});
            skFitSpline(sketch, "E1664", {"points": [v(170.8, 263.66) * mm, v(167.14, 261.7) * mm, v(153.7, 257.5) * mm, v(151.12, 257.5) * mm]});
            skFitSpline(sketch, "E1665", {"points": [v(151.12, 257.5) * mm, v(147.51, 257.5) * mm, v(142.71, 254.39) * mm, v(137.65, 248.78) * mm]});
            skFitSpline(sketch, "E1666", {"points": [v(137.65, 248.78) * mm, v(131.6, 242.06) * mm, v(131.36, 238.36) * mm, v(136.85, 236.33) * mm]});
            skFitSpline(sketch, "E1667", {"points": [v(136.85, 236.33) * mm, v(140.95, 234.81) * mm, v(137.72, 233.23) * mm, v(130.95, 233.44) * mm]});
            skFitSpline(sketch, "E1668", {"points": [v(130.95, 233.44) * mm, v(127.26, 233.55) * mm, v(124.25, 233.79) * mm, v(124.25, 233.96) * mm]});
            skFitSpline(sketch, "E1669", {"points": [v(498.96, 234.12) * mm, v(497.08, 237.15) * mm, v(507.97, 240.34) * mm, v(510.36, 237.46) * mm]});
            skFitSpline(sketch, "E1670", {"points": [v(510.36, 237.46) * mm, v(511.57, 236) * mm, v(511.43, 235.45) * mm, v(509.64, 234.57) * mm]});
            skFitSpline(sketch, "E1671", {"points": [v(509.64, 234.57) * mm, v(506.6, 233.06) * mm, v(499.79, 232.78) * mm, v(498.96, 234.12) * mm]});
            skFitSpline(sketch, "E1672", {"points": [v(-335.1, 240.67) * mm, v(-338.61, 243.27) * mm, v(-341.17, 245.92) * mm, v(-340.77, 246.56) * mm]});
            skFitSpline(sketch, "E1673", {"points": [v(-340.77, 246.56) * mm, v(-340.33, 247.29) * mm, v(-339.2, 247.26) * mm, v(-337.77, 246.5) * mm]});
            skFitSpline(sketch, "E1674", {"points": [v(-337.77, 246.5) * mm, v(-334.5, 244.75) * mm, v(-333.55, 244.98) * mm, v(-335.3, 247.08) * mm]});
            skFitSpline(sketch, "E1675", {"points": [v(-335.3, 247.08) * mm, v(-336.55, 248.6) * mm, v(-336.22, 249.1) * mm, v(-333.31, 250.14) * mm]});
            skFitSpline(sketch, "E1676", {"points": [v(-333.31, 250.14) * mm, v(-331.39, 250.82) * mm, v(-328.87, 251.93) * mm, v(-327.71, 252.6) * mm]});
            skFitSpline(sketch, "E1677", {"points": [v(-327.71, 252.6) * mm, v(-325.1, 254.1) * mm, v(-322.36, 250.16) * mm, v(-324.51, 248) * mm]});
            skFitSpline(sketch, "E1678", {"points": [v(-324.51, 248) * mm, v(-325.43, 247.09) * mm, v(-325.1, 246.09) * mm, v(-323.34, 244.59) * mm]});
            skFitSpline(sketch, "E1679", {"points": [v(-323.34, 244.59) * mm, v(-320.34, 242.02) * mm, v(-321, 239.77) * mm, v(-325.4, 237.57) * mm]});
            skFitSpline(sketch, "E1680", {"points": [v(-325.4, 237.57) * mm, v(-328.49, 236.04) * mm, v(-329.12, 236.24) * mm, v(-335.1, 240.67) * mm]});
            skFitSpline(sketch, "E1681", {"points": [v(-275.4, 245.84) * mm, v(-277.45, 248.32) * mm, v(-276.1, 251.38) * mm, v(-272.96, 251.38) * mm]});
            skFitSpline(sketch, "E1682", {"points": [v(-272.96, 251.38) * mm, v(-269.46, 251.38) * mm, v(-262.68, 247.73) * mm, v(-263.98, 246.54) * mm]});
            skFitSpline(sketch, "E1683", {"points": [v(-263.98, 246.54) * mm, v(-266.29, 244.42) * mm, v(-273.83, 243.96) * mm, v(-275.4, 245.84) * mm]});
            skFitSpline(sketch, "E1684", {"points": [v(-376.03, 253.38) * mm, v(-377.33, 254.7) * mm, v(-375.66, 256.26) * mm, v(-372.83, 256.4) * mm]});
            skFitSpline(sketch, "E1685", {"points": [v(-372.83, 256.4) * mm, v(-370.35, 256.5) * mm, v(-370.38, 256.58) * mm, v(-373.2, 257.42) * mm]});
            skFitSpline(sketch, "E1686", {"points": [v(-373.2, 257.42) * mm, v(-374.89, 257.92) * mm, v(-376.94, 257.8) * mm, v(-377.77, 257.16) * mm]});
            skFitSpline(sketch, "E1687", {"points": [v(-377.77, 257.16) * mm, v(-380.3, 255.22) * mm, v(-382.63, 257.03) * mm, v(-382.4, 260.74) * mm]});
            skFitSpline(sketch, "E1688", {"points": [v(-382.4, 260.74) * mm, v(-382.2, 264.04) * mm, v(-381.93, 264.2) * mm, v(-376.93, 263.87) * mm]});
            skFitSpline(sketch, "E1689", {"points": [v(-376.93, 263.87) * mm, v(-374.04, 263.68) * mm, v(-370.52, 262.72) * mm, v(-369.11, 261.73) * mm]});
            skFitSpline(sketch, "E1690", {"points": [v(-369.11, 261.73) * mm, v(-367.7, 260.74) * mm, v(-365.38, 259.94) * mm, v(-363.94, 259.94) * mm]});
            skFitSpline(sketch, "E1691", {"points": [v(-363.94, 259.94) * mm, v(-361.88, 259.94) * mm, v(-361.36, 260.64) * mm, v(-361.46, 263.3) * mm]});
            skFitSpline(sketch, "E1692", {"points": [v(-361.46, 263.3) * mm, v(-361.62, 267.37) * mm, v(-358.6, 267.88) * mm, v(-356.72, 264.1) * mm]});
            skFitSpline(sketch, "E1693", {"points": [v(-356.72, 264.1) * mm, v(-356.02, 262.7) * mm, v(-354.5, 261.68) * mm, v(-353.33, 261.85) * mm]});
            skFitSpline(sketch, "E1694", {"points": [v(-353.33, 261.85) * mm, v(-352.17, 262.02) * mm, v(-350.9, 261.64) * mm, v(-350.5, 261) * mm]});
            skFitSpline(sketch, "E1695", {"points": [v(-350.5, 261) * mm, v(-349.28, 259.03) * mm, v(-352.54, 256.27) * mm, v(-356.1, 256.27) * mm]});
            skFitSpline(sketch, "E1696", {"points": [v(-356.1, 256.27) * mm, v(-357.95, 256.27) * mm, v(-361.44, 255.45) * mm, v(-363.85, 254.44) * mm]});
            skFitSpline(sketch, "E1697", {"points": [v(-363.85, 254.44) * mm, v(-368.37, 252.55) * mm, v(-374.65, 252) * mm, v(-376.03, 253.38) * mm]});
            skFitSpline(sketch, "E1698", {"points": [v(-299.07, 253.43) * mm, v(-299.62, 253.98) * mm, v(-301.27, 254.56) * mm, v(-302.72, 254.7) * mm]});
            skFitSpline(sketch, "E1699", {"points": [v(-302.72, 254.7) * mm, v(-310.83, 255.53) * mm, v(-311.48, 255.84) * mm, v(-311.87, 259.11) * mm]});
            skFitSpline(sketch, "E1700", {"points": [v(-311.87, 259.11) * mm, v(-312.21, 262.02) * mm, v(-312.78, 262.38) * mm, v(-316.92, 262.38) * mm]});
            skFitSpline(sketch, "E1701", {"points": [v(-316.92, 262.38) * mm, v(-321.65, 262.38) * mm, v(-325.18, 264.88) * mm, v(-323.74, 267.22) * mm]});
            skFitSpline(sketch, "E1702", {"points": [v(-323.74, 267.22) * mm, v(-323.3, 267.92) * mm, v(-321.85, 268.5) * mm, v(-320.5, 268.5) * mm]});
            skFitSpline(sketch, "E1703", {"points": [v(-320.5, 268.5) * mm, v(-319.16, 268.5) * mm, v(-318.38, 269) * mm, v(-318.76, 269.63) * mm]});
            skFitSpline(sketch, "E1704", {"points": [v(-318.76, 269.63) * mm, v(-319.83, 271.35) * mm, v(-316.96, 272.63) * mm, v(-315.45, 271.11) * mm]});
            skFitSpline(sketch, "E1705", {"points": [v(-315.45, 271.11) * mm, v(-314.5, 270.17) * mm, v(-314.74, 269.56) * mm, v(-316.27, 268.97) * mm]});
            skFitSpline(sketch, "E1706", {"points": [v(-316.27, 268.97) * mm, v(-319.33, 267.8) * mm, v(-316.3, 266.1) * mm, v(-311.14, 266.07) * mm]});
            skFitSpline(sketch, "E1707", {"points": [v(-311.14, 266.07) * mm, v(-308.45, 266.05) * mm, v(-306.86, 265.34) * mm, v(-306.33, 263.9) * mm]});
            skFitSpline(sketch, "E1708", {"points": [v(-306.33, 263.9) * mm, v(-304.76, 259.73) * mm, v(-302.17, 258.99) * mm, v(-291.38, 259.62) * mm]});
            skFitSpline(sketch, "E1709", {"points": [v(-291.38, 259.62) * mm, v(-285.63, 259.96) * mm, v(-279.55, 260.22) * mm, v(-277.87, 260.2) * mm]});
            skFitSpline(sketch, "E1710", {"points": [v(-277.87, 260.2) * mm, v(-276.2, 260.17) * mm, v(-274.18, 260.68) * mm, v(-273.4, 261.33) * mm]});
            skFitSpline(sketch, "E1711", {"points": [v(-273.4, 261.33) * mm, v(-272.49, 262.08) * mm, v(-271.71, 262.07) * mm, v(-271.24, 261.3) * mm]});
            skFitSpline(sketch, "E1712", {"points": [v(-271.24, 261.3) * mm, v(-270.83, 260.64) * mm, v(-271.1, 259.74) * mm, v(-271.82, 259.29) * mm]});
            skFitSpline(sketch, "E1713", {"points": [v(-271.82, 259.29) * mm, v(-272.55, 258.84) * mm, v(-272.86, 257.71) * mm, v(-272.5, 256.8) * mm]});
            skFitSpline(sketch, "E1714", {"points": [v(-272.5, 256.8) * mm, v(-272.16, 255.88) * mm, v(-272.26, 254.9) * mm, v(-272.73, 254.6) * mm]});
            skFitSpline(sketch, "E1715", {"points": [v(-272.73, 254.6) * mm, v(-274.53, 253.52) * mm, v(-298.1, 252.47) * mm, v(-299.07, 253.43) * mm]});
            skFitSpline(sketch, "E1716", {"points": [v(378.72, 256.51) * mm, v(376.68, 258.55) * mm, v(376.88, 261.78) * mm, v(379.16, 263.67) * mm]});
            skFitSpline(sketch, "E1717", {"points": [v(379.16, 263.67) * mm, v(380.75, 264.99) * mm, v(381.68, 264.9) * mm, v(384.58, 263.19) * mm]});
            skFitSpline(sketch, "E1718", {"points": [v(384.58, 263.19) * mm, v(386.5, 262.05) * mm, v(388.37, 261.59) * mm, v(388.72, 262.16) * mm]});
            skFitSpline(sketch, "E1719", {"points": [v(388.72, 262.16) * mm, v(389.83, 263.95) * mm, v(398.87, 263.7) * mm, v(400.41, 261.84) * mm]});
            skFitSpline(sketch, "E1720", {"points": [v(400.41, 261.84) * mm, v(401.56, 260.46) * mm, v(401.32, 259.82) * mm, v(399.23, 258.7) * mm]});
            skFitSpline(sketch, "E1721", {"points": [v(399.23, 258.7) * mm, v(397.1, 257.56) * mm, v(396.16, 257.7) * mm, v(394.26, 259.42) * mm]});
            skFitSpline(sketch, "E1722", {"points": [v(394.26, 259.42) * mm, v(391.83, 261.62) * mm, v(390.9, 260.22) * mm, v(393.25, 257.88) * mm]});
            skFitSpline(sketch, "E1723", {"points": [v(393.25, 257.88) * mm, v(395.26, 255.86) * mm, v(392.65, 254.83) * mm, v(389, 256.21) * mm]});
            skFitSpline(sketch, "E1724", {"points": [v(389, 256.21) * mm, v(387.02, 256.97) * mm, v(385.63, 256.98) * mm, v(385.17, 256.22) * mm]});
            skFitSpline(sketch, "E1725", {"points": [v(385.17, 256.22) * mm, v(384.16, 254.59) * mm, v(378.72, 254.02) * mm, v(378.72, 256.51) * mm]});
            skFitSpline(sketch, "E1726", {"points": [v(-337.78, 260.15) * mm, v(-341.24, 263.94) * mm, v(-341.34, 264.31) * mm, v(-339.32, 265.8) * mm]});
            skFitSpline(sketch, "E1727", {"points": [v(-339.32, 265.8) * mm, v(-334.99, 268.96) * mm, v(-327.63, 265.15) * mm, v(-328.23, 260.04) * mm]});
            skFitSpline(sketch, "E1728", {"points": [v(-328.23, 260.04) * mm, v(-328.8, 255.16) * mm, v(-333.26, 255.2) * mm, v(-337.78, 260.15) * mm]});
            skFitSpline(sketch, "E1729", {"points": [v(405.97, 257.96) * mm, v(403.95, 259.45) * mm, v(403.85, 259.88) * mm, v(405.36, 260.45) * mm]});
            skFitSpline(sketch, "E1730", {"points": [v(405.36, 260.45) * mm, v(407.69, 261.33) * mm, v(413.77, 259.72) * mm, v(414.2, 258.1) * mm]});
            skFitSpline(sketch, "E1731", {"points": [v(414.2, 258.1) * mm, v(414.73, 256.12) * mm, v(408.62, 256.01) * mm, v(405.97, 257.96) * mm]});
            skFitSpline(sketch, "E1732", {"points": [v(-394.46, 259.72) * mm, v(-394.91, 260.45) * mm, v(-396.07, 260.75) * mm, v(-397.02, 260.39) * mm]});
            skFitSpline(sketch, "E1733", {"points": [v(-397.02, 260.39) * mm, v(-397.98, 260.02) * mm, v(-399.36, 260.1) * mm, v(-400.1, 260.56) * mm]});
            skFitSpline(sketch, "E1734", {"points": [v(-400.1, 260.56) * mm, v(-402.16, 261.83) * mm, v(-392.7, 269.6) * mm, v(-389.03, 269.66) * mm]});
            skFitSpline(sketch, "E1735", {"points": [v(-389.03, 269.66) * mm, v(-387.32, 269.7) * mm, v(-385.26, 270.37) * mm, v(-384.45, 271.18) * mm]});
            skFitSpline(sketch, "E1736", {"points": [v(-384.45, 271.18) * mm, v(-383.45, 272.19) * mm, v(-382.59, 272.25) * mm, v(-381.73, 271.4) * mm]});
            skFitSpline(sketch, "E1737", {"points": [v(-381.73, 271.4) * mm, v(-380.87, 270.53) * mm, v(-381.29, 269.1) * mm, v(-383.07, 266.82) * mm]});
            skFitSpline(sketch, "E1738", {"points": [v(-383.07, 266.82) * mm, v(-385.14, 264.2) * mm, v(-386.03, 263.8) * mm, v(-387.39, 264.93) * mm]});
            skFitSpline(sketch, "E1739", {"points": [v(-387.39, 264.93) * mm, v(-388.33, 265.7) * mm, v(-389.1, 265.87) * mm, v(-389.12, 265.28) * mm]});
            skFitSpline(sketch, "E1740", {"points": [v(-389.12, 265.28) * mm, v(-389.18, 263.04) * mm, v(-393.64, 258.4) * mm, v(-394.46, 259.72) * mm]});
            skFitSpline(sketch, "E1741", {"points": [v(-278.08, 263) * mm, v(-278.42, 263.34) * mm, v(-283.52, 263.83) * mm, v(-289.4, 264.1) * mm]});
            skFitSpline(sketch, "E1742", {"points": [v(-289.4, 264.1) * mm, v(-300.75, 264.6) * mm, v(-304.55, 266.23) * mm, v(-300.8, 269) * mm]});
            skFitSpline(sketch, "E1743", {"points": [v(-300.8, 269) * mm, v(-299.64, 269.86) * mm, v(-299, 270.89) * mm, v(-299.4, 271.28) * mm]});
            skFitSpline(sketch, "E1744", {"points": [v(-299.4, 271.28) * mm, v(-299.79, 271.67) * mm, v(-298.98, 272.7) * mm, v(-297.6, 273.55) * mm]});
            skFitSpline(sketch, "E1745", {"points": [v(-297.6, 273.55) * mm, v(-295.71, 274.74) * mm, v(-295.43, 275.5) * mm, v(-296.45, 276.73) * mm]});
            skFitSpline(sketch, "E1746", {"points": [v(-296.45, 276.73) * mm, v(-297.54, 278.05) * mm, v(-298.3, 277.87) * mm, v(-300.53, 275.78) * mm]});
            skFitSpline(sketch, "E1747", {"points": [v(-300.53, 275.78) * mm, v(-302.54, 273.9) * mm, v(-304.5, 273.32) * mm, v(-307.98, 273.6) * mm]});
            skFitSpline(sketch, "E1748", {"points": [v(-307.98, 273.6) * mm, v(-310.58, 273.82) * mm, v(-312.65, 274.54) * mm, v(-312.58, 275.22) * mm]});
            skFitSpline(sketch, "E1749", {"points": [v(-312.58, 275.22) * mm, v(-312.52, 275.89) * mm, v(-313.34, 277.09) * mm, v(-314.42, 277.88) * mm]});
            skFitSpline(sketch, "E1750", {"points": [v(-314.42, 277.88) * mm, v(-316.12, 279.13) * mm, v(-316.14, 279.4) * mm, v(-314.54, 279.92) * mm]});
            skFitSpline(sketch, "E1751", {"points": [v(-314.54, 279.92) * mm, v(-313.53, 280.25) * mm, v(-311.88, 280.8) * mm, v(-310.87, 281.13) * mm]});
            skFitSpline(sketch, "E1752", {"points": [v(-310.87, 281.13) * mm, v(-309.86, 281.47) * mm, v(-310.57, 281.79) * mm, v(-312.44, 281.84) * mm]});
            skFitSpline(sketch, "E1753", {"points": [v(-312.44, 281.84) * mm, v(-314.32, 281.9) * mm, v(-317.18, 282.81) * mm, v(-318.81, 283.88) * mm]});
            skFitSpline(sketch, "E1754", {"points": [v(-318.81, 283.88) * mm, v(-321.6, 285.7) * mm, v(-321.67, 286) * mm, v(-319.9, 288.7) * mm]});
            skFitSpline(sketch, "E1755", {"points": [v(-319.9, 288.7) * mm, v(-318.79, 290.4) * mm, v(-317.3, 291.29) * mm, v(-316.23, 290.88) * mm]});
            skFitSpline(sketch, "E1756", {"points": [v(-316.23, 290.88) * mm, v(-315.2, 290.48) * mm, v(-314.59, 290.82) * mm, v(-314.8, 291.68) * mm]});
            skFitSpline(sketch, "E1757", {"points": [v(-314.8, 291.68) * mm, v(-315, 292.5) * mm, v(-314.26, 293.75) * mm, v(-313.18, 294.47) * mm]});
            skFitSpline(sketch, "E1758", {"points": [v(-313.18, 294.47) * mm, v(-311.27, 295.73) * mm, v(-309.86, 295.45) * mm, v(-305.98, 293.03) * mm]});
            skFitSpline(sketch, "E1759", {"points": [v(-305.98, 293.03) * mm, v(-303.83, 291.7) * mm, v(-299.78, 290.14) * mm, v(-298.04, 289.98) * mm]});
            skFitSpline(sketch, "E1760", {"points": [v(-298.04, 289.98) * mm, v(-297.37, 289.92) * mm, v(-296.81, 288.87) * mm, v(-296.8, 287.65) * mm]});
            skFitSpline(sketch, "E1761", {"points": [v(-296.8, 287.65) * mm, v(-296.8, 286.42) * mm, v(-295.86, 284.9) * mm, v(-294.72, 284.26) * mm]});
            skFitSpline(sketch, "E1762", {"points": [v(-294.72, 284.26) * mm, v(-293.58, 283.62) * mm, v(-292.92, 282.36) * mm, v(-293.27, 281.46) * mm]});
            skFitSpline(sketch, "E1763", {"points": [v(-293.27, 281.46) * mm, v(-294.12, 279.24) * mm, v(-281.79, 277.5) * mm, v(-279.83, 279.56) * mm]});
            skFitSpline(sketch, "E1764", {"points": [v(-279.83, 279.56) * mm, v(-278.82, 280.64) * mm, v(-279.15, 280.79) * mm, v(-281.16, 280.18) * mm]});
            skFitSpline(sketch, "E1765", {"points": [v(-281.16, 280.18) * mm, v(-283.88, 279.36) * mm, v(-293.76, 284.46) * mm, v(-293.76, 286.7) * mm]});
            skFitSpline(sketch, "E1766", {"points": [v(-293.76, 286.7) * mm, v(-293.76, 289.32) * mm, v(-289.88, 290.95) * mm, v(-286.58, 289.7) * mm]});
            skFitSpline(sketch, "E1767", {"points": [v(-286.58, 289.7) * mm, v(-284.76, 289.01) * mm, v(-282.19, 288.83) * mm, v(-280.87, 289.3) * mm]});
            skFitSpline(sketch, "E1768", {"points": [v(-280.87, 289.3) * mm, v(-279.07, 289.94) * mm, v(-279.83, 290.38) * mm, v(-283.98, 291.08) * mm]});
            skFitSpline(sketch, "E1769", {"points": [v(-283.98, 291.08) * mm, v(-287, 291.58) * mm, v(-290.48, 292.52) * mm, v(-291.7, 293.16) * mm]});
            skFitSpline(sketch, "E1770", {"points": [v(-291.7, 293.16) * mm, v(-293.18, 293.94) * mm, v(-294.47, 293.87) * mm, v(-295.6, 292.94) * mm]});
            skFitSpline(sketch, "E1771", {"points": [v(-295.6, 292.94) * mm, v(-296.86, 291.88) * mm, v(-298.01, 292.04) * mm, v(-300.4, 293.6) * mm]});
            skFitSpline(sketch, "E1772", {"points": [v(-300.4, 293.6) * mm, v(-302.11, 294.73) * mm, v(-303.24, 296.1) * mm, v(-302.9, 296.66) * mm]});
            skFitSpline(sketch, "E1773", {"points": [v(-302.9, 296.66) * mm, v(-302.55, 297.21) * mm, v(-304.07, 297.84) * mm, v(-306.27, 298.05) * mm]});
            skFitSpline(sketch, "E1774", {"points": [v(-306.27, 298.05) * mm, v(-311.27, 298.54) * mm, v(-311.5, 300.76) * mm, v(-306.6, 301.24) * mm]});
            skFitSpline(sketch, "E1775", {"points": [v(-306.6, 301.24) * mm, v(-304.58, 301.44) * mm, v(-302.1, 301.93) * mm, v(-301.1, 302.33) * mm]});
            skFitSpline(sketch, "E1776", {"points": [v(-301.1, 302.33) * mm, v(-300.09, 302.74) * mm, v(-297.73, 302.94) * mm, v(-295.87, 302.8) * mm]});
            skFitSpline(sketch, "E1777", {"points": [v(-295.87, 302.8) * mm, v(-293.6, 302.61) * mm, v(-292.59, 303.06) * mm, v(-292.81, 304.15) * mm]});
            skFitSpline(sketch, "E1778", {"points": [v(-292.81, 304.15) * mm, v(-293.06, 305.32) * mm, v(-291.72, 305.7) * mm, v(-287.98, 305.54) * mm]});
            skFitSpline(sketch, "E1779", {"points": [v(-287.98, 305.54) * mm, v(-285.14, 305.42) * mm, v(-282.92, 305.7) * mm, v(-283.05, 306.15) * mm]});
            skFitSpline(sketch, "E1780", {"points": [v(-283.05, 306.15) * mm, v(-283.5, 307.8) * mm, v(-280.17, 312.57) * mm, v(-278.72, 312.34) * mm]});
            skFitSpline(sketch, "E1781", {"points": [v(-278.72, 312.34) * mm, v(-277.92, 312.21) * mm, v(-276.29, 312.53) * mm, v(-275.1, 313.05) * mm]});
            skFitSpline(sketch, "E1782", {"points": [v(-275.1, 313.05) * mm, v(-273.92, 313.57) * mm, v(-271.85, 313.7) * mm, v(-270.52, 313.36) * mm]});
            skFitSpline(sketch, "E1783", {"points": [v(-270.52, 313.36) * mm, v(-269.19, 313) * mm, v(-267.83, 313.15) * mm, v(-267.5, 313.68) * mm]});
            skFitSpline(sketch, "E1784", {"points": [v(-267.5, 313.68) * mm, v(-267.18, 314.2) * mm, v(-264.42, 314.16) * mm, v(-261.38, 313.6) * mm]});
            skFitSpline(sketch, "E1785", {"points": [v(-261.38, 313.6) * mm, v(-258.33, 313.03) * mm, v(-252.63, 312.84) * mm, v(-248.72, 313.18) * mm]});
            skFitSpline(sketch, "E1786", {"points": [v(-248.72, 313.18) * mm, v(-241.32, 313.83) * mm, v(-234.4, 312.17) * mm, v(-235.7, 310.05) * mm]});
            skFitSpline(sketch, "E1787", {"points": [v(-235.7, 310.05) * mm, v(-236.63, 308.54) * mm, v(-235.56, 308.51) * mm, v(-230.67, 309.91) * mm]});
            skFitSpline(sketch, "E1788", {"points": [v(-230.67, 309.91) * mm, v(-227.69, 310.77) * mm, v(-226.06, 310.49) * mm, v(-223.04, 308.57) * mm]});
            skFitSpline(sketch, "E1789", {"points": [v(-223.04, 308.57) * mm, v(-220.93, 307.24) * mm, v(-219.2, 305.66) * mm, v(-219.2, 305.06) * mm]});
            skFitSpline(sketch, "E1790", {"points": [v(-219.2, 305.06) * mm, v(-219.2, 303.69) * mm, v(-228.2, 299.07) * mm, v(-231.07, 298.97) * mm]});
            skFitSpline(sketch, "E1791", {"points": [v(-231.07, 298.97) * mm, v(-232.8, 298.9) * mm, v(-232.7, 298.66) * mm, v(-230.51, 297.79) * mm]});
            skFitSpline(sketch, "E1792", {"points": [v(-230.51, 297.79) * mm, v(-229, 297.18) * mm, v(-227.76, 296.4) * mm, v(-227.76, 296.05) * mm]});
            skFitSpline(sketch, "E1793", {"points": [v(-227.76, 296.05) * mm, v(-227.76, 295.7) * mm, v(-232.02, 293.4) * mm, v(-237.23, 290.92) * mm]});
            skFitSpline(sketch, "E1794", {"points": [v(-237.23, 290.92) * mm, v(-242.44, 288.45) * mm, v(-247.3, 285.61) * mm, v(-248.05, 284.6) * mm]});
            skFitSpline(sketch, "E1795", {"points": [v(-248.05, 284.6) * mm, v(-249.34, 282.86) * mm, v(-251.24, 282.95) * mm, v(-256.23, 285) * mm]});
            skFitSpline(sketch, "E1796", {"points": [v(-256.23, 285) * mm, v(-257.75, 285.63) * mm, v(-258.3, 285.4) * mm, v(-258.06, 284.25) * mm]});
            skFitSpline(sketch, "E1797", {"points": [v(-258.06, 284.25) * mm, v(-257.85, 283.3) * mm, v(-258.98, 282.42) * mm, v(-260.76, 282.17) * mm]});
            skFitSpline(sketch, "E1798", {"points": [v(-260.76, 282.17) * mm, v(-262.44, 281.93) * mm, v(-264.37, 281.19) * mm, v(-265.04, 280.52) * mm]});
            skFitSpline(sketch, "E1799", {"points": [v(-265.04, 280.52) * mm, v(-265.84, 279.73) * mm, v(-265.16, 279.6) * mm, v(-263.03, 280.12) * mm]});
            skFitSpline(sketch, "E1800", {"points": [v(-263.03, 280.12) * mm, v(-261.1, 280.6) * mm, v(-259.46, 280.35) * mm, v(-258.94, 279.51) * mm]});
            skFitSpline(sketch, "E1801", {"points": [v(-258.94, 279.51) * mm, v(-257.98, 277.96) * mm, v(-261.57, 273.38) * mm, v(-263.75, 273.38) * mm]});
            skFitSpline(sketch, "E1802", {"points": [v(-263.75, 273.38) * mm, v(-264.5, 273.38) * mm, v(-267.31, 272.24) * mm, v(-269.97, 270.86) * mm]});
            skFitSpline(sketch, "E1803", {"points": [v(-269.97, 270.86) * mm, v(-274.53, 268.48) * mm, v(-274.6, 268.35) * mm, v(-271.26, 268.72) * mm]});
            skFitSpline(sketch, "E1804", {"points": [v(-271.26, 268.72) * mm, v(-266.01, 269.29) * mm, v(-265.98, 266.45) * mm, v(-271.21, 264.27) * mm]});
            skFitSpline(sketch, "E1805", {"points": [v(-271.21, 264.27) * mm, v(-276.07, 262.23) * mm, v(-277.13, 262.04) * mm, v(-278.08, 263) * mm]});
            skFitSpline(sketch, "E1806", {"points": [v(14.8, 264.9) * mm, v(14.37, 265.61) * mm, v(12.65, 266.71) * mm, v(11, 267.34) * mm]});
            skFitSpline(sketch, "E1807", {"points": [v(11, 267.34) * mm, v(7.64, 268.62) * mm, v(8.2, 270.94) * mm, v(11.87, 270.94) * mm]});
            skFitSpline(sketch, "E1808", {"points": [v(11.87, 270.94) * mm, v(13.18, 270.94) * mm, v(14.24, 271.43) * mm, v(14.24, 272.02) * mm]});
            skFitSpline(sketch, "E1809", {"points": [v(14.24, 272.02) * mm, v(14.24, 272.62) * mm, v(13.45, 273.03) * mm, v(12.48, 272.94) * mm]});
            skFitSpline(sketch, "E1810", {"points": [v(12.48, 272.94) * mm, v(9.59, 272.66) * mm, v(9.75, 275.12) * mm, v(12.72, 276.42) * mm]});
            skFitSpline(sketch, "E1811", {"points": [v(12.72, 276.42) * mm, v(14.23, 277.09) * mm, v(15.47, 278.03) * mm, v(15.47, 278.52) * mm]});
            skFitSpline(sketch, "E1812", {"points": [v(15.47, 278.52) * mm, v(15.47, 279.75) * mm, v(11.65, 278.3) * mm, v(9.07, 276.08) * mm]});
            skFitSpline(sketch, "E1813", {"points": [v(9.07, 276.08) * mm, v(7.42, 274.66) * mm, v(6.57, 274.58) * mm, v(5.2, 275.72) * mm]});
            skFitSpline(sketch, "E1814", {"points": [v(5.2, 275.72) * mm, v(3.94, 276.77) * mm, v(3.23, 276.8) * mm, v(2.62, 275.8) * mm]});
            skFitSpline(sketch, "E1815", {"points": [v(2.62, 275.8) * mm, v(2.04, 274.87) * mm, v(1.07, 275.1) * mm, v(-0.51, 276.52) * mm]});
            skFitSpline(sketch, "E1816", {"points": [v(-0.51, 276.52) * mm, v(-2.67, 278.47) * mm, v(-2.64, 281.47) * mm, v(-0.48, 280.14) * mm]});
            skFitSpline(sketch, "E1817", {"points": [v(-0.48, 280.14) * mm, v(0.07, 279.8) * mm, v(1.24, 280.39) * mm, v(2.12, 281.45) * mm]});
            skFitSpline(sketch, "E1818", {"points": [v(2.12, 281.45) * mm, v(3.5, 283.1) * mm, v(3.38, 283.32) * mm, v(1.35, 282.96) * mm]});
            skFitSpline(sketch, "E1819", {"points": [v(1.35, 282.96) * mm, v(-0.1, 282.71) * mm, v(-1.03, 283.24) * mm, v(-1.03, 284.3) * mm]});
            skFitSpline(sketch, "E1820", {"points": [v(-1.03, 284.3) * mm, v(-1.03, 286.34) * mm, v(6.26, 288.56) * mm, v(9.2, 287.42) * mm]});
            skFitSpline(sketch, "E1821", {"points": [v(9.2, 287.42) * mm, v(10.97, 286.74) * mm, v(10.92, 286.46) * mm, v(8.82, 284.9) * mm]});
            skFitSpline(sketch, "E1822", {"points": [v(8.82, 284.9) * mm, v(6.8, 283.42) * mm, v(6.75, 283.16) * mm, v(8.47, 283.16) * mm]});
            skFitSpline(sketch, "E1823", {"points": [v(8.47, 283.16) * mm, v(9.58, 283.16) * mm, v(11.07, 284.24) * mm, v(11.78, 285.56) * mm]});
            skFitSpline(sketch, "E1824", {"points": [v(11.78, 285.56) * mm, v(13.2, 288.2) * mm, v(16.26, 287.78) * mm, v(18.83, 284.58) * mm]});
            skFitSpline(sketch, "E1825", {"points": [v(18.83, 284.58) * mm, v(19.99, 283.14) * mm, v(20.7, 283.02) * mm, v(21.78, 284.09) * mm]});
            skFitSpline(sketch, "E1826", {"points": [v(21.78, 284.09) * mm, v(22.84, 285.16) * mm, v(22.83, 285.93) * mm, v(21.71, 287.28) * mm]});
            skFitSpline(sketch, "E1827", {"points": [v(21.71, 287.28) * mm, v(20.9, 288.25) * mm, v(20.7, 289.34) * mm, v(21.27, 289.7) * mm]});
            skFitSpline(sketch, "E1828", {"points": [v(21.27, 289.7) * mm, v(22.9, 290.7) * mm, v(28.68, 289.76) * mm, v(30.57, 288.2) * mm]});
            skFitSpline(sketch, "E1829", {"points": [v(30.57, 288.2) * mm, v(31.92, 287.07) * mm, v(32.4, 287.27) * mm, v(32.9, 289.15) * mm]});
            skFitSpline(sketch, "E1830", {"points": [v(32.9, 289.15) * mm, v(33.57, 291.7) * mm, v(35, 291.72) * mm, v(44.19, 289.4) * mm]});
            skFitSpline(sketch, "E1831", {"points": [v(44.19, 289.4) * mm, v(46.88, 288.72) * mm, v(49.22, 288.14) * mm, v(49.38, 288.1) * mm]});
            skFitSpline(sketch, "E1832", {"points": [v(49.38, 288.1) * mm, v(50.32, 287.93) * mm, v(48.85, 286.23) * mm, v(47.6, 286.05) * mm]});
            skFitSpline(sketch, "E1833", {"points": [v(47.6, 286.05) * mm, v(46.78, 285.93) * mm, v(44.41, 284.62) * mm, v(42.34, 283.14) * mm]});
            skFitSpline(sketch, "E1834", {"points": [v(42.34, 283.14) * mm, v(38.95, 280.74) * mm, v(38, 280.6) * mm, v(33.2, 281.8) * mm]});
            skFitSpline(sketch, "E1835", {"points": [v(33.2, 281.8) * mm, v(26.46, 283.5) * mm, v(22.07, 283.54) * mm, v(26.24, 281.87) * mm]});
            skFitSpline(sketch, "E1836", {"points": [v(26.24, 281.87) * mm, v(27.8, 281.25) * mm, v(28.73, 280.18) * mm, v(28.3, 279.5) * mm]});
            skFitSpline(sketch, "E1837", {"points": [v(28.3, 279.5) * mm, v(27.89, 278.82) * mm, v(28.37, 278.27) * mm, v(29.38, 278.27) * mm]});
            skFitSpline(sketch, "E1838", {"points": [v(29.38, 278.27) * mm, v(30.39, 278.27) * mm, v(33.19, 277.1) * mm, v(35.6, 275.69) * mm]});
            skFitSpline(sketch, "E1839", {"points": [v(35.6, 275.69) * mm, v(38.82, 273.78) * mm, v(39.65, 272.7) * mm, v(38.73, 271.6) * mm]});
            skFitSpline(sketch, "E1840", {"points": [v(38.73, 271.6) * mm, v(36.98, 269.49) * mm, v(29.42, 269.83) * mm, v(29.87, 272) * mm]});
            skFitSpline(sketch, "E1841", {"points": [v(29.87, 272) * mm, v(30.27, 273.85) * mm, v(26.42, 277.16) * mm, v(24.93, 276.24) * mm]});
            skFitSpline(sketch, "E1842", {"points": [v(24.93, 276.24) * mm, v(24.4, 275.92) * mm, v(22.6, 272.94) * mm, v(20.92, 269.63) * mm]});
            skFitSpline(sketch, "E1843", {"points": [v(20.92, 269.63) * mm, v(17.88, 263.63) * mm, v(16.34, 262.43) * mm, v(14.8, 264.9) * mm]});
            skFitSpline(sketch, "E1844", {"points": [v(-373.15, 270.25) * mm, v(-373.95, 271.22) * mm, v(-375.34, 271.73) * mm, v(-376.23, 271.4) * mm]});
            skFitSpline(sketch, "E1845", {"points": [v(-376.23, 271.4) * mm, v(-378.28, 270.6) * mm, v(-379.98, 273.2) * mm, v(-378.43, 274.76) * mm]});
            skFitSpline(sketch, "E1846", {"points": [v(-378.43, 274.76) * mm, v(-377.68, 275.5) * mm, v(-376.7, 275.27) * mm, v(-375.75, 274.12) * mm]});
            skFitSpline(sketch, "E1847", {"points": [v(-375.75, 274.12) * mm, v(-374.93, 273.12) * mm, v(-373.45, 272.61) * mm, v(-372.47, 272.99) * mm]});
            skFitSpline(sketch, "E1848", {"points": [v(-372.47, 272.99) * mm, v(-371.17, 273.49) * mm, v(-371.05, 274.09) * mm, v(-372.01, 275.25) * mm]});
            skFitSpline(sketch, "E1849", {"points": [v(-372.01, 275.25) * mm, v(-373.6, 277.15) * mm, v(-372.57, 277.9) * mm, v(-367.7, 278.4) * mm]});
            skFitSpline(sketch, "E1850", {"points": [v(-367.7, 278.4) * mm, v(-363.87, 278.8) * mm, v(-360.98, 277.69) * mm, v(-360.98, 275.8) * mm]});
            skFitSpline(sketch, "E1851", {"points": [v(-360.98, 275.8) * mm, v(-360.98, 274.7) * mm, v(-369.4, 268.5) * mm, v(-370.9, 268.5) * mm]});
            skFitSpline(sketch, "E1852", {"points": [v(-370.9, 268.5) * mm, v(-371.33, 268.5) * mm, v(-372.34, 269.28) * mm, v(-373.15, 270.25) * mm]});
            skFitSpline(sketch, "E1853", {"points": [v(-335.93, 273.39) * mm, v(-338.1, 275.79) * mm, v(-340.5, 276.7) * mm, v(-339.9, 274.9) * mm]});
            skFitSpline(sketch, "E1854", {"points": [v(-339.9, 274.9) * mm, v(-339.73, 274.4) * mm, v(-340, 273.85) * mm, v(-340.51, 273.69) * mm]});
            skFitSpline(sketch, "E1855", {"points": [v(-340.51, 273.69) * mm, v(-342.58, 273) * mm, v(-342.87, 273.48) * mm, v(-341.44, 275.2) * mm]});
            skFitSpline(sketch, "E1856", {"points": [v(-341.44, 275.2) * mm, v(-339.76, 277.23) * mm, v(-341.46, 278.43) * mm, v(-345.33, 277.93) * mm]});
            skFitSpline(sketch, "E1857", {"points": [v(-345.33, 277.93) * mm, v(-346.47, 277.78) * mm, v(-347.3, 278.05) * mm, v(-347.16, 278.52) * mm]});
            skFitSpline(sketch, "E1858", {"points": [v(-347.16, 278.52) * mm, v(-347.03, 279) * mm, v(-347.94, 280.13) * mm, v(-349.18, 281.03) * mm]});
            skFitSpline(sketch, "E1859", {"points": [v(-349.18, 281.03) * mm, v(-351.14, 282.46) * mm, v(-351.2, 282.87) * mm, v(-349.63, 284.17) * mm]});
            skFitSpline(sketch, "E1860", {"points": [v(-349.63, 284.17) * mm, v(-346.96, 286.39) * mm, v(-337, 282.33) * mm, v(-333.3, 277.52) * mm]});
            skFitSpline(sketch, "E1861", {"points": [v(-333.3, 277.52) * mm, v(-330.88, 274.37) * mm, v(-330.66, 273.49) * mm, v(-332.05, 272.33) * mm]});
            skFitSpline(sketch, "E1862", {"points": [v(-332.05, 272.33) * mm, v(-333.34, 271.26) * mm, v(-334.23, 271.5) * mm, v(-335.93, 273.39) * mm]});
            skFitSpline(sketch, "E1863", {"points": [v(264.05, 273.62) * mm, v(262.9, 275.48) * mm, v(270.3, 283.79) * mm, v(272.97, 283.64) * mm]});
            skFitSpline(sketch, "E1864", {"points": [v(272.97, 283.64) * mm, v(274.28, 283.57) * mm, v(276.83, 282.54) * mm, v(278.65, 281.35) * mm]});
            skFitSpline(sketch, "E1865", {"points": [v(278.65, 281.35) * mm, v(281.25, 279.65) * mm, v(281.66, 278.82) * mm, v(280.56, 277.5) * mm]});
            skFitSpline(sketch, "E1866", {"points": [v(280.56, 277.5) * mm, v(279.8, 276.58) * mm, v(278, 275.8) * mm, v(276.57, 275.77) * mm]});
            skFitSpline(sketch, "E1867", {"points": [v(276.57, 275.77) * mm, v(275.14, 275.74) * mm, v(271.9, 274.98) * mm, v(269.37, 274.08) * mm]});
            skFitSpline(sketch, "E1868", {"points": [v(269.37, 274.08) * mm, v(266.51, 273.06) * mm, v(264.5, 272.88) * mm, v(264.05, 273.62) * mm]});
            skFitSpline(sketch, "E1869", {"points": [v(259.31, 277.36) * mm, v(257.99, 278.1) * mm, v(253.58, 279.57) * mm, v(249.53, 280.63) * mm]});
            skFitSpline(sketch, "E1870", {"points": [v(249.53, 280.63) * mm, v(245.47, 281.68) * mm, v(241.94, 283.1) * mm, v(241.68, 283.77) * mm]});
            skFitSpline(sketch, "E1871", {"points": [v(241.68, 283.77) * mm, v(241.42, 284.44) * mm, v(240.33, 285.64) * mm, v(239.26, 286.44) * mm]});
            skFitSpline(sketch, "E1872", {"points": [v(239.26, 286.44) * mm, v(237.52, 287.72) * mm, v(237.6, 287.99) * mm, v(239.98, 288.88) * mm]});
            skFitSpline(sketch, "E1873", {"points": [v(239.98, 288.88) * mm, v(241.45, 289.43) * mm, v(242.65, 290.43) * mm, v(242.64, 291.1) * mm]});
            skFitSpline(sketch, "E1874", {"points": [v(242.64, 291.1) * mm, v(242.62, 291.78) * mm, v(244.49, 293.51) * mm, v(246.78, 294.96) * mm]});
            skFitSpline(sketch, "E1875", {"points": [v(246.78, 294.96) * mm, v(248.17, 295.84) * mm, v(249.56, 296.72) * mm, v(250.95, 297.6) * mm]});
            skFitSpline(sketch, "E1876", {"points": [v(250.95, 297.6) * mm, v(252.24, 296.79) * mm, v(253.53, 295.97) * mm, v(254.82, 295.15) * mm]});
            skFitSpline(sketch, "E1877", {"points": [v(254.82, 295.15) * mm, v(257.7, 293.33) * mm, v(258.41, 292.22) * mm, v(257.63, 290.81) * mm]});
            skFitSpline(sketch, "E1878", {"points": [v(257.63, 290.81) * mm, v(257.04, 289.77) * mm, v(256.84, 287.88) * mm, v(257.17, 286.6) * mm]});
            skFitSpline(sketch, "E1879", {"points": [v(257.17, 286.6) * mm, v(257.76, 284.38) * mm, v(257.86, 284.39) * mm, v(259.57, 286.83) * mm]});
            skFitSpline(sketch, "E1880", {"points": [v(259.57, 286.83) * mm, v(262.1, 290.43) * mm, v(264.95, 287.85) * mm, v(264.58, 282.32) * mm]});
            skFitSpline(sketch, "E1881", {"points": [v(264.58, 282.32) * mm, v(264.23, 277.18) * mm, v(262.51, 275.57) * mm, v(259.31, 277.36) * mm]});
            skSolve(sketch);
        }
        {
            var Q0;
            Q0 = qSketchRegion(id + "F1", true);
            var Q1;
            Q1=makeQuery(id+"F0.imprint","IMPRINT",FACE,{"disambiguationData":[TD([[makeQuery(id+"F0.imprint","IMPRINT",EDGE,{"derivedFrom":sQuery(id+"F0.wireOp",EDGE,"E0.bottom")}),-1.0]])]});
            extrude(context, id + "F2", {"entities" : qUnion([Q0, Q1]), "depth" : 25.4 * mm, "offsetDistance" : 25.4 * mm});
        }
        {
            var Q0;
            Q0 = qSketchRegion(id + "F1", true);
            extrude(context, id + "F3", {"entities" : qUnion([Q0]), "operationType" : NewBodyOperationType.REMOVE, "oppositeDirection" : true, "depth" : 25.4 * mm, "offsetDistance" : 25.4 * mm});
        }
    });
